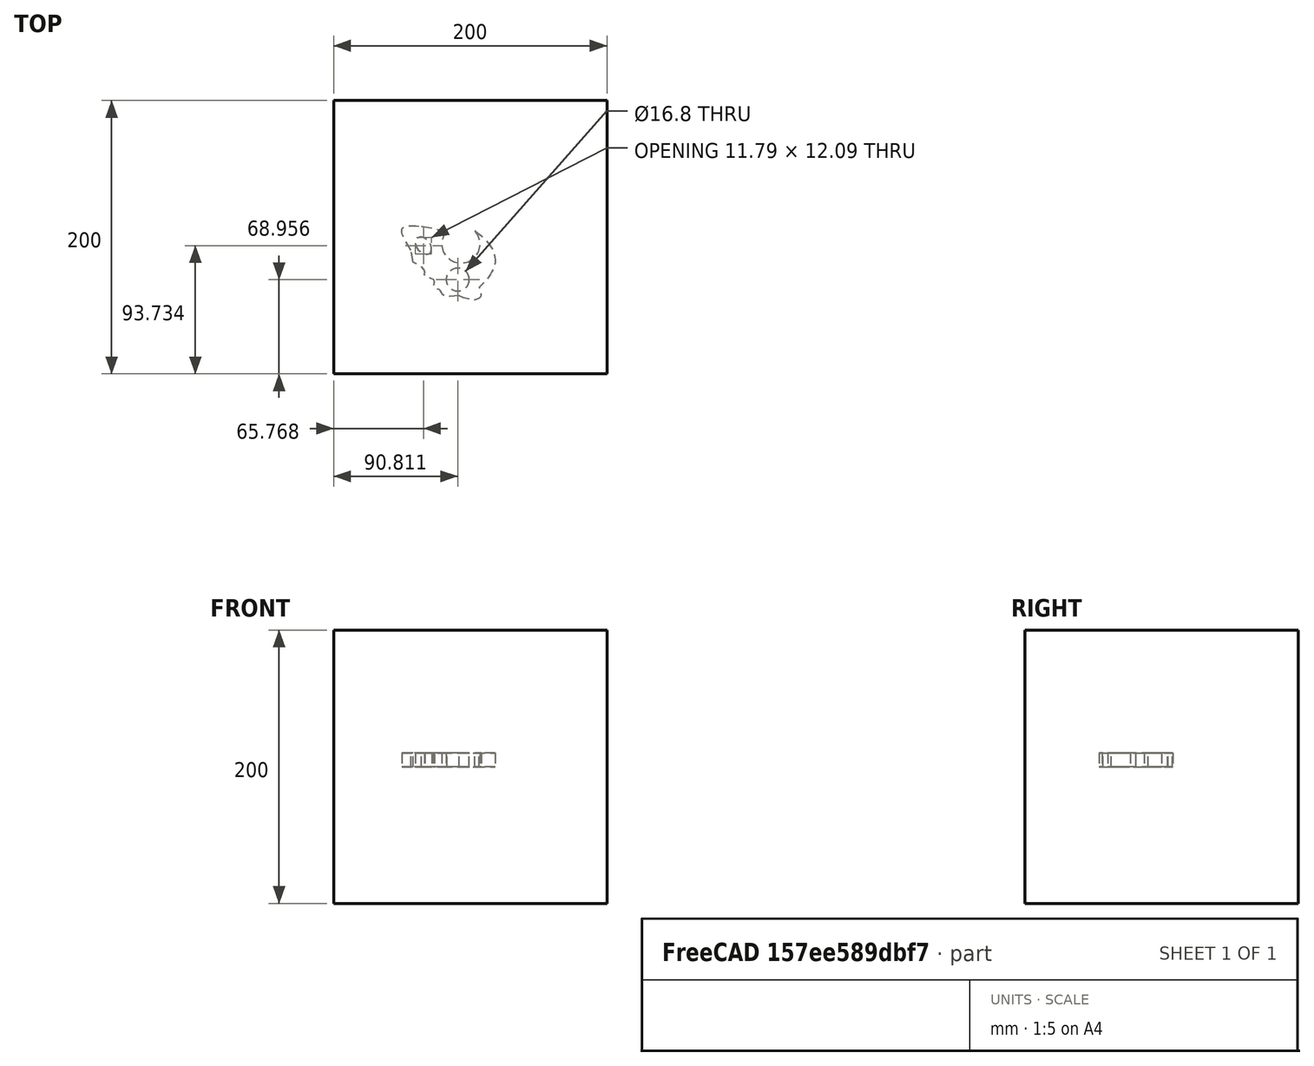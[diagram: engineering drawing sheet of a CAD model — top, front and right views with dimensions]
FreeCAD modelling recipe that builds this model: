
FCSTD DOCUMENT  (FreeCAD 0.19RUnknown)
Label: extrudeAllShapes
License: All rights reserved
LicenseURL: http://en.wikipedia.org/wiki/All_rights_reserved
objects: App::DocumentObjectGroupPython×1248, App::Part×2, Part::FeaturePython×1, Sketcher::SketchObject×1, Part::Extrusion×1
note: 3 computed .brp shape members not serialized (recipe doc carries the construction recipe); baked Part::Feature solids carry a one-line shape summary decoded from their .brp

FEATURE [App::DocumentObjectGroupPython] HALFPI  # scripted group (container) (typed FeaturePython)
  name = HALFPI
  value = pi/2.
FEATURE [App::DocumentObjectGroupPython] PI  # scripted group (container) (typed FeaturePython)
  name = PI
  value = 1.*pi
FEATURE [App::DocumentObjectGroupPython] TWOPI  # scripted group (container) (typed FeaturePython)
  name = TWOPI
  value = 2.*pi
FEATURE [App::DocumentObjectGroupPython] Constants  # scripted group (container) (typed FeaturePython)
  Group = -> [HALFPI,PI,TWOPI]
FEATURE [App::DocumentObjectGroupPython] Variables  # scripted group (container) (typed FeaturePython)
FEATURE [App::DocumentObjectGroupPython] Quantities  # scripted group (container) (typed FeaturePython)
FEATURE [App::DocumentObjectGroupPython] Isotopes  # scripted group (container) (typed FeaturePython)
FEATURE [App::DocumentObjectGroupPython] Elements  # scripted group (container) (typed FeaturePython)
FEATURE [App::DocumentObjectGroupPython] G4Isotopes  # scripted group (container) (typed FeaturePython)
FEATURE [App::DocumentObjectGroupPython] H_element  # scripted group (container) (typed FeaturePython)
  Z = 1
  atom_value = 1.008
  formula = H
  name = H_element
FEATURE [App::DocumentObjectGroupPython] He_element  # scripted group (container) (typed FeaturePython)
  Z = 2
  atom_value = 4.0026
  formula = He
  name = He_element
FEATURE [App::DocumentObjectGroupPython] Li_element  # scripted group (container) (typed FeaturePython)
  Z = 3
  atom_value = 6.94
  formula = Li
  name = Li_element
FEATURE [App::DocumentObjectGroupPython] Be_element  # scripted group (container) (typed FeaturePython)
  Z = 4
  atom_value = 9.01218
  formula = Be
  name = Be_element
FEATURE [App::DocumentObjectGroupPython] B_element  # scripted group (container) (typed FeaturePython)
  Z = 5
  atom_value = 10.81
  formula = B
  name = B_element
FEATURE [App::DocumentObjectGroupPython] C_element  # scripted group (container) (typed FeaturePython)
  Z = 6
  atom_value = 12.011
  formula = C
  name = C_element
FEATURE [App::DocumentObjectGroupPython] N_element  # scripted group (container) (typed FeaturePython)
  Z = 7
  atom_value = 14.007
  formula = N
  name = N_element
FEATURE [App::DocumentObjectGroupPython] O_element  # scripted group (container) (typed FeaturePython)
  Z = 8
  atom_value = 15.999
  formula = O
  name = O_element
FEATURE [App::DocumentObjectGroupPython] F_element  # scripted group (container) (typed FeaturePython)
  Z = 9
  atom_value = 18.9984
  formula = F
  name = F_element
FEATURE [App::DocumentObjectGroupPython] Ne_element  # scripted group (container) (typed FeaturePython)
  Z = 10
  atom_value = 20.1797
  formula = Ne
  name = Ne_element
FEATURE [App::DocumentObjectGroupPython] Na_element  # scripted group (container) (typed FeaturePython)
  Z = 11
  atom_value = 22.9898
  formula = Na
  name = Na_element
FEATURE [App::DocumentObjectGroupPython] Mg_element  # scripted group (container) (typed FeaturePython)
  Z = 12
  atom_value = 24.305
  formula = Mg
  name = Mg_element
FEATURE [App::DocumentObjectGroupPython] Al_element  # scripted group (container) (typed FeaturePython)
  Z = 13
  atom_value = 26.9815
  formula = Al
  name = Al_element
FEATURE [App::DocumentObjectGroupPython] Si_element  # scripted group (container) (typed FeaturePython)
  Z = 14
  atom_value = 28.085
  formula = Si
  name = Si_element
FEATURE [App::DocumentObjectGroupPython] P_element  # scripted group (container) (typed FeaturePython)
  Z = 15
  atom_value = 30.9738
  formula = P
  name = P_element
FEATURE [App::DocumentObjectGroupPython] S_element  # scripted group (container) (typed FeaturePython)
  Z = 16
  atom_value = 32.06
  formula = S
  name = S_element
FEATURE [App::DocumentObjectGroupPython] Cl_element  # scripted group (container) (typed FeaturePython)
  Z = 17
  atom_value = 35.45
  formula = Cl
  name = Cl_element
FEATURE [App::DocumentObjectGroupPython] Ar_element  # scripted group (container) (typed FeaturePython)
  Z = 18
  atom_value = 39.95
  formula = Ar
  name = Ar_element
FEATURE [App::DocumentObjectGroupPython] K_element  # scripted group (container) (typed FeaturePython)
  Z = 19
  atom_value = 39.0983
  formula = K
  name = K_element
FEATURE [App::DocumentObjectGroupPython] Ca_element  # scripted group (container) (typed FeaturePython)
  Z = 20
  atom_value = 40.078
  formula = Ca
  name = Ca_element
FEATURE [App::DocumentObjectGroupPython] Sc_element  # scripted group (container) (typed FeaturePython)
  Z = 21
  atom_value = 44.9559
  formula = Sc
  name = Sc_element
FEATURE [App::DocumentObjectGroupPython] Ti_element  # scripted group (container) (typed FeaturePython)
  Z = 22
  atom_value = 47.867
  formula = Ti
  name = Ti_element
FEATURE [App::DocumentObjectGroupPython] V_element  # scripted group (container) (typed FeaturePython)
  Z = 23
  atom_value = 50.9415
  formula = V
  name = V_element
FEATURE [App::DocumentObjectGroupPython] Cr_element  # scripted group (container) (typed FeaturePython)
  Z = 24
  atom_value = 51.9961
  formula = Cr
  name = Cr_element
FEATURE [App::DocumentObjectGroupPython] Mn_element  # scripted group (container) (typed FeaturePython)
  Z = 25
  atom_value = 54.938
  formula = Mn
  name = Mn_element
FEATURE [App::DocumentObjectGroupPython] Fe_element  # scripted group (container) (typed FeaturePython)
  Z = 26
  atom_value = 55.845
  formula = Fe
  name = Fe_element
FEATURE [App::DocumentObjectGroupPython] Co_element  # scripted group (container) (typed FeaturePython)
  Z = 27
  atom_value = 58.9332
  formula = Co
  name = Co_element
FEATURE [App::DocumentObjectGroupPython] Ni_element  # scripted group (container) (typed FeaturePython)
  Z = 28
  atom_value = 58.6934
  formula = Ni
  name = Ni_element
FEATURE [App::DocumentObjectGroupPython] Cu_element  # scripted group (container) (typed FeaturePython)
  Z = 29
  atom_value = 63.546
  formula = Cu
  name = Cu_element
FEATURE [App::DocumentObjectGroupPython] Zn_element  # scripted group (container) (typed FeaturePython)
  Z = 30
  atom_value = 65.38
  formula = Zn
  name = Zn_element
FEATURE [App::DocumentObjectGroupPython] Ga_element  # scripted group (container) (typed FeaturePython)
  Z = 31
  atom_value = 69.723
  formula = Ga
  name = Ga_element
FEATURE [App::DocumentObjectGroupPython] Ge_element  # scripted group (container) (typed FeaturePython)
  Z = 32
  atom_value = 72.63
  formula = Ge
  name = Ge_element
FEATURE [App::DocumentObjectGroupPython] As_element  # scripted group (container) (typed FeaturePython)
  Z = 33
  atom_value = 74.9216
  formula = As
  name = As_element
FEATURE [App::DocumentObjectGroupPython] Se_element  # scripted group (container) (typed FeaturePython)
  Z = 34
  atom_value = 78.971
  formula = Se
  name = Se_element
FEATURE [App::DocumentObjectGroupPython] Br_element  # scripted group (container) (typed FeaturePython)
  Z = 35
  atom_value = 79.904
  formula = Br
  name = Br_element
FEATURE [App::DocumentObjectGroupPython] Kr_element  # scripted group (container) (typed FeaturePython)
  Z = 36
  atom_value = 83.798
  formula = Kr
  name = Kr_element
FEATURE [App::DocumentObjectGroupPython] Rb_element  # scripted group (container) (typed FeaturePython)
  Z = 37
  atom_value = 85.4678
  formula = Rb
  name = Rb_element
FEATURE [App::DocumentObjectGroupPython] Sr_element  # scripted group (container) (typed FeaturePython)
  Z = 38
  atom_value = 87.62
  formula = Sr
  name = Sr_element
FEATURE [App::DocumentObjectGroupPython] Y_element  # scripted group (container) (typed FeaturePython)
  Z = 39
  atom_value = 88.9058
  formula = Y
  name = Y_element
FEATURE [App::DocumentObjectGroupPython] Zr_element  # scripted group (container) (typed FeaturePython)
  Z = 40
  atom_value = 91.224
  formula = Zr
  name = Zr_element
FEATURE [App::DocumentObjectGroupPython] Nb_element  # scripted group (container) (typed FeaturePython)
  Z = 41
  atom_value = 92.9064
  formula = Nb
  name = Nb_element
FEATURE [App::DocumentObjectGroupPython] Mo_element  # scripted group (container) (typed FeaturePython)
  Z = 42
  atom_value = 95.95
  formula = Mo
  name = Mo_element
FEATURE [App::DocumentObjectGroupPython] Tc_element  # scripted group (container) (typed FeaturePython)
  Z = 43
  atom_value = 97
  formula = Tc
  name = Tc_element
FEATURE [App::DocumentObjectGroupPython] Ru_element  # scripted group (container) (typed FeaturePython)
  Z = 44
  atom_value = 101.07
  formula = Ru
  name = Ru_element
FEATURE [App::DocumentObjectGroupPython] Rh_element  # scripted group (container) (typed FeaturePython)
  Z = 45
  atom_value = 102.905
  formula = Rh
  name = Rh_element
FEATURE [App::DocumentObjectGroupPython] Pd_element  # scripted group (container) (typed FeaturePython)
  Z = 46
  atom_value = 106.42
  formula = Pd
  name = Pd_element
FEATURE [App::DocumentObjectGroupPython] Ag_element  # scripted group (container) (typed FeaturePython)
  Z = 47
  atom_value = 107.868
  formula = Ag
  name = Ag_element
FEATURE [App::DocumentObjectGroupPython] Cd_element  # scripted group (container) (typed FeaturePython)
  Z = 48
  atom_value = 112.414
  formula = Cd
  name = Cd_element
FEATURE [App::DocumentObjectGroupPython] In_element  # scripted group (container) (typed FeaturePython)
  Z = 49
  atom_value = 114.818
  formula = In
  name = In_element
FEATURE [App::DocumentObjectGroupPython] Sn_element  # scripted group (container) (typed FeaturePython)
  Z = 50
  atom_value = 118.71
  formula = Sn
  name = Sn_element
FEATURE [App::DocumentObjectGroupPython] Sb_element  # scripted group (container) (typed FeaturePython)
  Z = 51
  atom_value = 121.76
  formula = Sb
  name = Sb_element
FEATURE [App::DocumentObjectGroupPython] Te_element  # scripted group (container) (typed FeaturePython)
  Z = 52
  atom_value = 127.6
  formula = Te
  name = Te_element
FEATURE [App::DocumentObjectGroupPython] I_element  # scripted group (container) (typed FeaturePython)
  Z = 53
  atom_value = 126.904
  formula = I
  name = I_element
FEATURE [App::DocumentObjectGroupPython] Xe_element  # scripted group (container) (typed FeaturePython)
  Z = 54
  atom_value = 131.293
  formula = Xe
  name = Xe_element
FEATURE [App::DocumentObjectGroupPython] Cs_element  # scripted group (container) (typed FeaturePython)
  Z = 55
  atom_value = 132.905
  formula = Cs
  name = Cs_element
FEATURE [App::DocumentObjectGroupPython] Ba_element  # scripted group (container) (typed FeaturePython)
  Z = 56
  atom_value = 137.327
  formula = Ba
  name = Ba_element
FEATURE [App::DocumentObjectGroupPython] La_element  # scripted group (container) (typed FeaturePython)
  Z = 57
  atom_value = 138.905
  formula = La
  name = La_element
FEATURE [App::DocumentObjectGroupPython] Ce_element  # scripted group (container) (typed FeaturePython)
  Z = 58
  atom_value = 140.116
  formula = Ce
  name = Ce_element
FEATURE [App::DocumentObjectGroupPython] Pr_element  # scripted group (container) (typed FeaturePython)
  Z = 59
  atom_value = 140.908
  formula = Pr
  name = Pr_element
FEATURE [App::DocumentObjectGroupPython] Nd_element  # scripted group (container) (typed FeaturePython)
  Z = 60
  atom_value = 144.242
  formula = Nd
  name = Nd_element
FEATURE [App::DocumentObjectGroupPython] Pm_element  # scripted group (container) (typed FeaturePython)
  Z = 61
  atom_value = 145
  formula = Pm
  name = Pm_element
FEATURE [App::DocumentObjectGroupPython] Sm_element  # scripted group (container) (typed FeaturePython)
  Z = 62
  atom_value = 150.36
  formula = Sm
  name = Sm_element
FEATURE [App::DocumentObjectGroupPython] Eu_element  # scripted group (container) (typed FeaturePython)
  Z = 63
  atom_value = 151.964
  formula = Eu
  name = Eu_element
FEATURE [App::DocumentObjectGroupPython] Gd_element  # scripted group (container) (typed FeaturePython)
  Z = 64
  atom_value = 157.25
  formula = Gd
  name = Gd_element
FEATURE [App::DocumentObjectGroupPython] Tb_element  # scripted group (container) (typed FeaturePython)
  Z = 65
  atom_value = 158.925
  formula = Tb
  name = Tb_element
FEATURE [App::DocumentObjectGroupPython] Dy_element  # scripted group (container) (typed FeaturePython)
  Z = 66
  atom_value = 162.5
  formula = Dy
  name = Dy_element
FEATURE [App::DocumentObjectGroupPython] Ho_element  # scripted group (container) (typed FeaturePython)
  Z = 67
  atom_value = 164.93
  formula = Ho
  name = Ho_element
FEATURE [App::DocumentObjectGroupPython] Er_element  # scripted group (container) (typed FeaturePython)
  Z = 68
  atom_value = 167.259
  formula = Er
  name = Er_element
FEATURE [App::DocumentObjectGroupPython] Tm_element  # scripted group (container) (typed FeaturePython)
  Z = 69
  atom_value = 168.934
  formula = Tm
  name = Tm_element
FEATURE [App::DocumentObjectGroupPython] Yb_element  # scripted group (container) (typed FeaturePython)
  Z = 70
  atom_value = 173.045
  formula = Yb
  name = Yb_element
FEATURE [App::DocumentObjectGroupPython] Lu_element  # scripted group (container) (typed FeaturePython)
  Z = 71
  atom_value = 174.967
  formula = Lu
  name = Lu_element
FEATURE [App::DocumentObjectGroupPython] Hf_element  # scripted group (container) (typed FeaturePython)
  Z = 72
  atom_value = 178.49
  formula = Hf
  name = Hf_element
FEATURE [App::DocumentObjectGroupPython] Ta_element  # scripted group (container) (typed FeaturePython)
  Z = 73
  atom_value = 180.948
  formula = Ta
  name = Ta_element
FEATURE [App::DocumentObjectGroupPython] W_element  # scripted group (container) (typed FeaturePython)
  Z = 74
  atom_value = 183.84
  formula = W
  name = W_element
FEATURE [App::DocumentObjectGroupPython] Re_element  # scripted group (container) (typed FeaturePython)
  Z = 75
  atom_value = 186.207
  formula = Re
  name = Re_element
FEATURE [App::DocumentObjectGroupPython] Os_element  # scripted group (container) (typed FeaturePython)
  Z = 76
  atom_value = 190.23
  formula = Os
  name = Os_element
FEATURE [App::DocumentObjectGroupPython] Ir_element  # scripted group (container) (typed FeaturePython)
  Z = 77
  atom_value = 192.217
  formula = Ir
  name = Ir_element
FEATURE [App::DocumentObjectGroupPython] Pt_element  # scripted group (container) (typed FeaturePython)
  Z = 78
  atom_value = 195.084
  formula = Pt
  name = Pt_element
FEATURE [App::DocumentObjectGroupPython] Au_element  # scripted group (container) (typed FeaturePython)
  Z = 79
  atom_value = 196.967
  formula = Au
  name = Au_element
FEATURE [App::DocumentObjectGroupPython] Hg_element  # scripted group (container) (typed FeaturePython)
  Z = 80
  atom_value = 200.592
  formula = Hg
  name = Hg_element
FEATURE [App::DocumentObjectGroupPython] Tl_element  # scripted group (container) (typed FeaturePython)
  Z = 81
  atom_value = 204.38
  formula = Tl
  name = Tl_element
FEATURE [App::DocumentObjectGroupPython] Pb_element  # scripted group (container) (typed FeaturePython)
  Z = 82
  atom_value = 207.2
  formula = Pb
  name = Pb_element
FEATURE [App::DocumentObjectGroupPython] Bi_element  # scripted group (container) (typed FeaturePython)
  Z = 83
  atom_value = 208.98
  formula = Bi
  name = Bi_element
FEATURE [App::DocumentObjectGroupPython] Po_element  # scripted group (container) (typed FeaturePython)
  Z = 84
  atom_value = 209
  formula = Po
  name = Po_element
FEATURE [App::DocumentObjectGroupPython] At_element  # scripted group (container) (typed FeaturePython)
  Z = 85
  atom_value = 210
  formula = At
  name = At_element
FEATURE [App::DocumentObjectGroupPython] Rn_element  # scripted group (container) (typed FeaturePython)
  Z = 86
  atom_value = 222
  formula = Rn
  name = Rn_element
FEATURE [App::DocumentObjectGroupPython] Fr_element  # scripted group (container) (typed FeaturePython)
  Z = 87
  atom_value = 223
  formula = Fr
  name = Fr_element
FEATURE [App::DocumentObjectGroupPython] Ra_element  # scripted group (container) (typed FeaturePython)
  Z = 88
  atom_value = 226
  formula = Ra
  name = Ra_element
FEATURE [App::DocumentObjectGroupPython] Ac_element  # scripted group (container) (typed FeaturePython)
  Z = 89
  atom_value = 227
  formula = Ac
  name = Ac_element
FEATURE [App::DocumentObjectGroupPython] Th_element  # scripted group (container) (typed FeaturePython)
  Z = 90
  atom_value = 232.038
  formula = Th
  name = Th_element
FEATURE [App::DocumentObjectGroupPython] Pa_element  # scripted group (container) (typed FeaturePython)
  Z = 91
  atom_value = 231.036
  formula = Pa
  name = Pa_element
FEATURE [App::DocumentObjectGroupPython] U_element  # scripted group (container) (typed FeaturePython)
  Z = 92
  atom_value = 238.029
  formula = U
  name = U_element
FEATURE [App::DocumentObjectGroupPython] Np_element  # scripted group (container) (typed FeaturePython)
  Z = 93
  atom_value = 237
  formula = Np
  name = Np_element
FEATURE [App::DocumentObjectGroupPython] Pu_element  # scripted group (container) (typed FeaturePython)
  Z = 94
  atom_value = 244
  formula = Pu
  name = Pu_element
FEATURE [App::DocumentObjectGroupPython] Am_element  # scripted group (container) (typed FeaturePython)
  Z = 95
  atom_value = 243
  formula = Am
  name = Am_element
FEATURE [App::DocumentObjectGroupPython] Cm_element  # scripted group (container) (typed FeaturePython)
  Z = 96
  atom_value = 247
  formula = Cm
  name = Cm_element
FEATURE [App::DocumentObjectGroupPython] Bk_element  # scripted group (container) (typed FeaturePython)
  Z = 97
  atom_value = 247
  formula = Bk
  name = Bk_element
FEATURE [App::DocumentObjectGroupPython] Cf_element  # scripted group (container) (typed FeaturePython)
  Z = 98
  atom_value = 251
  formula = Cf
  name = Cf_element
FEATURE [App::DocumentObjectGroupPython] G4Elements  # scripted group (container) (typed FeaturePython)
  Group = -> [H_element,He_element,Li_element,Be_element,B_element,C_element,N_element,O_element,F_element,Ne_element,Na_element,Mg_element,Al_element,Si_element,P_element,S_element,Cl_element,Ar_element,K_element,Ca_element,Sc_element,Ti_element,V_element,Cr_element,Mn_element,Fe_element,Co_element,Ni_element,Cu_element,Zn_element,Ga_element,Ge_element,As_element,Se_element,Br_element,Kr_element,Rb_element,+61 more]
FEATURE [App::DocumentObjectGroupPython] H_element001  label="H_element : 0.101"  # scripted group (container) (typed FeaturePython)
  n = 0.101327
FEATURE [App::DocumentObjectGroupPython] C_element001  label="C_element : 0.775"  # scripted group (container) (typed FeaturePython)
  n = 0.7755
FEATURE [App::DocumentObjectGroupPython] N_element001  label="N_element : 0.035"  # scripted group (container) (typed FeaturePython)
  n = 0.035057
FEATURE [App::DocumentObjectGroupPython] O_element001  label="O_element : 0.052"  # scripted group (container) (typed FeaturePython)
  n = 0.0523159
FEATURE [App::DocumentObjectGroupPython] F_element001  label="F_element : 0.017"  # scripted group (container) (typed FeaturePython)
  n = 0.017422
FEATURE [App::DocumentObjectGroupPython] Ca_element001  label="Ca_element : 0.018"  # scripted group (container) (typed FeaturePython)
  n = 0.018378
FEATURE [App::DocumentObjectGroupPython] G4_A_150_TISSUE  label="G4_A-150_TISSUE"  # scripted group (container) (typed FeaturePython)
  Dunit = g/cm3
  Dvalue = 1.127
  Group = -> [H_element001,C_element001,N_element001,O_element001,F_element001,Ca_element001]
  conduct = 2
  density = 1
  expand = 3
  formula = G4_A-150_TISSUE
  name = G4_A-150_TISSUE
  specific = 4
FEATURE [App::DocumentObjectGroupPython] C_element002  label="C_element : 3"  # scripted group (container) (typed FeaturePython)
  n = 3
  ref = C_element
FEATURE [App::DocumentObjectGroupPython] H_element002  label="H_element : 6"  # scripted group (container) (typed FeaturePython)
  n = 6
  ref = H_element
FEATURE [App::DocumentObjectGroupPython] O_element002  label="O_element : 1"  # scripted group (container) (typed FeaturePython)
  n = 1
  ref = O_element
FEATURE [App::DocumentObjectGroupPython] G4_ACETONE  # scripted group (container) (typed FeaturePython)
  Dunit = g/cm3
  Dvalue = 0.7899
  Group = -> [C_element002,H_element002,O_element002]
  conduct = 2
  density = 1
  expand = 3
  formula = G4_ACETONE
  name = G4_ACETONE
  specific = 4
FEATURE [App::DocumentObjectGroupPython] C_element003  label="C_element : 2"  # scripted group (container) (typed FeaturePython)
  n = 2
  ref = C_element
FEATURE [App::DocumentObjectGroupPython] H_element003  label="H_element : 2"  # scripted group (container) (typed FeaturePython)
  n = 2
  ref = H_element
FEATURE [App::DocumentObjectGroupPython] G4_ACETYLENE  # scripted group (container) (typed FeaturePython)
  Dunit = g/cm3
  Dvalue = 0.0010967
  Group = -> [C_element003,H_element003]
  conduct = 2
  density = 1
  expand = 3
  formula = G4_ACETYLENE
  name = G4_ACETYLENE
  specific = 4
FEATURE [App::DocumentObjectGroupPython] C_element004  label="C_element : 5"  # scripted group (container) (typed FeaturePython)
  n = 5
  ref = C_element
FEATURE [App::DocumentObjectGroupPython] H_element004  label="H_element : 5"  # scripted group (container) (typed FeaturePython)
  n = 5
  ref = H_element
FEATURE [App::DocumentObjectGroupPython] N_element002  label="N_element : 5"  # scripted group (container) (typed FeaturePython)
  n = 5
  ref = N_element
FEATURE [App::DocumentObjectGroupPython] G4_ADENINE  # scripted group (container) (typed FeaturePython)
  Dunit = g/cm3
  Dvalue = 1.6
  Group = -> [C_element004,H_element004,N_element002]
  conduct = 2
  density = 1
  expand = 3
  formula = G4_ADENINE
  name = G4_ADENINE
  specific = 4
FEATURE [App::DocumentObjectGroupPython] H_element005  label="H_element : 0.114"  # scripted group (container) (typed FeaturePython)
  n = 0.114
FEATURE [App::DocumentObjectGroupPython] C_element005  label="C_element : 0.598"  # scripted group (container) (typed FeaturePython)
  n = 0.598
FEATURE [App::DocumentObjectGroupPython] N_element003  label="N_element : 0.007"  # scripted group (container) (typed FeaturePython)
  n = 0.007
FEATURE [App::DocumentObjectGroupPython] O_element003  label="O_element : 0.278"  # scripted group (container) (typed FeaturePython)
  n = 0.278
FEATURE [App::DocumentObjectGroupPython] Na_element001  label="Na_element : 0.001"  # scripted group (container) (typed FeaturePython)
  n = 0.001
FEATURE [App::DocumentObjectGroupPython] S_element001  label="S_element : 0.001"  # scripted group (container) (typed FeaturePython)
  n = 0.001
FEATURE [App::DocumentObjectGroupPython] Cl_element001  label="Cl_element : 0.001"  # scripted group (container) (typed FeaturePython)
  n = 0.001
FEATURE [App::DocumentObjectGroupPython] G4_ADIPOSE_TISSUE_ICRP  # scripted group (container) (typed FeaturePython)
  Dunit = g/cm3
  Dvalue = 0.95
  Group = -> [H_element005,C_element005,N_element003,O_element003,Na_element001,S_element001,Cl_element001]
  conduct = 2
  density = 1
  expand = 3
  formula = G4_ADIPOSE_TISSUE_ICRP
  name = G4_ADIPOSE_TISSUE_ICRP
  specific = 4
FEATURE [App::DocumentObjectGroupPython] C_element006  label="C_element : 0.000"  # scripted group (container) (typed FeaturePython)
  n = 0.000124
FEATURE [App::DocumentObjectGroupPython] N_element004  label="N_element : 0.755"  # scripted group (container) (typed FeaturePython)
  n = 0.755268
FEATURE [App::DocumentObjectGroupPython] O_element004  label="O_element : 0.232"  # scripted group (container) (typed FeaturePython)
  n = 0.231781
FEATURE [App::DocumentObjectGroupPython] Ar_element001  label="Ar_element : 0.013"  # scripted group (container) (typed FeaturePython)
  n = 0.012827
FEATURE [App::DocumentObjectGroupPython] G4_AIR  # scripted group (container) (typed FeaturePython)
  Dunit = g/cm3
  Dvalue = 0.00120479
  Group = -> [C_element006,N_element004,O_element004,Ar_element001]
  conduct = 2
  density = 1
  expand = 3
  formula = G4_AIR
  name = G4_AIR
  specific = 4
FEATURE [App::DocumentObjectGroupPython] C_element007  label="C_element : 006"  # scripted group (container) (typed FeaturePython)
  n = 3
  ref = C_element
FEATURE [App::DocumentObjectGroupPython] H_element006  label="H_element : 7"  # scripted group (container) (typed FeaturePython)
  n = 7
  ref = H_element
FEATURE [App::DocumentObjectGroupPython] N_element005  label="N_element : 1"  # scripted group (container) (typed FeaturePython)
  n = 1
  ref = N_element
FEATURE [App::DocumentObjectGroupPython] O_element005  label="O_element : 2"  # scripted group (container) (typed FeaturePython)
  n = 2
  ref = O_element
FEATURE [App::DocumentObjectGroupPython] G4_ALANINE  # scripted group (container) (typed FeaturePython)
  Dunit = g/cm3
  Dvalue = 1.42
  Group = -> [C_element007,H_element006,N_element005,O_element005]
  conduct = 2
  density = 1
  expand = 3
  formula = G4_ALANINE
  name = G4_ALANINE
  specific = 4
FEATURE [App::DocumentObjectGroupPython] Al_element001  label="Al_element : 2"  # scripted group (container) (typed FeaturePython)
  n = 2
  ref = Al_element
FEATURE [App::DocumentObjectGroupPython] O_element006  label="O_element : 3"  # scripted group (container) (typed FeaturePython)
  n = 3
  ref = O_element
FEATURE [App::DocumentObjectGroupPython] G4_ALUMINUM_OXIDE  # scripted group (container) (typed FeaturePython)
  Dunit = g/cm3
  Dvalue = 3.97
  Group = -> [Al_element001,O_element006]
  conduct = 2
  density = 1
  expand = 3
  formula = G4_ALUMINUM_OXIDE
  name = G4_ALUMINUM_OXIDE
  specific = 4
FEATURE [App::DocumentObjectGroupPython] H_element007  label="H_element : 0.106"  # scripted group (container) (typed FeaturePython)
  n = 0.10593
FEATURE [App::DocumentObjectGroupPython] C_element008  label="C_element : 0.789"  # scripted group (container) (typed FeaturePython)
  n = 0.788974
FEATURE [App::DocumentObjectGroupPython] O_element007  label="O_element : 0.105"  # scripted group (container) (typed FeaturePython)
  n = 0.105096
FEATURE [App::DocumentObjectGroupPython] G4_AMBER  # scripted group (container) (typed FeaturePython)
  Dunit = g/cm3
  Dvalue = 1.1
  Group = -> [H_element007,C_element008,O_element007]
  conduct = 2
  density = 1
  expand = 3
  formula = G4_AMBER
  name = G4_AMBER
  specific = 4
FEATURE [App::DocumentObjectGroupPython] N_element006  label="N_element : 006"  # scripted group (container) (typed FeaturePython)
  n = 1
  ref = N_element
FEATURE [App::DocumentObjectGroupPython] H_element008  label="H_element : 3"  # scripted group (container) (typed FeaturePython)
  n = 3
  ref = H_element
FEATURE [App::DocumentObjectGroupPython] G4_AMMONIA  # scripted group (container) (typed FeaturePython)
  Dunit = g/cm3
  Dvalue = 0.000826019
  Group = -> [N_element006,H_element008]
  conduct = 2
  density = 1
  expand = 3
  formula = G4_AMMONIA
  name = G4_AMMONIA
  specific = 4
FEATURE [App::DocumentObjectGroupPython] C_element009  label="C_element : 6"  # scripted group (container) (typed FeaturePython)
  n = 6
  ref = C_element
FEATURE [App::DocumentObjectGroupPython] H_element009  label="H_element : 008"  # scripted group (container) (typed FeaturePython)
  n = 7
  ref = H_element
FEATURE [App::DocumentObjectGroupPython] N_element007  label="N_element : 007"  # scripted group (container) (typed FeaturePython)
  n = 1
  ref = N_element
FEATURE [App::DocumentObjectGroupPython] G4_ANILINE  # scripted group (container) (typed FeaturePython)
  Dunit = g/cm3
  Dvalue = 1.0235
  Group = -> [C_element009,H_element009,N_element007]
  conduct = 2
  density = 1
  expand = 3
  formula = G4_ANILINE
  name = G4_ANILINE
  specific = 4
FEATURE [App::DocumentObjectGroupPython] C_element010  label="C_element : 14"  # scripted group (container) (typed FeaturePython)
  n = 14
  ref = C_element
FEATURE [App::DocumentObjectGroupPython] H_element010  label="H_element : 10"  # scripted group (container) (typed FeaturePython)
  n = 10
  ref = H_element
FEATURE [App::DocumentObjectGroupPython] G4_ANTHRACENE  # scripted group (container) (typed FeaturePython)
  Dunit = g/cm3
  Dvalue = 1.283
  Group = -> [C_element010,H_element010]
  conduct = 2
  density = 1
  expand = 3
  formula = G4_ANTHRACENE
  name = G4_ANTHRACENE
  specific = 4
FEATURE [App::DocumentObjectGroupPython] H_element011  label="H_element : 0.065"  # scripted group (container) (typed FeaturePython)
  n = 0.0654709
FEATURE [App::DocumentObjectGroupPython] C_element011  label="C_element : 0.537"  # scripted group (container) (typed FeaturePython)
  n = 0.536944
FEATURE [App::DocumentObjectGroupPython] N_element008  label="N_element : 0.021"  # scripted group (container) (typed FeaturePython)
  n = 0.0215
FEATURE [App::DocumentObjectGroupPython] O_element008  label="O_element : 0.032"  # scripted group (container) (typed FeaturePython)
  n = 0.032085
FEATURE [App::DocumentObjectGroupPython] F_element002  label="F_element : 0.167"  # scripted group (container) (typed FeaturePython)
  n = 0.167411
FEATURE [App::DocumentObjectGroupPython] Ca_element002  label="Ca_element : 0.177"  # scripted group (container) (typed FeaturePython)
  n = 0.176589
FEATURE [App::DocumentObjectGroupPython] G4_B_100_BONE  label="G4_B-100_BONE"  # scripted group (container) (typed FeaturePython)
  Dunit = g/cm3
  Dvalue = 1.45
  Group = -> [H_element011,C_element011,N_element008,O_element008,F_element002,Ca_element002]
  conduct = 2
  density = 1
  expand = 3
  formula = G4_B-100_BONE
  name = G4_B-100_BONE
  specific = 4
FEATURE [App::DocumentObjectGroupPython] H_element012  label="H_element : 0.057"  # scripted group (container) (typed FeaturePython)
  n = 0.057441
FEATURE [App::DocumentObjectGroupPython] C_element012  label="C_element : 0.790"  # scripted group (container) (typed FeaturePython)
  n = 0.774591
FEATURE [App::DocumentObjectGroupPython] O_element009  label="O_element : 0.168"  # scripted group (container) (typed FeaturePython)
  n = 0.167968
FEATURE [App::DocumentObjectGroupPython] G4_BAKELITE  # scripted group (container) (typed FeaturePython)
  Dunit = g/cm3
  Dvalue = 1.25
  Group = -> [H_element012,C_element012,O_element009]
  conduct = 2
  density = 1
  expand = 3
  formula = G4_BAKELITE
  name = G4_BAKELITE
  specific = 4
FEATURE [App::DocumentObjectGroupPython] Ba_element001  label="Ba_element : 1"  # scripted group (container) (typed FeaturePython)
  n = 1
  ref = Ba_element
FEATURE [App::DocumentObjectGroupPython] F_element003  label="F_element : 2"  # scripted group (container) (typed FeaturePython)
  n = 2
  ref = F_element
FEATURE [App::DocumentObjectGroupPython] G4_BARIUM_FLUORIDE  # scripted group (container) (typed FeaturePython)
  Dunit = g/cm3
  Dvalue = 4.89
  Group = -> [Ba_element001,F_element003]
  conduct = 2
  density = 1
  expand = 3
  formula = G4_BARIUM_FLUORIDE
  name = G4_BARIUM_FLUORIDE
  specific = 4
FEATURE [App::DocumentObjectGroupPython] Ba_element002  label="Ba_element : 002"  # scripted group (container) (typed FeaturePython)
  n = 1
  ref = Ba_element
FEATURE [App::DocumentObjectGroupPython] S_element002  label="S_element : 1"  # scripted group (container) (typed FeaturePython)
  n = 1
  ref = S_element
FEATURE [App::DocumentObjectGroupPython] O_element010  label="O_element : 4"  # scripted group (container) (typed FeaturePython)
  n = 4
  ref = O_element
FEATURE [App::DocumentObjectGroupPython] G4_BARIUM_SULFATE  # scripted group (container) (typed FeaturePython)
  Dunit = g/cm3
  Dvalue = 4.5
  Group = -> [Ba_element002,S_element002,O_element010]
  conduct = 2
  density = 1
  expand = 3
  formula = G4_BARIUM_SULFATE
  name = G4_BARIUM_SULFATE
  specific = 4
FEATURE [App::DocumentObjectGroupPython] C_element013  label="C_element : 007"  # scripted group (container) (typed FeaturePython)
  n = 6
  ref = C_element
FEATURE [App::DocumentObjectGroupPython] H_element013  label="H_element : 009"  # scripted group (container) (typed FeaturePython)
  n = 6
  ref = H_element
FEATURE [App::DocumentObjectGroupPython] G4_BENZENE  # scripted group (container) (typed FeaturePython)
  Dunit = g/cm3
  Dvalue = 0.87865
  Group = -> [C_element013,H_element013]
  conduct = 2
  density = 1
  expand = 3
  formula = G4_BENZENE
  name = G4_BENZENE
  specific = 4
FEATURE [App::DocumentObjectGroupPython] Be_element001  label="Be_element : 1"  # scripted group (container) (typed FeaturePython)
  n = 1
  ref = Be_element
FEATURE [App::DocumentObjectGroupPython] O_element011  label="O_element : 005"  # scripted group (container) (typed FeaturePython)
  n = 1
  ref = O_element
FEATURE [App::DocumentObjectGroupPython] G4_BERYLLIUM_OXIDE  # scripted group (container) (typed FeaturePython)
  Dunit = g/cm3
  Dvalue = 3.01
  Group = -> [Be_element001,O_element011]
  conduct = 2
  density = 1
  expand = 3
  formula = G4_BERYLLIUM_OXIDE
  name = G4_BERYLLIUM_OXIDE
  specific = 4
FEATURE [App::DocumentObjectGroupPython] Bi_element001  label="Bi_element : 4"  # scripted group (container) (typed FeaturePython)
  n = 4
  ref = Bi_element
FEATURE [App::DocumentObjectGroupPython] Ge_element001  label="Ge_element : 3"  # scripted group (container) (typed FeaturePython)
  n = 3
  ref = Ge_element
FEATURE [App::DocumentObjectGroupPython] O_element012  label="O_element : 12"  # scripted group (container) (typed FeaturePython)
  n = 12
  ref = O_element
FEATURE [App::DocumentObjectGroupPython] G4_BGO  # scripted group (container) (typed FeaturePython)
  Dunit = g/cm3
  Dvalue = 7.13
  Group = -> [Bi_element001,Ge_element001,O_element012]
  conduct = 2
  density = 1
  expand = 3
  formula = G4_BGO
  name = G4_BGO
  specific = 4
FEATURE [App::DocumentObjectGroupPython] H_element014  label="H_element : 0.102"  # scripted group (container) (typed FeaturePython)
  n = 0.102
FEATURE [App::DocumentObjectGroupPython] C_element014  label="C_element : 0.110"  # scripted group (container) (typed FeaturePython)
  n = 0.11
FEATURE [App::DocumentObjectGroupPython] N_element009  label="N_element : 0.033"  # scripted group (container) (typed FeaturePython)
  n = 0.033
FEATURE [App::DocumentObjectGroupPython] O_element013  label="O_element : 0.745"  # scripted group (container) (typed FeaturePython)
  n = 0.745
FEATURE [App::DocumentObjectGroupPython] Na_element002  label="Na_element : 0.002"  # scripted group (container) (typed FeaturePython)
  n = 0.001
FEATURE [App::DocumentObjectGroupPython] P_element001  label="P_element : 0.001"  # scripted group (container) (typed FeaturePython)
  n = 0.001
FEATURE [App::DocumentObjectGroupPython] S_element003  label="S_element : 0.002"  # scripted group (container) (typed FeaturePython)
  n = 0.002
FEATURE [App::DocumentObjectGroupPython] Cl_element002  label="Cl_element : 0.003"  # scripted group (container) (typed FeaturePython)
  n = 0.003
FEATURE [App::DocumentObjectGroupPython] K_element001  label="K_element : 0.002"  # scripted group (container) (typed FeaturePython)
  n = 0.002
FEATURE [App::DocumentObjectGroupPython] Fe_element001  label="Fe_element : 0.001"  # scripted group (container) (typed FeaturePython)
  n = 0.001
FEATURE [App::DocumentObjectGroupPython] G4_BLOOD_ICRP  # scripted group (container) (typed FeaturePython)
  Dunit = g/cm3
  Dvalue = 1.06
  Group = -> [H_element014,C_element014,N_element009,O_element013,Na_element002,P_element001,S_element003,Cl_element002,K_element001,Fe_element001]
  conduct = 2
  density = 1
  expand = 3
  formula = G4_BLOOD_ICRP
  name = G4_BLOOD_ICRP
  specific = 4
FEATURE [App::DocumentObjectGroupPython] H_element015  label="H_element : 0.064"  # scripted group (container) (typed FeaturePython)
  n = 0.064
FEATURE [App::DocumentObjectGroupPython] C_element015  label="C_element : 0.278"  # scripted group (container) (typed FeaturePython)
  n = 0.278
FEATURE [App::DocumentObjectGroupPython] N_element010  label="N_element : 0.027"  # scripted group (container) (typed FeaturePython)
  n = 0.027
FEATURE [App::DocumentObjectGroupPython] O_element014  label="O_element : 0.410"  # scripted group (container) (typed FeaturePython)
  n = 0.41
FEATURE [App::DocumentObjectGroupPython] Mg_element001  label="Mg_element : 0.002"  # scripted group (container) (typed FeaturePython)
  n = 0.002
FEATURE [App::DocumentObjectGroupPython] P_element002  label="P_element : 0.070"  # scripted group (container) (typed FeaturePython)
  n = 0.07
FEATURE [App::DocumentObjectGroupPython] S_element004  label="S_element : 0.003"  # scripted group (container) (typed FeaturePython)
  n = 0.002
FEATURE [App::DocumentObjectGroupPython] Ca_element003  label="Ca_element : 0.147"  # scripted group (container) (typed FeaturePython)
  n = 0.147
FEATURE [App::DocumentObjectGroupPython] G4_BONE_COMPACT_ICRU  # scripted group (container) (typed FeaturePython)
  Dunit = g/cm3
  Dvalue = 1.85
  Group = -> [H_element015,C_element015,N_element010,O_element014,Mg_element001,P_element002,S_element004,Ca_element003]
  conduct = 2
  density = 1
  expand = 3
  formula = G4_BONE_COMPACT_ICRU
  name = G4_BONE_COMPACT_ICRU
  specific = 4
FEATURE [App::DocumentObjectGroupPython] H_element016  label="H_element : 0.034"  # scripted group (container) (typed FeaturePython)
  n = 0.034
FEATURE [App::DocumentObjectGroupPython] C_element016  label="C_element : 0.155"  # scripted group (container) (typed FeaturePython)
  n = 0.155
FEATURE [App::DocumentObjectGroupPython] N_element011  label="N_element : 0.042"  # scripted group (container) (typed FeaturePython)
  n = 0.042
FEATURE [App::DocumentObjectGroupPython] O_element015  label="O_element : 0.435"  # scripted group (container) (typed FeaturePython)
  n = 0.435
FEATURE [App::DocumentObjectGroupPython] Na_element003  label="Na_element : 0.003"  # scripted group (container) (typed FeaturePython)
  n = 0.001
FEATURE [App::DocumentObjectGroupPython] Mg_element002  label="Mg_element : 0.003"  # scripted group (container) (typed FeaturePython)
  n = 0.002
FEATURE [App::DocumentObjectGroupPython] P_element003  label="P_element : 0.103"  # scripted group (container) (typed FeaturePython)
  n = 0.103
FEATURE [App::DocumentObjectGroupPython] S_element005  label="S_element : 0.004"  # scripted group (container) (typed FeaturePython)
  n = 0.003
FEATURE [App::DocumentObjectGroupPython] Ca_element004  label="Ca_element : 0.225"  # scripted group (container) (typed FeaturePython)
  n = 0.225
FEATURE [App::DocumentObjectGroupPython] G4_BONE_CORTICAL_ICRP  # scripted group (container) (typed FeaturePython)
  Dunit = g/cm3
  Dvalue = 1.92
  Group = -> [H_element016,C_element016,N_element011,O_element015,Na_element003,Mg_element002,P_element003,S_element005,Ca_element004]
  conduct = 2
  density = 1
  expand = 3
  formula = G4_BONE_CORTICAL_ICRP
  name = G4_BONE_CORTICAL_ICRP
  specific = 4
FEATURE [App::DocumentObjectGroupPython] B_element001  label="B_element : 4"  # scripted group (container) (typed FeaturePython)
  n = 4
  ref = B_element
FEATURE [App::DocumentObjectGroupPython] C_element017  label="C_element : 1"  # scripted group (container) (typed FeaturePython)
  n = 1
  ref = C_element
FEATURE [App::DocumentObjectGroupPython] G4_BORON_CARBIDE  # scripted group (container) (typed FeaturePython)
  Dunit = g/cm3
  Dvalue = 2.52
  Group = -> [B_element001,C_element017]
  conduct = 2
  density = 1
  expand = 3
  formula = G4_BORON_CARBIDE
  name = G4_BORON_CARBIDE
  specific = 4
FEATURE [App::DocumentObjectGroupPython] B_element002  label="B_element : 2"  # scripted group (container) (typed FeaturePython)
  n = 2
  ref = B_element
FEATURE [App::DocumentObjectGroupPython] O_element016  label="O_element : 006"  # scripted group (container) (typed FeaturePython)
  n = 3
  ref = O_element
FEATURE [App::DocumentObjectGroupPython] G4_BORON_OXIDE  # scripted group (container) (typed FeaturePython)
  Dunit = g/cm3
  Dvalue = 1.812
  Group = -> [B_element002,O_element016]
  conduct = 2
  density = 1
  expand = 3
  formula = G4_BORON_OXIDE
  name = G4_BORON_OXIDE
  specific = 4
FEATURE [App::DocumentObjectGroupPython] H_element017  label="H_element : 0.107"  # scripted group (container) (typed FeaturePython)
  n = 0.107
FEATURE [App::DocumentObjectGroupPython] C_element018  label="C_element : 0.145"  # scripted group (container) (typed FeaturePython)
  n = 0.145
FEATURE [App::DocumentObjectGroupPython] N_element012  label="N_element : 0.022"  # scripted group (container) (typed FeaturePython)
  n = 0.022
FEATURE [App::DocumentObjectGroupPython] O_element017  label="O_element : 0.712"  # scripted group (container) (typed FeaturePython)
  n = 0.712
FEATURE [App::DocumentObjectGroupPython] Na_element004  label="Na_element : 0.004"  # scripted group (container) (typed FeaturePython)
  n = 0.002
FEATURE [App::DocumentObjectGroupPython] P_element004  label="P_element : 0.004"  # scripted group (container) (typed FeaturePython)
  n = 0.004
FEATURE [App::DocumentObjectGroupPython] S_element006  label="S_element : 0.005"  # scripted group (container) (typed FeaturePython)
  n = 0.002
FEATURE [App::DocumentObjectGroupPython] Cl_element003  label="Cl_element : 0.004"  # scripted group (container) (typed FeaturePython)
  n = 0.003
FEATURE [App::DocumentObjectGroupPython] K_element002  label="K_element : 0.003"  # scripted group (container) (typed FeaturePython)
  n = 0.003
FEATURE [App::DocumentObjectGroupPython] G4_BRAIN_ICRP  # scripted group (container) (typed FeaturePython)
  Dunit = g/cm3
  Dvalue = 1.04
  Group = -> [H_element017,C_element018,N_element012,O_element017,Na_element004,P_element004,S_element006,Cl_element003,K_element002]
  conduct = 2
  density = 1
  expand = 3
  formula = G4_BRAIN_ICRP
  name = G4_BRAIN_ICRP
  specific = 4
FEATURE [App::DocumentObjectGroupPython] C_element019  label="C_element : 4"  # scripted group (container) (typed FeaturePython)
  n = 4
  ref = C_element
FEATURE [App::DocumentObjectGroupPython] H_element018  label="H_element : 010"  # scripted group (container) (typed FeaturePython)
  n = 10
  ref = H_element
FEATURE [App::DocumentObjectGroupPython] G4_BUTANE  # scripted group (container) (typed FeaturePython)
  Dunit = g/cm3
  Dvalue = 0.00249343
  Group = -> [C_element019,H_element018]
  conduct = 2
  density = 1
  expand = 3
  formula = G4_BUTANE
  name = G4_BUTANE
  specific = 4
FEATURE [App::DocumentObjectGroupPython] C_element020  label="C_element : 008"  # scripted group (container) (typed FeaturePython)
  n = 4
  ref = C_element
FEATURE [App::DocumentObjectGroupPython] H_element019  label="H_element : 011"  # scripted group (container) (typed FeaturePython)
  n = 10
  ref = H_element
FEATURE [App::DocumentObjectGroupPython] O_element018  label="O_element : 007"  # scripted group (container) (typed FeaturePython)
  n = 1
  ref = O_element
FEATURE [App::DocumentObjectGroupPython] G4_N_BUTYL_ALCOHOL  label="G4_N-BUTYL_ALCOHOL"  # scripted group (container) (typed FeaturePython)
  Dunit = g/cm3
  Dvalue = 0.8098
  Group = -> [C_element020,H_element019,O_element018]
  conduct = 2
  density = 1
  expand = 3
  formula = G4_N-BUTYL_ALCOHOL
  name = G4_N-BUTYL_ALCOHOL
  specific = 4
FEATURE [App::DocumentObjectGroupPython] H_element020  label="H_element : 0.025"  # scripted group (container) (typed FeaturePython)
  n = 0.02468
FEATURE [App::DocumentObjectGroupPython] C_element021  label="C_element : 0.502"  # scripted group (container) (typed FeaturePython)
  n = 0.501611
FEATURE [App::DocumentObjectGroupPython] O_element019  label="O_element : 0.005"  # scripted group (container) (typed FeaturePython)
  n = 0.004527
FEATURE [App::DocumentObjectGroupPython] F_element004  label="F_element : 0.465"  # scripted group (container) (typed FeaturePython)
  n = 0.465209
FEATURE [App::DocumentObjectGroupPython] Si_element001  label="Si_element : 0.004"  # scripted group (container) (typed FeaturePython)
  n = 0.003973
FEATURE [App::DocumentObjectGroupPython] G4_C_552  label="G4_C-552"  # scripted group (container) (typed FeaturePython)
  Dunit = g/cm3
  Dvalue = 1.76
  Group = -> [H_element020,C_element021,O_element019,F_element004,Si_element001]
  conduct = 2
  density = 1
  expand = 3
  formula = G4_C-552
  name = G4_C-552
  specific = 4
FEATURE [App::DocumentObjectGroupPython] Cd_element001  label="Cd_element : 1"  # scripted group (container) (typed FeaturePython)
  n = 1
  ref = Cd_element
FEATURE [App::DocumentObjectGroupPython] Te_element001  label="Te_element : 1"  # scripted group (container) (typed FeaturePython)
  n = 1
  ref = Te_element
FEATURE [App::DocumentObjectGroupPython] G4_CADMIUM_TELLURIDE  # scripted group (container) (typed FeaturePython)
  Dunit = g/cm3
  Dvalue = 6.2
  Group = -> [Cd_element001,Te_element001]
  conduct = 2
  density = 1
  expand = 3
  formula = G4_CADMIUM_TELLURIDE
  name = G4_CADMIUM_TELLURIDE
  specific = 4
FEATURE [App::DocumentObjectGroupPython] Cd_element002  label="Cd_element : 002"  # scripted group (container) (typed FeaturePython)
  n = 1
  ref = Cd_element
FEATURE [App::DocumentObjectGroupPython] W_element001  label="W_element : 1"  # scripted group (container) (typed FeaturePython)
  n = 1
  ref = W_element
FEATURE [App::DocumentObjectGroupPython] O_element020  label="O_element : 008"  # scripted group (container) (typed FeaturePython)
  n = 4
  ref = O_element
FEATURE [App::DocumentObjectGroupPython] G4_CADMIUM_TUNGSTATE  # scripted group (container) (typed FeaturePython)
  Dunit = g/cm3
  Dvalue = 7.9
  Group = -> [Cd_element002,W_element001,O_element020]
  conduct = 2
  density = 1
  expand = 3
  formula = G4_CADMIUM_TUNGSTATE
  name = G4_CADMIUM_TUNGSTATE
  specific = 4
FEATURE [App::DocumentObjectGroupPython] Ca_element005  label="Ca_element : 1"  # scripted group (container) (typed FeaturePython)
  n = 1
  ref = Ca_element
FEATURE [App::DocumentObjectGroupPython] C_element022  label="C_element : 009"  # scripted group (container) (typed FeaturePython)
  n = 1
  ref = C_element
FEATURE [App::DocumentObjectGroupPython] O_element021  label="O_element : 009"  # scripted group (container) (typed FeaturePython)
  n = 3
  ref = O_element
FEATURE [App::DocumentObjectGroupPython] G4_CALCIUM_CARBONATE  # scripted group (container) (typed FeaturePython)
  Dunit = g/cm3
  Dvalue = 2.8
  Group = -> [Ca_element005,C_element022,O_element021]
  conduct = 2
  density = 1
  expand = 3
  formula = G4_CALCIUM_CARBONATE
  name = G4_CALCIUM_CARBONATE
  specific = 4
FEATURE [App::DocumentObjectGroupPython] Ca_element006  label="Ca_element : 002"  # scripted group (container) (typed FeaturePython)
  n = 1
  ref = Ca_element
FEATURE [App::DocumentObjectGroupPython] F_element005  label="F_element : 003"  # scripted group (container) (typed FeaturePython)
  n = 2
  ref = F_element
FEATURE [App::DocumentObjectGroupPython] G4_CALCIUM_FLUORIDE  # scripted group (container) (typed FeaturePython)
  Dunit = g/cm3
  Dvalue = 3.18
  Group = -> [Ca_element006,F_element005]
  conduct = 2
  density = 1
  expand = 3
  formula = G4_CALCIUM_FLUORIDE
  name = G4_CALCIUM_FLUORIDE
  specific = 4
FEATURE [App::DocumentObjectGroupPython] Ca_element007  label="Ca_element : 003"  # scripted group (container) (typed FeaturePython)
  n = 1
  ref = Ca_element
FEATURE [App::DocumentObjectGroupPython] O_element022  label="O_element : 010"  # scripted group (container) (typed FeaturePython)
  n = 1
  ref = O_element
FEATURE [App::DocumentObjectGroupPython] G4_CALCIUM_OXIDE  # scripted group (container) (typed FeaturePython)
  Dunit = g/cm3
  Dvalue = 3.3
  Group = -> [Ca_element007,O_element022]
  conduct = 2
  density = 1
  expand = 3
  formula = G4_CALCIUM_OXIDE
  name = G4_CALCIUM_OXIDE
  specific = 4
FEATURE [App::DocumentObjectGroupPython] Ca_element008  label="Ca_element : 004"  # scripted group (container) (typed FeaturePython)
  n = 1
  ref = Ca_element
FEATURE [App::DocumentObjectGroupPython] S_element007  label="S_element : 002"  # scripted group (container) (typed FeaturePython)
  n = 1
  ref = S_element
FEATURE [App::DocumentObjectGroupPython] O_element023  label="O_element : 011"  # scripted group (container) (typed FeaturePython)
  n = 4
  ref = O_element
FEATURE [App::DocumentObjectGroupPython] G4_CALCIUM_SULFATE  # scripted group (container) (typed FeaturePython)
  Dunit = g/cm3
  Dvalue = 2.96
  Group = -> [Ca_element008,S_element007,O_element023]
  conduct = 2
  density = 1
  expand = 3
  formula = G4_CALCIUM_SULFATE
  name = G4_CALCIUM_SULFATE
  specific = 4
FEATURE [App::DocumentObjectGroupPython] Ca_element009  label="Ca_element : 005"  # scripted group (container) (typed FeaturePython)
  n = 1
  ref = Ca_element
FEATURE [App::DocumentObjectGroupPython] W_element002  label="W_element : 002"  # scripted group (container) (typed FeaturePython)
  n = 1
  ref = W_element
FEATURE [App::DocumentObjectGroupPython] O_element024  label="O_element : 012"  # scripted group (container) (typed FeaturePython)
  n = 4
  ref = O_element
FEATURE [App::DocumentObjectGroupPython] G4_CALCIUM_TUNGSTATE  # scripted group (container) (typed FeaturePython)
  Dunit = g/cm3
  Dvalue = 6.062
  Group = -> [Ca_element009,W_element002,O_element024]
  conduct = 2
  density = 1
  expand = 3
  formula = G4_CALCIUM_TUNGSTATE
  name = G4_CALCIUM_TUNGSTATE
  specific = 4
FEATURE [App::DocumentObjectGroupPython] C_element023  label="C_element : 010"  # scripted group (container) (typed FeaturePython)
  n = 1
  ref = C_element
FEATURE [App::DocumentObjectGroupPython] O_element025  label="O_element : 013"  # scripted group (container) (typed FeaturePython)
  n = 2
  ref = O_element
FEATURE [App::DocumentObjectGroupPython] G4_CARBON_DIOXIDE  # scripted group (container) (typed FeaturePython)
  Dunit = g/cm3
  Dvalue = 0.00184212
  Group = -> [C_element023,O_element025]
  conduct = 2
  density = 1
  expand = 3
  formula = G4_CARBON_DIOXIDE
  name = G4_CARBON_DIOXIDE
  specific = 4
FEATURE [App::DocumentObjectGroupPython] C_element024  label="C_element : 011"  # scripted group (container) (typed FeaturePython)
  n = 1
  ref = C_element
FEATURE [App::DocumentObjectGroupPython] Cl_element004  label="Cl_element : 4"  # scripted group (container) (typed FeaturePython)
  n = 4
  ref = Cl_element
FEATURE [App::DocumentObjectGroupPython] G4_CARBON_TETRACHLORIDE  # scripted group (container) (typed FeaturePython)
  Dunit = g/cm3
  Dvalue = 1.594
  Group = -> [C_element024,Cl_element004]
  conduct = 2
  density = 1
  expand = 3
  formula = G4_CARBON_TETRACHLORIDE
  name = G4_CARBON_TETRACHLORIDE
  specific = 4
FEATURE [App::DocumentObjectGroupPython] C_element025  label="C_element : 012"  # scripted group (container) (typed FeaturePython)
  n = 6
  ref = C_element
FEATURE [App::DocumentObjectGroupPython] H_element021  label="H_element : 012"  # scripted group (container) (typed FeaturePython)
  n = 10
  ref = H_element
FEATURE [App::DocumentObjectGroupPython] O_element026  label="O_element : 5"  # scripted group (container) (typed FeaturePython)
  n = 5
  ref = O_element
FEATURE [App::DocumentObjectGroupPython] G4_CELLULOSE_CELLOPHANE  # scripted group (container) (typed FeaturePython)
  Dunit = g/cm3
  Dvalue = 1.42
  Group = -> [C_element025,H_element021,O_element026]
  conduct = 2
  density = 1
  expand = 3
  formula = G4_CELLULOSE_CELLOPHANE
  name = G4_CELLULOSE_CELLOPHANE
  specific = 4
FEATURE [App::DocumentObjectGroupPython] H_element022  label="H_element : 0.067"  # scripted group (container) (typed FeaturePython)
  n = 0.067125
FEATURE [App::DocumentObjectGroupPython] C_element026  label="C_element : 0.545"  # scripted group (container) (typed FeaturePython)
  n = 0.545403
FEATURE [App::DocumentObjectGroupPython] O_element027  label="O_element : 0.387"  # scripted group (container) (typed FeaturePython)
  n = 0.387472
FEATURE [App::DocumentObjectGroupPython] G4_CELLULOSE_BUTYRATE  # scripted group (container) (typed FeaturePython)
  Dunit = g/cm3
  Dvalue = 1.2
  Group = -> [H_element022,C_element026,O_element027]
  conduct = 2
  density = 1
  expand = 3
  formula = G4_CELLULOSE_BUTYRATE
  name = G4_CELLULOSE_BUTYRATE
  specific = 4
FEATURE [App::DocumentObjectGroupPython] H_element023  label="H_element : 0.029"  # scripted group (container) (typed FeaturePython)
  n = 0.029216
FEATURE [App::DocumentObjectGroupPython] C_element027  label="C_element : 0.271"  # scripted group (container) (typed FeaturePython)
  n = 0.271296
FEATURE [App::DocumentObjectGroupPython] N_element013  label="N_element : 0.121"  # scripted group (container) (typed FeaturePython)
  n = 0.121276
FEATURE [App::DocumentObjectGroupPython] O_element028  label="O_element : 0.578"  # scripted group (container) (typed FeaturePython)
  n = 0.578212
FEATURE [App::DocumentObjectGroupPython] G4_CELLULOSE_NITRATE  # scripted group (container) (typed FeaturePython)
  Dunit = g/cm3
  Dvalue = 1.49
  Group = -> [H_element023,C_element027,N_element013,O_element028]
  conduct = 2
  density = 1
  expand = 3
  formula = G4_CELLULOSE_NITRATE
  name = G4_CELLULOSE_NITRATE
  specific = 4
FEATURE [App::DocumentObjectGroupPython] H_element024  label="H_element : 0.108"  # scripted group (container) (typed FeaturePython)
  n = 0.107596
FEATURE [App::DocumentObjectGroupPython] N_element014  label="N_element : 0.001"  # scripted group (container) (typed FeaturePython)
  n = 0.0008
FEATURE [App::DocumentObjectGroupPython] O_element029  label="O_element : 0.875"  # scripted group (container) (typed FeaturePython)
  n = 0.874976
FEATURE [App::DocumentObjectGroupPython] S_element008  label="S_element : 0.015"  # scripted group (container) (typed FeaturePython)
  n = 0.014627
FEATURE [App::DocumentObjectGroupPython] Ce_element001  label="Ce_element : 0.002"  # scripted group (container) (typed FeaturePython)
  n = 0.002001
FEATURE [App::DocumentObjectGroupPython] G4_CERIC_SULFATE  # scripted group (container) (typed FeaturePython)
  Dunit = g/cm3
  Dvalue = 1.03
  Group = -> [H_element024,N_element014,O_element029,S_element008,Ce_element001]
  conduct = 2
  density = 1
  expand = 3
  formula = G4_CERIC_SULFATE
  name = G4_CERIC_SULFATE
  specific = 4
FEATURE [App::DocumentObjectGroupPython] Cs_element001  label="Cs_element : 1"  # scripted group (container) (typed FeaturePython)
  n = 1
  ref = Cs_element
FEATURE [App::DocumentObjectGroupPython] F_element006  label="F_element : 1"  # scripted group (container) (typed FeaturePython)
  n = 1
  ref = F_element
FEATURE [App::DocumentObjectGroupPython] G4_CESIUM_FLUORIDE  # scripted group (container) (typed FeaturePython)
  Dunit = g/cm3
  Dvalue = 4.115
  Group = -> [Cs_element001,F_element006]
  conduct = 2
  density = 1
  expand = 3
  formula = G4_CESIUM_FLUORIDE
  name = G4_CESIUM_FLUORIDE
  specific = 4
FEATURE [App::DocumentObjectGroupPython] Cs_element002  label="Cs_element : 002"  # scripted group (container) (typed FeaturePython)
  n = 1
  ref = Cs_element
FEATURE [App::DocumentObjectGroupPython] I_element001  label="I_element : 1"  # scripted group (container) (typed FeaturePython)
  n = 1
  ref = I_element
FEATURE [App::DocumentObjectGroupPython] G4_CESIUM_IODIDE  # scripted group (container) (typed FeaturePython)
  Dunit = g/cm3
  Dvalue = 4.51
  Group = -> [Cs_element002,I_element001]
  conduct = 2
  density = 1
  expand = 3
  formula = G4_CESIUM_IODIDE
  name = G4_CESIUM_IODIDE
  specific = 4
FEATURE [App::DocumentObjectGroupPython] C_element028  label="C_element : 013"  # scripted group (container) (typed FeaturePython)
  n = 6
  ref = C_element
FEATURE [App::DocumentObjectGroupPython] H_element025  label="H_element : 013"  # scripted group (container) (typed FeaturePython)
  n = 5
  ref = H_element
FEATURE [App::DocumentObjectGroupPython] Cl_element005  label="Cl_element : 1"  # scripted group (container) (typed FeaturePython)
  n = 1
  ref = Cl_element
FEATURE [App::DocumentObjectGroupPython] G4_CHLOROBENZENE  # scripted group (container) (typed FeaturePython)
  Dunit = g/cm3
  Dvalue = 1.1058
  Group = -> [C_element028,H_element025,Cl_element005]
  conduct = 2
  density = 1
  expand = 3
  formula = G4_CHLOROBENZENE
  name = G4_CHLOROBENZENE
  specific = 4
FEATURE [App::DocumentObjectGroupPython] C_element029  label="C_element : 014"  # scripted group (container) (typed FeaturePython)
  n = 1
  ref = C_element
FEATURE [App::DocumentObjectGroupPython] H_element026  label="H_element : 1"  # scripted group (container) (typed FeaturePython)
  n = 1
  ref = H_element
FEATURE [App::DocumentObjectGroupPython] Cl_element006  label="Cl_element : 3"  # scripted group (container) (typed FeaturePython)
  n = 3
  ref = Cl_element
FEATURE [App::DocumentObjectGroupPython] G4_CHLOROFORM  # scripted group (container) (typed FeaturePython)
  Dunit = g/cm3
  Dvalue = 1.4832
  Group = -> [C_element029,H_element026,Cl_element006]
  conduct = 2
  density = 1
  expand = 3
  formula = G4_CHLOROFORM
  name = G4_CHLOROFORM
  specific = 4
FEATURE [App::DocumentObjectGroupPython] H_element027  label="H_element : 0.010"  # scripted group (container) (typed FeaturePython)
  n = 0.01
FEATURE [App::DocumentObjectGroupPython] C_element030  label="C_element : 0.001"  # scripted group (container) (typed FeaturePython)
  n = 0.001
FEATURE [App::DocumentObjectGroupPython] O_element030  label="O_element : 0.529"  # scripted group (container) (typed FeaturePython)
  n = 0.529107
FEATURE [App::DocumentObjectGroupPython] Na_element005  label="Na_element : 0.016"  # scripted group (container) (typed FeaturePython)
  n = 0.016
FEATURE [App::DocumentObjectGroupPython] Mg_element003  label="Mg_element : 0.004"  # scripted group (container) (typed FeaturePython)
  n = 0.002
FEATURE [App::DocumentObjectGroupPython] Al_element002  label="Al_element : 0.034"  # scripted group (container) (typed FeaturePython)
  n = 0.033872
FEATURE [App::DocumentObjectGroupPython] Si_element002  label="Si_element : 0.337"  # scripted group (container) (typed FeaturePython)
  n = 0.337021
FEATURE [App::DocumentObjectGroupPython] K_element003  label="K_element : 0.013"  # scripted group (container) (typed FeaturePython)
  n = 0.013
FEATURE [App::DocumentObjectGroupPython] Ca_element010  label="Ca_element : 0.044"  # scripted group (container) (typed FeaturePython)
  n = 0.044
FEATURE [App::DocumentObjectGroupPython] Fe_element002  label="Fe_element : 0.014"  # scripted group (container) (typed FeaturePython)
  n = 0.014
FEATURE [App::DocumentObjectGroupPython] G4_CONCRETE  # scripted group (container) (typed FeaturePython)
  Dunit = g/cm3
  Dvalue = 2.3
  Group = -> [H_element027,C_element030,O_element030,Na_element005,Mg_element003,Al_element002,Si_element002,K_element003,Ca_element010,Fe_element002]
  conduct = 2
  density = 1
  expand = 3
  formula = G4_CONCRETE
  name = G4_CONCRETE
  specific = 4
FEATURE [App::DocumentObjectGroupPython] C_element031  label="C_element : 015"  # scripted group (container) (typed FeaturePython)
  n = 6
  ref = C_element
FEATURE [App::DocumentObjectGroupPython] H_element028  label="H_element : 12"  # scripted group (container) (typed FeaturePython)
  n = 12
  ref = H_element
FEATURE [App::DocumentObjectGroupPython] G4_CYCLOHEXANE  # scripted group (container) (typed FeaturePython)
  Dunit = g/cm3
  Dvalue = 0.779
  Group = -> [C_element031,H_element028]
  conduct = 2
  density = 1
  expand = 3
  formula = G4_CYCLOHEXANE
  name = G4_CYCLOHEXANE
  specific = 4
FEATURE [App::DocumentObjectGroupPython] C_element032  label="C_element : 016"  # scripted group (container) (typed FeaturePython)
  n = 6
  ref = C_element
FEATURE [App::DocumentObjectGroupPython] H_element029  label="H_element : 4"  # scripted group (container) (typed FeaturePython)
  n = 4
  ref = H_element
FEATURE [App::DocumentObjectGroupPython] Cl_element007  label="Cl_element : 2"  # scripted group (container) (typed FeaturePython)
  n = 2
  ref = Cl_element
FEATURE [App::DocumentObjectGroupPython] G4_1_2_DICHLOROBENZENE  label="G4_1.2-DICHLOROBENZENE"  # scripted group (container) (typed FeaturePython)
  Dunit = g/cm3
  Dvalue = 1.3048
  Group = -> [C_element032,H_element029,Cl_element007]
  conduct = 2
  density = 1
  expand = 3
  formula = G4_1.2-DICHLOROBENZENE
  name = G4_1.2-DICHLOROBENZENE
  specific = 4
FEATURE [App::DocumentObjectGroupPython] C_element033  label="C_element : 017"  # scripted group (container) (typed FeaturePython)
  n = 4
  ref = C_element
FEATURE [App::DocumentObjectGroupPython] H_element030  label="H_element : 8"  # scripted group (container) (typed FeaturePython)
  n = 8
  ref = H_element
FEATURE [App::DocumentObjectGroupPython] O_element031  label="O_element : 014"  # scripted group (container) (typed FeaturePython)
  n = 1
  ref = O_element
FEATURE [App::DocumentObjectGroupPython] Cl_element008  label="Cl_element : 005"  # scripted group (container) (typed FeaturePython)
  n = 2
  ref = Cl_element
FEATURE [App::DocumentObjectGroupPython] G4_DICHLORODIETHYL_ETHER  # scripted group (container) (typed FeaturePython)
  Dunit = g/cm3
  Dvalue = 1.2199
  Group = -> [C_element033,H_element030,O_element031,Cl_element008]
  conduct = 2
  density = 1
  expand = 3
  formula = G4_DICHLORODIETHYL_ETHER
  name = G4_DICHLORODIETHYL_ETHER
  specific = 4
FEATURE [App::DocumentObjectGroupPython] C_element034  label="C_element : 018"  # scripted group (container) (typed FeaturePython)
  n = 2
  ref = C_element
FEATURE [App::DocumentObjectGroupPython] H_element031  label="H_element : 014"  # scripted group (container) (typed FeaturePython)
  n = 4
  ref = H_element
FEATURE [App::DocumentObjectGroupPython] Cl_element009  label="Cl_element : 006"  # scripted group (container) (typed FeaturePython)
  n = 2
  ref = Cl_element
FEATURE [App::DocumentObjectGroupPython] G4_1_2_DICHLOROETHANE  label="G4_1.2-DICHLOROETHANE"  # scripted group (container) (typed FeaturePython)
  Dunit = g/cm3
  Dvalue = 1.2351
  Group = -> [C_element034,H_element031,Cl_element009]
  conduct = 2
  density = 1
  expand = 3
  formula = G4_1.2-DICHLOROETHANE
  name = G4_1.2-DICHLOROETHANE
  specific = 4
FEATURE [App::DocumentObjectGroupPython] C_element035  label="C_element : 019"  # scripted group (container) (typed FeaturePython)
  n = 4
  ref = C_element
FEATURE [App::DocumentObjectGroupPython] H_element032  label="H_element : 015"  # scripted group (container) (typed FeaturePython)
  n = 10
  ref = H_element
FEATURE [App::DocumentObjectGroupPython] O_element032  label="O_element : 015"  # scripted group (container) (typed FeaturePython)
  n = 1
  ref = O_element
FEATURE [App::DocumentObjectGroupPython] G4_DIETHYL_ETHER  # scripted group (container) (typed FeaturePython)
  Dunit = g/cm3
  Dvalue = 0.71378
  Group = -> [C_element035,H_element032,O_element032]
  conduct = 2
  density = 1
  expand = 3
  formula = G4_DIETHYL_ETHER
  name = G4_DIETHYL_ETHER
  specific = 4
FEATURE [App::DocumentObjectGroupPython] C_element036  label="C_element : 020"  # scripted group (container) (typed FeaturePython)
  n = 3
  ref = C_element
FEATURE [App::DocumentObjectGroupPython] H_element033  label="H_element : 016"  # scripted group (container) (typed FeaturePython)
  n = 7
  ref = H_element
FEATURE [App::DocumentObjectGroupPython] N_element015  label="N_element : 008"  # scripted group (container) (typed FeaturePython)
  n = 1
  ref = N_element
FEATURE [App::DocumentObjectGroupPython] O_element033  label="O_element : 016"  # scripted group (container) (typed FeaturePython)
  n = 1
  ref = O_element
FEATURE [App::DocumentObjectGroupPython] G4_N_N_DIMETHYL_FORMAMIDE  label="G4_N.N-DIMETHYL_FORMAMIDE"  # scripted group (container) (typed FeaturePython)
  Dunit = g/cm3
  Dvalue = 0.9487
  Group = -> [C_element036,H_element033,N_element015,O_element033]
  conduct = 2
  density = 1
  expand = 3
  formula = G4_N.N-DIMETHYL_FORMAMIDE
  name = G4_N.N-DIMETHYL_FORMAMIDE
  specific = 4
FEATURE [App::DocumentObjectGroupPython] C_element037  label="C_element : 021"  # scripted group (container) (typed FeaturePython)
  n = 2
  ref = C_element
FEATURE [App::DocumentObjectGroupPython] H_element034  label="H_element : 017"  # scripted group (container) (typed FeaturePython)
  n = 6
  ref = H_element
FEATURE [App::DocumentObjectGroupPython] O_element034  label="O_element : 017"  # scripted group (container) (typed FeaturePython)
  n = 1
  ref = O_element
FEATURE [App::DocumentObjectGroupPython] S_element009  label="S_element : 003"  # scripted group (container) (typed FeaturePython)
  n = 1
  ref = S_element
FEATURE [App::DocumentObjectGroupPython] G4_DIMETHYL_SULFOXIDE  # scripted group (container) (typed FeaturePython)
  Dunit = g/cm3
  Dvalue = 1.1014
  Group = -> [C_element037,H_element034,O_element034,S_element009]
  conduct = 2
  density = 1
  expand = 3
  formula = G4_DIMETHYL_SULFOXIDE
  name = G4_DIMETHYL_SULFOXIDE
  specific = 4
FEATURE [App::DocumentObjectGroupPython] C_element038  label="C_element : 022"  # scripted group (container) (typed FeaturePython)
  n = 2
  ref = C_element
FEATURE [App::DocumentObjectGroupPython] H_element035  label="H_element : 018"  # scripted group (container) (typed FeaturePython)
  n = 6
  ref = H_element
FEATURE [App::DocumentObjectGroupPython] G4_ETHANE  # scripted group (container) (typed FeaturePython)
  Dunit = g/cm3
  Dvalue = 0.00125324
  Group = -> [C_element038,H_element035]
  conduct = 2
  density = 1
  expand = 3
  formula = G4_ETHANE
  name = G4_ETHANE
  specific = 4
FEATURE [App::DocumentObjectGroupPython] C_element039  label="C_element : 023"  # scripted group (container) (typed FeaturePython)
  n = 2
  ref = C_element
FEATURE [App::DocumentObjectGroupPython] H_element036  label="H_element : 019"  # scripted group (container) (typed FeaturePython)
  n = 6
  ref = H_element
FEATURE [App::DocumentObjectGroupPython] O_element035  label="O_element : 018"  # scripted group (container) (typed FeaturePython)
  n = 1
  ref = O_element
FEATURE [App::DocumentObjectGroupPython] G4_ETHYL_ALCOHOL  # scripted group (container) (typed FeaturePython)
  Dunit = g/cm3
  Dvalue = 0.7893
  Group = -> [C_element039,H_element036,O_element035]
  conduct = 2
  density = 1
  expand = 3
  formula = G4_ETHYL_ALCOHOL
  name = G4_ETHYL_ALCOHOL
  specific = 4
FEATURE [App::DocumentObjectGroupPython] H_element037  label="H_element : 0.090"  # scripted group (container) (typed FeaturePython)
  n = 0.090027
FEATURE [App::DocumentObjectGroupPython] C_element040  label="C_element : 0.585"  # scripted group (container) (typed FeaturePython)
  n = 0.585182
FEATURE [App::DocumentObjectGroupPython] O_element036  label="O_element : 0.325"  # scripted group (container) (typed FeaturePython)
  n = 0.324791
FEATURE [App::DocumentObjectGroupPython] G4_ETHYL_CELLULOSE  # scripted group (container) (typed FeaturePython)
  Dunit = g/cm3
  Dvalue = 1.13
  Group = -> [H_element037,C_element040,O_element036]
  conduct = 2
  density = 1
  expand = 3
  formula = G4_ETHYL_CELLULOSE
  name = G4_ETHYL_CELLULOSE
  specific = 4
FEATURE [App::DocumentObjectGroupPython] C_element041  label="C_element : 024"  # scripted group (container) (typed FeaturePython)
  n = 2
  ref = C_element
FEATURE [App::DocumentObjectGroupPython] H_element038  label="H_element : 020"  # scripted group (container) (typed FeaturePython)
  n = 4
  ref = H_element
FEATURE [App::DocumentObjectGroupPython] G4_ETHYLENE  # scripted group (container) (typed FeaturePython)
  Dunit = g/cm3
  Dvalue = 0.00117497
  Group = -> [C_element041,H_element038]
  conduct = 2
  density = 1
  expand = 3
  formula = G4_ETHYLENE
  name = G4_ETHYLENE
  specific = 4
FEATURE [App::DocumentObjectGroupPython] H_element039  label="H_element : 0.096"  # scripted group (container) (typed FeaturePython)
  n = 0.096
FEATURE [App::DocumentObjectGroupPython] C_element042  label="C_element : 0.195"  # scripted group (container) (typed FeaturePython)
  n = 0.195
FEATURE [App::DocumentObjectGroupPython] N_element016  label="N_element : 0.057"  # scripted group (container) (typed FeaturePython)
  n = 0.057
FEATURE [App::DocumentObjectGroupPython] O_element037  label="O_element : 0.646"  # scripted group (container) (typed FeaturePython)
  n = 0.646
FEATURE [App::DocumentObjectGroupPython] Na_element006  label="Na_element : 0.017"  # scripted group (container) (typed FeaturePython)
  n = 0.001
FEATURE [App::DocumentObjectGroupPython] P_element005  label="P_element : 0.104"  # scripted group (container) (typed FeaturePython)
  n = 0.001
FEATURE [App::DocumentObjectGroupPython] S_element010  label="S_element : 0.016"  # scripted group (container) (typed FeaturePython)
  n = 0.003
FEATURE [App::DocumentObjectGroupPython] Cl_element010  label="Cl_element : 0.005"  # scripted group (container) (typed FeaturePython)
  n = 0.001
FEATURE [App::DocumentObjectGroupPython] G4_EYE_LENS_ICRP  # scripted group (container) (typed FeaturePython)
  Dunit = g/cm3
  Dvalue = 1.07
  Group = -> [H_element039,C_element042,N_element016,O_element037,Na_element006,P_element005,S_element010,Cl_element010]
  conduct = 2
  density = 1
  expand = 3
  formula = G4_EYE_LENS_ICRP
  name = G4_EYE_LENS_ICRP
  specific = 4
FEATURE [App::DocumentObjectGroupPython] Fe_element003  label="Fe_element : 2"  # scripted group (container) (typed FeaturePython)
  n = 2
  ref = Fe_element
FEATURE [App::DocumentObjectGroupPython] O_element038  label="O_element : 019"  # scripted group (container) (typed FeaturePython)
  n = 3
  ref = O_element
FEATURE [App::DocumentObjectGroupPython] G4_FERRIC_OXIDE  # scripted group (container) (typed FeaturePython)
  Dunit = g/cm3
  Dvalue = 5.2
  Group = -> [Fe_element003,O_element038]
  conduct = 2
  density = 1
  expand = 3
  formula = G4_FERRIC_OXIDE
  name = G4_FERRIC_OXIDE
  specific = 4
FEATURE [App::DocumentObjectGroupPython] Fe_element004  label="Fe_element : 1"  # scripted group (container) (typed FeaturePython)
  n = 1
  ref = Fe_element
FEATURE [App::DocumentObjectGroupPython] B_element003  label="B_element : 1"  # scripted group (container) (typed FeaturePython)
  n = 1
  ref = B_element
FEATURE [App::DocumentObjectGroupPython] G4_FERROBORIDE  # scripted group (container) (typed FeaturePython)
  Dunit = g/cm3
  Dvalue = 7.15
  Group = -> [Fe_element004,B_element003]
  conduct = 2
  density = 1
  expand = 3
  formula = G4_FERROBORIDE
  name = G4_FERROBORIDE
  specific = 4
FEATURE [App::DocumentObjectGroupPython] Fe_element005  label="Fe_element : 003"  # scripted group (container) (typed FeaturePython)
  n = 1
  ref = Fe_element
FEATURE [App::DocumentObjectGroupPython] O_element039  label="O_element : 020"  # scripted group (container) (typed FeaturePython)
  n = 1
  ref = O_element
FEATURE [App::DocumentObjectGroupPython] G4_FERROUS_OXIDE  # scripted group (container) (typed FeaturePython)
  Dunit = g/cm3
  Dvalue = 5.7
  Group = -> [Fe_element005,O_element039]
  conduct = 2
  density = 1
  expand = 3
  formula = G4_FERROUS_OXIDE
  name = G4_FERROUS_OXIDE
  specific = 4
FEATURE [App::DocumentObjectGroupPython] H_element040  label="H_element : 0.115"  # scripted group (container) (typed FeaturePython)
  n = 0.108259
FEATURE [App::DocumentObjectGroupPython] N_element017  label="N_element : 0.000"  # scripted group (container) (typed FeaturePython)
  n = 2.7e-05
FEATURE [App::DocumentObjectGroupPython] O_element040  label="O_element : 0.879"  # scripted group (container) (typed FeaturePython)
  n = 0.878636
FEATURE [App::DocumentObjectGroupPython] Na_element007  label="Na_element : 0.000"  # scripted group (container) (typed FeaturePython)
  n = 2.2e-05
FEATURE [App::DocumentObjectGroupPython] S_element011  label="S_element : 0.013"  # scripted group (container) (typed FeaturePython)
  n = 0.012968
FEATURE [App::DocumentObjectGroupPython] Cl_element011  label="Cl_element : 0.000"  # scripted group (container) (typed FeaturePython)
  n = 3.4e-05
FEATURE [App::DocumentObjectGroupPython] Fe_element006  label="Fe_element : 0.000"  # scripted group (container) (typed FeaturePython)
  n = 5.4e-05
FEATURE [App::DocumentObjectGroupPython] G4_FERROUS_SULFATE  # scripted group (container) (typed FeaturePython)
  Dunit = g/cm3
  Dvalue = 1.024
  Group = -> [H_element040,N_element017,O_element040,Na_element007,S_element011,Cl_element011,Fe_element006]
  conduct = 2
  density = 1
  expand = 3
  formula = G4_FERROUS_SULFATE
  name = G4_FERROUS_SULFATE
  specific = 4
FEATURE [App::DocumentObjectGroupPython] C_element043  label="C_element : 0.099"  # scripted group (container) (typed FeaturePython)
  n = 0.099335
FEATURE [App::DocumentObjectGroupPython] F_element007  label="F_element : 0.314"  # scripted group (container) (typed FeaturePython)
  n = 0.314247
FEATURE [App::DocumentObjectGroupPython] Cl_element012  label="Cl_element : 0.586"  # scripted group (container) (typed FeaturePython)
  n = 0.586418
FEATURE [App::DocumentObjectGroupPython] G4_FREON_12  label="G4_FREON-12"  # scripted group (container) (typed FeaturePython)
  Dunit = g/cm3
  Dvalue = 1.12
  Group = -> [C_element043,F_element007,Cl_element012]
  conduct = 2
  density = 1
  expand = 3
  formula = G4_FREON-12
  name = G4_FREON-12
  specific = 4
FEATURE [App::DocumentObjectGroupPython] C_element044  label="C_element : 0.057"  # scripted group (container) (typed FeaturePython)
  n = 0.057245
FEATURE [App::DocumentObjectGroupPython] F_element008  label="F_element : 0.181"  # scripted group (container) (typed FeaturePython)
  n = 0.181096
FEATURE [App::DocumentObjectGroupPython] Br_element001  label="Br_element : 0.762"  # scripted group (container) (typed FeaturePython)
  n = 0.761659
FEATURE [App::DocumentObjectGroupPython] G4_FREON_12B2  label="G4_FREON-12B2"  # scripted group (container) (typed FeaturePython)
  Dunit = g/cm3
  Dvalue = 1.8
  Group = -> [C_element044,F_element008,Br_element001]
  conduct = 2
  density = 1
  expand = 3
  formula = G4_FREON-12B2
  name = G4_FREON-12B2
  specific = 4
FEATURE [App::DocumentObjectGroupPython] C_element045  label="C_element : 0.115"  # scripted group (container) (typed FeaturePython)
  n = 0.114983
FEATURE [App::DocumentObjectGroupPython] F_element009  label="F_element : 0.546"  # scripted group (container) (typed FeaturePython)
  n = 0.545621
FEATURE [App::DocumentObjectGroupPython] Cl_element013  label="Cl_element : 0.339"  # scripted group (container) (typed FeaturePython)
  n = 0.339396
FEATURE [App::DocumentObjectGroupPython] G4_FREON_13  label="G4_FREON-13"  # scripted group (container) (typed FeaturePython)
  Dunit = g/cm3
  Dvalue = 0.95
  Group = -> [C_element045,F_element009,Cl_element013]
  conduct = 2
  density = 1
  expand = 3
  formula = G4_FREON-13
  name = G4_FREON-13
  specific = 4
FEATURE [App::DocumentObjectGroupPython] C_element046  label="C_element : 025"  # scripted group (container) (typed FeaturePython)
  n = 1
  ref = C_element
FEATURE [App::DocumentObjectGroupPython] F_element010  label="F_element : 3"  # scripted group (container) (typed FeaturePython)
  n = 3
  ref = F_element
FEATURE [App::DocumentObjectGroupPython] Br_element002  label="Br_element : 1"  # scripted group (container) (typed FeaturePython)
  n = 1
  ref = Br_element
FEATURE [App::DocumentObjectGroupPython] G4_FREON_13B1  label="G4_FREON-13B1"  # scripted group (container) (typed FeaturePython)
  Dunit = g/cm3
  Dvalue = 1.5
  Group = -> [C_element046,F_element010,Br_element002]
  conduct = 2
  density = 1
  expand = 3
  formula = G4_FREON-13B1
  name = G4_FREON-13B1
  specific = 4
FEATURE [App::DocumentObjectGroupPython] C_element047  label="C_element : 0.061"  # scripted group (container) (typed FeaturePython)
  n = 0.061309
FEATURE [App::DocumentObjectGroupPython] F_element011  label="F_element : 0.291"  # scripted group (container) (typed FeaturePython)
  n = 0.290924
FEATURE [App::DocumentObjectGroupPython] I_element002  label="I_element : 0.648"  # scripted group (container) (typed FeaturePython)
  n = 0.647767
FEATURE [App::DocumentObjectGroupPython] G4_FREON_13I1  label="G4_FREON-13I1"  # scripted group (container) (typed FeaturePython)
  Dunit = g/cm3
  Dvalue = 1.8
  Group = -> [C_element047,F_element011,I_element002]
  conduct = 2
  density = 1
  expand = 3
  formula = G4_FREON-13I1
  name = G4_FREON-13I1
  specific = 4
FEATURE [App::DocumentObjectGroupPython] Gd_element001  label="Gd_element : 2"  # scripted group (container) (typed FeaturePython)
  n = 2
  ref = Gd_element
FEATURE [App::DocumentObjectGroupPython] O_element041  label="O_element : 021"  # scripted group (container) (typed FeaturePython)
  n = 2
  ref = O_element
FEATURE [App::DocumentObjectGroupPython] S_element012  label="S_element : 004"  # scripted group (container) (typed FeaturePython)
  n = 1
  ref = S_element
FEATURE [App::DocumentObjectGroupPython] G4_GADOLINIUM_OXYSULFIDE  # scripted group (container) (typed FeaturePython)
  Dunit = g/cm3
  Dvalue = 7.44
  Group = -> [Gd_element001,O_element041,S_element012]
  conduct = 2
  density = 1
  expand = 3
  formula = G4_GADOLINIUM_OXYSULFIDE
  name = G4_GADOLINIUM_OXYSULFIDE
  specific = 4
FEATURE [App::DocumentObjectGroupPython] Ga_element001  label="Ga_element : 1"  # scripted group (container) (typed FeaturePython)
  n = 1
  ref = Ga_element
FEATURE [App::DocumentObjectGroupPython] As_element001  label="As_element : 1"  # scripted group (container) (typed FeaturePython)
  n = 1
  ref = As_element
FEATURE [App::DocumentObjectGroupPython] G4_GALLIUM_ARSENIDE  # scripted group (container) (typed FeaturePython)
  Dunit = g/cm3
  Dvalue = 5.31
  Group = -> [Ga_element001,As_element001]
  conduct = 2
  density = 1
  expand = 3
  formula = G4_GALLIUM_ARSENIDE
  name = G4_GALLIUM_ARSENIDE
  specific = 4
FEATURE [App::DocumentObjectGroupPython] H_element041  label="H_element : 0.081"  # scripted group (container) (typed FeaturePython)
  n = 0.08118
FEATURE [App::DocumentObjectGroupPython] C_element048  label="C_element : 0.416"  # scripted group (container) (typed FeaturePython)
  n = 0.41606
FEATURE [App::DocumentObjectGroupPython] N_element018  label="N_element : 0.111"  # scripted group (container) (typed FeaturePython)
  n = 0.11124
FEATURE [App::DocumentObjectGroupPython] O_element042  label="O_element : 0.381"  # scripted group (container) (typed FeaturePython)
  n = 0.38064
FEATURE [App::DocumentObjectGroupPython] S_element013  label="S_element : 0.011"  # scripted group (container) (typed FeaturePython)
  n = 0.01088
FEATURE [App::DocumentObjectGroupPython] G4_GEL_PHOTO_EMULSION  # scripted group (container) (typed FeaturePython)
  Dunit = g/cm3
  Dvalue = 1.2914
  Group = -> [H_element041,C_element048,N_element018,O_element042,S_element013]
  conduct = 2
  density = 1
  expand = 3
  formula = G4_GEL_PHOTO_EMULSION
  name = G4_GEL_PHOTO_EMULSION
  specific = 4
FEATURE [App::DocumentObjectGroupPython] B_element004  label="B_element : 0.040"  # scripted group (container) (typed FeaturePython)
  n = 0.0400639
FEATURE [App::DocumentObjectGroupPython] O_element043  label="O_element : 0.540"  # scripted group (container) (typed FeaturePython)
  n = 0.539561
FEATURE [App::DocumentObjectGroupPython] Na_element008  label="Na_element : 0.028"  # scripted group (container) (typed FeaturePython)
  n = 0.0281909
FEATURE [App::DocumentObjectGroupPython] Al_element003  label="Al_element : 0.012"  # scripted group (container) (typed FeaturePython)
  n = 0.011644
FEATURE [App::DocumentObjectGroupPython] Si_element003  label="Si_element : 0.377"  # scripted group (container) (typed FeaturePython)
  n = 0.377219
FEATURE [App::DocumentObjectGroupPython] K_element004  label="K_element : 0.014"  # scripted group (container) (typed FeaturePython)
  n = 0.00332099
FEATURE [App::DocumentObjectGroupPython] G4_Pyrex_Glass  # scripted group (container) (typed FeaturePython)
  Dunit = g/cm3
  Dvalue = 2.23
  Group = -> [B_element004,O_element043,Na_element008,Al_element003,Si_element003,K_element004]
  conduct = 2
  density = 1
  expand = 3
  formula = G4_Pyrex_Glass
  name = G4_Pyrex_Glass
  specific = 4
FEATURE [App::DocumentObjectGroupPython] O_element044  label="O_element : 0.156"  # scripted group (container) (typed FeaturePython)
  n = 0.156453
FEATURE [App::DocumentObjectGroupPython] Si_element004  label="Si_element : 0.081"  # scripted group (container) (typed FeaturePython)
  n = 0.080866
FEATURE [App::DocumentObjectGroupPython] Ti_element001  label="Ti_element : 0.008"  # scripted group (container) (typed FeaturePython)
  n = 0.008092
FEATURE [App::DocumentObjectGroupPython] As_element002  label="As_element : 0.003"  # scripted group (container) (typed FeaturePython)
  n = 0.002651
FEATURE [App::DocumentObjectGroupPython] Pb_element001  label="Pb_element : 0.752"  # scripted group (container) (typed FeaturePython)
  n = 0.751938
FEATURE [App::DocumentObjectGroupPython] G4_GLASS_LEAD  # scripted group (container) (typed FeaturePython)
  Dunit = g/cm3
  Dvalue = 6.22
  Group = -> [O_element044,Si_element004,Ti_element001,As_element002,Pb_element001]
  conduct = 2
  density = 1
  expand = 3
  formula = G4_GLASS_LEAD
  name = G4_GLASS_LEAD
  specific = 4
FEATURE [App::DocumentObjectGroupPython] O_element045  label="O_element : 0.460"  # scripted group (container) (typed FeaturePython)
  n = 0.4598
FEATURE [App::DocumentObjectGroupPython] Na_element009  label="Na_element : 0.096"  # scripted group (container) (typed FeaturePython)
  n = 0.0964411
FEATURE [App::DocumentObjectGroupPython] Si_element005  label="Si_element : 0.378"  # scripted group (container) (typed FeaturePython)
  n = 0.336553
FEATURE [App::DocumentObjectGroupPython] Ca_element011  label="Ca_element : 0.107"  # scripted group (container) (typed FeaturePython)
  n = 0.107205
FEATURE [App::DocumentObjectGroupPython] G4_GLASS_PLATE  # scripted group (container) (typed FeaturePython)
  Dunit = g/cm3
  Dvalue = 2.4
  Group = -> [O_element045,Na_element009,Si_element005,Ca_element011]
  conduct = 2
  density = 1
  expand = 3
  formula = G4_GLASS_PLATE
  name = G4_GLASS_PLATE
  specific = 4
FEATURE [App::DocumentObjectGroupPython] C_element049  label="C_element : 026"  # scripted group (container) (typed FeaturePython)
  n = 5
  ref = C_element
FEATURE [App::DocumentObjectGroupPython] H_element042  label="H_element : 021"  # scripted group (container) (typed FeaturePython)
  n = 10
  ref = H_element
FEATURE [App::DocumentObjectGroupPython] N_element019  label="N_element : 2"  # scripted group (container) (typed FeaturePython)
  n = 2
  ref = N_element
FEATURE [App::DocumentObjectGroupPython] O_element046  label="O_element : 022"  # scripted group (container) (typed FeaturePython)
  n = 3
  ref = O_element
FEATURE [App::DocumentObjectGroupPython] G4_GLUTAMINE  # scripted group (container) (typed FeaturePython)
  Dunit = g/cm3
  Dvalue = 1.46
  Group = -> [C_element049,H_element042,N_element019,O_element046]
  conduct = 2
  density = 1
  expand = 3
  formula = G4_GLUTAMINE
  name = G4_GLUTAMINE
  specific = 4
FEATURE [App::DocumentObjectGroupPython] C_element050  label="C_element : 027"  # scripted group (container) (typed FeaturePython)
  n = 3
  ref = C_element
FEATURE [App::DocumentObjectGroupPython] H_element043  label="H_element : 022"  # scripted group (container) (typed FeaturePython)
  n = 8
  ref = H_element
FEATURE [App::DocumentObjectGroupPython] O_element047  label="O_element : 023"  # scripted group (container) (typed FeaturePython)
  n = 3
  ref = O_element
FEATURE [App::DocumentObjectGroupPython] G4_GLYCEROL  # scripted group (container) (typed FeaturePython)
  Dunit = g/cm3
  Dvalue = 1.2613
  Group = -> [C_element050,H_element043,O_element047]
  conduct = 2
  density = 1
  expand = 3
  formula = G4_GLYCEROL
  name = G4_GLYCEROL
  specific = 4
FEATURE [App::DocumentObjectGroupPython] C_element051  label="C_element : 028"  # scripted group (container) (typed FeaturePython)
  n = 5
  ref = C_element
FEATURE [App::DocumentObjectGroupPython] H_element044  label="H_element : 023"  # scripted group (container) (typed FeaturePython)
  n = 5
  ref = H_element
FEATURE [App::DocumentObjectGroupPython] N_element020  label="N_element : 009"  # scripted group (container) (typed FeaturePython)
  n = 5
  ref = N_element
FEATURE [App::DocumentObjectGroupPython] O_element048  label="O_element : 024"  # scripted group (container) (typed FeaturePython)
  n = 1
  ref = O_element
FEATURE [App::DocumentObjectGroupPython] G4_GUANINE  # scripted group (container) (typed FeaturePython)
  Dunit = g/cm3
  Dvalue = 2.2
  Group = -> [C_element051,H_element044,N_element020,O_element048]
  conduct = 2
  density = 1
  expand = 3
  formula = G4_GUANINE
  name = G4_GUANINE
  specific = 4
FEATURE [App::DocumentObjectGroupPython] Ca_element012  label="Ca_element : 006"  # scripted group (container) (typed FeaturePython)
  n = 1
  ref = Ca_element
FEATURE [App::DocumentObjectGroupPython] S_element014  label="S_element : 005"  # scripted group (container) (typed FeaturePython)
  n = 1
  ref = S_element
FEATURE [App::DocumentObjectGroupPython] O_element049  label="O_element : 6"  # scripted group (container) (typed FeaturePython)
  n = 6
  ref = O_element
FEATURE [App::DocumentObjectGroupPython] H_element045  label="H_element : 024"  # scripted group (container) (typed FeaturePython)
  n = 4
  ref = H_element
FEATURE [App::DocumentObjectGroupPython] G4_GYPSUM  # scripted group (container) (typed FeaturePython)
  Dunit = g/cm3
  Dvalue = 2.32
  Group = -> [Ca_element012,S_element014,O_element049,H_element045]
  conduct = 2
  density = 1
  expand = 3
  formula = G4_GYPSUM
  name = G4_GYPSUM
  specific = 4
FEATURE [App::DocumentObjectGroupPython] C_element052  label="C_element : 7"  # scripted group (container) (typed FeaturePython)
  n = 7
  ref = C_element
FEATURE [App::DocumentObjectGroupPython] H_element046  label="H_element : 16"  # scripted group (container) (typed FeaturePython)
  n = 16
  ref = H_element
FEATURE [App::DocumentObjectGroupPython] G4_N_HEPTANE  label="G4_N-HEPTANE"  # scripted group (container) (typed FeaturePython)
  Dunit = g/cm3
  Dvalue = 0.68376
  Group = -> [C_element052,H_element046]
  conduct = 2
  density = 1
  expand = 3
  formula = G4_N-HEPTANE
  name = G4_N-HEPTANE
  specific = 4
FEATURE [App::DocumentObjectGroupPython] C_element053  label="C_element : 029"  # scripted group (container) (typed FeaturePython)
  n = 6
  ref = C_element
FEATURE [App::DocumentObjectGroupPython] H_element047  label="H_element : 14"  # scripted group (container) (typed FeaturePython)
  n = 14
  ref = H_element
FEATURE [App::DocumentObjectGroupPython] G4_N_HEXANE  label="G4_N-HEXANE"  # scripted group (container) (typed FeaturePython)
  Dunit = g/cm3
  Dvalue = 0.6603
  Group = -> [C_element053,H_element047]
  conduct = 2
  density = 1
  expand = 3
  formula = G4_N-HEXANE
  name = G4_N-HEXANE
  specific = 4
FEATURE [App::DocumentObjectGroupPython] C_element054  label="C_element : 22"  # scripted group (container) (typed FeaturePython)
  n = 22
  ref = C_element
FEATURE [App::DocumentObjectGroupPython] H_element048  label="H_element : 025"  # scripted group (container) (typed FeaturePython)
  n = 10
  ref = H_element
FEATURE [App::DocumentObjectGroupPython] N_element021  label="N_element : 010"  # scripted group (container) (typed FeaturePython)
  n = 2
  ref = N_element
FEATURE [App::DocumentObjectGroupPython] O_element050  label="O_element : 025"  # scripted group (container) (typed FeaturePython)
  n = 5
  ref = O_element
FEATURE [App::DocumentObjectGroupPython] G4_KAPTON  # scripted group (container) (typed FeaturePython)
  Dunit = g/cm3
  Dvalue = 1.42
  Group = -> [C_element054,H_element048,N_element021,O_element050]
  conduct = 2
  density = 1
  expand = 3
  formula = G4_KAPTON
  name = G4_KAPTON
  specific = 4
FEATURE [App::DocumentObjectGroupPython] La_element001  label="La_element : 1"  # scripted group (container) (typed FeaturePython)
  n = 1
  ref = La_element
FEATURE [App::DocumentObjectGroupPython] Br_element003  label="Br_element : 002"  # scripted group (container) (typed FeaturePython)
  n = 1
  ref = Br_element
FEATURE [App::DocumentObjectGroupPython] O_element051  label="O_element : 026"  # scripted group (container) (typed FeaturePython)
  n = 1
  ref = O_element
FEATURE [App::DocumentObjectGroupPython] G4_LANTHANUM_OXYBROMIDE  # scripted group (container) (typed FeaturePython)
  Dunit = g/cm3
  Dvalue = 6.28
  Group = -> [La_element001,Br_element003,O_element051]
  conduct = 2
  density = 1
  expand = 3
  formula = G4_LANTHANUM_OXYBROMIDE
  name = G4_LANTHANUM_OXYBROMIDE
  specific = 4
FEATURE [App::DocumentObjectGroupPython] La_element002  label="La_element : 2"  # scripted group (container) (typed FeaturePython)
  n = 2
  ref = La_element
FEATURE [App::DocumentObjectGroupPython] O_element052  label="O_element : 027"  # scripted group (container) (typed FeaturePython)
  n = 2
  ref = O_element
FEATURE [App::DocumentObjectGroupPython] S_element015  label="S_element : 006"  # scripted group (container) (typed FeaturePython)
  n = 1
  ref = S_element
FEATURE [App::DocumentObjectGroupPython] G4_LANTHANUM_OXYSULFIDE  # scripted group (container) (typed FeaturePython)
  Dunit = g/cm3
  Dvalue = 5.86
  Group = -> [La_element002,O_element052,S_element015]
  conduct = 2
  density = 1
  expand = 3
  formula = G4_LANTHANUM_OXYSULFIDE
  name = G4_LANTHANUM_OXYSULFIDE
  specific = 4
FEATURE [App::DocumentObjectGroupPython] O_element053  label="O_element : 0.072"  # scripted group (container) (typed FeaturePython)
  n = 0.071682
FEATURE [App::DocumentObjectGroupPython] Pb_element002  label="Pb_element : 0.928"  # scripted group (container) (typed FeaturePython)
  n = 0.928318
FEATURE [App::DocumentObjectGroupPython] G4_LEAD_OXIDE  # scripted group (container) (typed FeaturePython)
  Dunit = g/cm3
  Dvalue = 9.53
  Group = -> [O_element053,Pb_element002]
  conduct = 2
  density = 1
  expand = 3
  formula = G4_LEAD_OXIDE
  name = G4_LEAD_OXIDE
  specific = 4
FEATURE [App::DocumentObjectGroupPython] Li_element001  label="Li_element : 1"  # scripted group (container) (typed FeaturePython)
  n = 1
  ref = Li_element
FEATURE [App::DocumentObjectGroupPython] N_element022  label="N_element : 011"  # scripted group (container) (typed FeaturePython)
  n = 1
  ref = N_element
FEATURE [App::DocumentObjectGroupPython] H_element049  label="H_element : 026"  # scripted group (container) (typed FeaturePython)
  n = 2
  ref = H_element
FEATURE [App::DocumentObjectGroupPython] G4_LITHIUM_AMIDE  # scripted group (container) (typed FeaturePython)
  Dunit = g/cm3
  Dvalue = 1.178
  Group = -> [Li_element001,N_element022,H_element049]
  conduct = 2
  density = 1
  expand = 3
  formula = G4_LITHIUM_AMIDE
  name = G4_LITHIUM_AMIDE
  specific = 4
FEATURE [App::DocumentObjectGroupPython] Li_element002  label="Li_element : 2"  # scripted group (container) (typed FeaturePython)
  n = 2
  ref = Li_element
FEATURE [App::DocumentObjectGroupPython] C_element055  label="C_element : 030"  # scripted group (container) (typed FeaturePython)
  n = 1
  ref = C_element
FEATURE [App::DocumentObjectGroupPython] O_element054  label="O_element : 028"  # scripted group (container) (typed FeaturePython)
  n = 3
  ref = O_element
FEATURE [App::DocumentObjectGroupPython] G4_LITHIUM_CARBONATE  # scripted group (container) (typed FeaturePython)
  Dunit = g/cm3
  Dvalue = 2.11
  Group = -> [Li_element002,C_element055,O_element054]
  conduct = 2
  density = 1
  expand = 3
  formula = G4_LITHIUM_CARBONATE
  name = G4_LITHIUM_CARBONATE
  specific = 4
FEATURE [App::DocumentObjectGroupPython] Li_element003  label="Li_element : 003"  # scripted group (container) (typed FeaturePython)
  n = 1
  ref = Li_element
FEATURE [App::DocumentObjectGroupPython] F_element012  label="F_element : 004"  # scripted group (container) (typed FeaturePython)
  n = 1
  ref = F_element
FEATURE [App::DocumentObjectGroupPython] G4_LITHIUM_FLUORIDE  # scripted group (container) (typed FeaturePython)
  Dunit = g/cm3
  Dvalue = 2.635
  Group = -> [Li_element003,F_element012]
  conduct = 2
  density = 1
  expand = 3
  formula = G4_LITHIUM_FLUORIDE
  name = G4_LITHIUM_FLUORIDE
  specific = 4
FEATURE [App::DocumentObjectGroupPython] Li_element004  label="Li_element : 004"  # scripted group (container) (typed FeaturePython)
  n = 1
  ref = Li_element
FEATURE [App::DocumentObjectGroupPython] H_element050  label="H_element : 027"  # scripted group (container) (typed FeaturePython)
  n = 1
  ref = H_element
FEATURE [App::DocumentObjectGroupPython] G4_LITHIUM_HYDRIDE  # scripted group (container) (typed FeaturePython)
  Dunit = g/cm3
  Dvalue = 0.82
  Group = -> [Li_element004,H_element050]
  conduct = 2
  density = 1
  expand = 3
  formula = G4_LITHIUM_HYDRIDE
  name = G4_LITHIUM_HYDRIDE
  specific = 4
FEATURE [App::DocumentObjectGroupPython] Li_element005  label="Li_element : 005"  # scripted group (container) (typed FeaturePython)
  n = 1
  ref = Li_element
FEATURE [App::DocumentObjectGroupPython] I_element003  label="I_element : 002"  # scripted group (container) (typed FeaturePython)
  n = 1
  ref = I_element
FEATURE [App::DocumentObjectGroupPython] G4_LITHIUM_IODIDE  # scripted group (container) (typed FeaturePython)
  Dunit = g/cm3
  Dvalue = 3.494
  Group = -> [Li_element005,I_element003]
  conduct = 2
  density = 1
  expand = 3
  formula = G4_LITHIUM_IODIDE
  name = G4_LITHIUM_IODIDE
  specific = 4
FEATURE [App::DocumentObjectGroupPython] Li_element006  label="Li_element : 006"  # scripted group (container) (typed FeaturePython)
  n = 2
  ref = Li_element
FEATURE [App::DocumentObjectGroupPython] O_element055  label="O_element : 029"  # scripted group (container) (typed FeaturePython)
  n = 1
  ref = O_element
FEATURE [App::DocumentObjectGroupPython] G4_LITHIUM_OXIDE  # scripted group (container) (typed FeaturePython)
  Dunit = g/cm3
  Dvalue = 2.013
  Group = -> [Li_element006,O_element055]
  conduct = 2
  density = 1
  expand = 3
  formula = G4_LITHIUM_OXIDE
  name = G4_LITHIUM_OXIDE
  specific = 4
FEATURE [App::DocumentObjectGroupPython] Li_element007  label="Li_element : 007"  # scripted group (container) (typed FeaturePython)
  n = 2
  ref = Li_element
FEATURE [App::DocumentObjectGroupPython] B_element005  label="B_element : 005"  # scripted group (container) (typed FeaturePython)
  n = 4
  ref = B_element
FEATURE [App::DocumentObjectGroupPython] O_element056  label="O_element : 7"  # scripted group (container) (typed FeaturePython)
  n = 7
  ref = O_element
FEATURE [App::DocumentObjectGroupPython] G4_LITHIUM_TETRABORATE  # scripted group (container) (typed FeaturePython)
  Dunit = g/cm3
  Dvalue = 2.44
  Group = -> [Li_element007,B_element005,O_element056]
  conduct = 2
  density = 1
  expand = 3
  formula = G4_LITHIUM_TETRABORATE
  name = G4_LITHIUM_TETRABORATE
  specific = 4
FEATURE [App::DocumentObjectGroupPython] H_element051  label="H_element : 0.105"  # scripted group (container) (typed FeaturePython)
  n = 0.105
FEATURE [App::DocumentObjectGroupPython] C_element056  label="C_element : 0.083"  # scripted group (container) (typed FeaturePython)
  n = 0.083
FEATURE [App::DocumentObjectGroupPython] N_element023  label="N_element : 0.023"  # scripted group (container) (typed FeaturePython)
  n = 0.023
FEATURE [App::DocumentObjectGroupPython] O_element057  label="O_element : 0.779"  # scripted group (container) (typed FeaturePython)
  n = 0.779
FEATURE [App::DocumentObjectGroupPython] Na_element010  label="Na_element : 0.097"  # scripted group (container) (typed FeaturePython)
  n = 0.002
FEATURE [App::DocumentObjectGroupPython] P_element006  label="P_element : 0.105"  # scripted group (container) (typed FeaturePython)
  n = 0.001
FEATURE [App::DocumentObjectGroupPython] S_element016  label="S_element : 0.017"  # scripted group (container) (typed FeaturePython)
  n = 0.002
FEATURE [App::DocumentObjectGroupPython] Cl_element014  label="Cl_element : 0.587"  # scripted group (container) (typed FeaturePython)
  n = 0.003
FEATURE [App::DocumentObjectGroupPython] K_element005  label="K_element : 0.015"  # scripted group (container) (typed FeaturePython)
  n = 0.002
FEATURE [App::DocumentObjectGroupPython] G4_LUNG_ICRP  # scripted group (container) (typed FeaturePython)
  Dunit = g/cm3
  Dvalue = 1.04
  Group = -> [H_element051,C_element056,N_element023,O_element057,Na_element010,P_element006,S_element016,Cl_element014,K_element005]
  conduct = 2
  density = 1
  expand = 3
  formula = G4_LUNG_ICRP
  name = G4_LUNG_ICRP
  specific = 4
FEATURE [App::DocumentObjectGroupPython] H_element052  label="H_element : 0.116"  # scripted group (container) (typed FeaturePython)
  n = 0.114318
FEATURE [App::DocumentObjectGroupPython] C_element057  label="C_element : 0.656"  # scripted group (container) (typed FeaturePython)
  n = 0.655824
FEATURE [App::DocumentObjectGroupPython] O_element058  label="O_element : 0.092"  # scripted group (container) (typed FeaturePython)
  n = 0.0921831
FEATURE [App::DocumentObjectGroupPython] Mg_element004  label="Mg_element : 0.135"  # scripted group (container) (typed FeaturePython)
  n = 0.134792
FEATURE [App::DocumentObjectGroupPython] Ca_element013  label="Ca_element : 0.003"  # scripted group (container) (typed FeaturePython)
  n = 0.002883
FEATURE [App::DocumentObjectGroupPython] G4_M3_WAX  # scripted group (container) (typed FeaturePython)
  Dunit = g/cm3
  Dvalue = 1.05
  Group = -> [H_element052,C_element057,O_element058,Mg_element004,Ca_element013]
  conduct = 2
  density = 1
  expand = 3
  formula = G4_M3_WAX
  name = G4_M3_WAX
  specific = 4
FEATURE [App::DocumentObjectGroupPython] Mg_element005  label="Mg_element : 1"  # scripted group (container) (typed FeaturePython)
  n = 1
  ref = Mg_element
FEATURE [App::DocumentObjectGroupPython] C_element058  label="C_element : 031"  # scripted group (container) (typed FeaturePython)
  n = 1
  ref = C_element
FEATURE [App::DocumentObjectGroupPython] O_element059  label="O_element : 030"  # scripted group (container) (typed FeaturePython)
  n = 3
  ref = O_element
FEATURE [App::DocumentObjectGroupPython] G4_MAGNESIUM_CARBONATE  # scripted group (container) (typed FeaturePython)
  Dunit = g/cm3
  Dvalue = 2.958
  Group = -> [Mg_element005,C_element058,O_element059]
  conduct = 2
  density = 1
  expand = 3
  formula = G4_MAGNESIUM_CARBONATE
  name = G4_MAGNESIUM_CARBONATE
  specific = 4
FEATURE [App::DocumentObjectGroupPython] Mg_element006  label="Mg_element : 002"  # scripted group (container) (typed FeaturePython)
  n = 1
  ref = Mg_element
FEATURE [App::DocumentObjectGroupPython] F_element013  label="F_element : 005"  # scripted group (container) (typed FeaturePython)
  n = 2
  ref = F_element
FEATURE [App::DocumentObjectGroupPython] G4_MAGNESIUM_FLUORIDE  # scripted group (container) (typed FeaturePython)
  Dunit = g/cm3
  Dvalue = 3
  Group = -> [Mg_element006,F_element013]
  conduct = 2
  density = 1
  expand = 3
  formula = G4_MAGNESIUM_FLUORIDE
  name = G4_MAGNESIUM_FLUORIDE
  specific = 4
FEATURE [App::DocumentObjectGroupPython] Mg_element007  label="Mg_element : 003"  # scripted group (container) (typed FeaturePython)
  n = 1
  ref = Mg_element
FEATURE [App::DocumentObjectGroupPython] O_element060  label="O_element : 031"  # scripted group (container) (typed FeaturePython)
  n = 1
  ref = O_element
FEATURE [App::DocumentObjectGroupPython] G4_MAGNESIUM_OXIDE  # scripted group (container) (typed FeaturePython)
  Dunit = g/cm3
  Dvalue = 3.58
  Group = -> [Mg_element007,O_element060]
  conduct = 2
  density = 1
  expand = 3
  formula = G4_MAGNESIUM_OXIDE
  name = G4_MAGNESIUM_OXIDE
  specific = 4
FEATURE [App::DocumentObjectGroupPython] Mg_element008  label="Mg_element : 004"  # scripted group (container) (typed FeaturePython)
  n = 1
  ref = Mg_element
FEATURE [App::DocumentObjectGroupPython] B_element006  label="B_element : 006"  # scripted group (container) (typed FeaturePython)
  n = 4
  ref = B_element
FEATURE [App::DocumentObjectGroupPython] O_element061  label="O_element : 032"  # scripted group (container) (typed FeaturePython)
  n = 7
  ref = O_element
FEATURE [App::DocumentObjectGroupPython] G4_MAGNESIUM_TETRABORATE  # scripted group (container) (typed FeaturePython)
  Dunit = g/cm3
  Dvalue = 2.53
  Group = -> [Mg_element008,B_element006,O_element061]
  conduct = 2
  density = 1
  expand = 3
  formula = G4_MAGNESIUM_TETRABORATE
  name = G4_MAGNESIUM_TETRABORATE
  specific = 4
FEATURE [App::DocumentObjectGroupPython] Hg_element001  label="Hg_element : 1"  # scripted group (container) (typed FeaturePython)
  n = 1
  ref = Hg_element
FEATURE [App::DocumentObjectGroupPython] I_element004  label="I_element : 2"  # scripted group (container) (typed FeaturePython)
  n = 2
  ref = I_element
FEATURE [App::DocumentObjectGroupPython] G4_MERCURIC_IODIDE  # scripted group (container) (typed FeaturePython)
  Dunit = g/cm3
  Dvalue = 6.36
  Group = -> [Hg_element001,I_element004]
  conduct = 2
  density = 1
  expand = 3
  formula = G4_MERCURIC_IODIDE
  name = G4_MERCURIC_IODIDE
  specific = 4
FEATURE [App::DocumentObjectGroupPython] C_element059  label="C_element : 032"  # scripted group (container) (typed FeaturePython)
  n = 1
  ref = C_element
FEATURE [App::DocumentObjectGroupPython] H_element053  label="H_element : 028"  # scripted group (container) (typed FeaturePython)
  n = 4
  ref = H_element
FEATURE [App::DocumentObjectGroupPython] G4_METHANE  # scripted group (container) (typed FeaturePython)
  Dunit = g/cm3
  Dvalue = 0.000667151
  Group = -> [C_element059,H_element053]
  conduct = 2
  density = 1
  expand = 3
  formula = G4_METHANE
  name = G4_METHANE
  specific = 4
FEATURE [App::DocumentObjectGroupPython] C_element060  label="C_element : 033"  # scripted group (container) (typed FeaturePython)
  n = 1
  ref = C_element
FEATURE [App::DocumentObjectGroupPython] H_element054  label="H_element : 029"  # scripted group (container) (typed FeaturePython)
  n = 4
  ref = H_element
FEATURE [App::DocumentObjectGroupPython] O_element062  label="O_element : 033"  # scripted group (container) (typed FeaturePython)
  n = 1
  ref = O_element
FEATURE [App::DocumentObjectGroupPython] G4_METHANOL  # scripted group (container) (typed FeaturePython)
  Dunit = g/cm3
  Dvalue = 0.7914
  Group = -> [C_element060,H_element054,O_element062]
  conduct = 2
  density = 1
  expand = 3
  formula = G4_METHANOL
  name = G4_METHANOL
  specific = 4
FEATURE [App::DocumentObjectGroupPython] H_element055  label="H_element : 0.134"  # scripted group (container) (typed FeaturePython)
  n = 0.13404
FEATURE [App::DocumentObjectGroupPython] C_element061  label="C_element : 0.778"  # scripted group (container) (typed FeaturePython)
  n = 0.77796
FEATURE [App::DocumentObjectGroupPython] O_element063  label="O_element : 0.035"  # scripted group (container) (typed FeaturePython)
  n = 0.03502
FEATURE [App::DocumentObjectGroupPython] Mg_element009  label="Mg_element : 0.039"  # scripted group (container) (typed FeaturePython)
  n = 0.038594
FEATURE [App::DocumentObjectGroupPython] Ti_element002  label="Ti_element : 0.014"  # scripted group (container) (typed FeaturePython)
  n = 0.014386
FEATURE [App::DocumentObjectGroupPython] G4_MIX_D_WAX  # scripted group (container) (typed FeaturePython)
  Dunit = g/cm3
  Dvalue = 0.99
  Group = -> [H_element055,C_element061,O_element063,Mg_element009,Ti_element002]
  conduct = 2
  density = 1
  expand = 3
  formula = G4_MIX_D_WAX
  name = G4_MIX_D_WAX
  specific = 4
FEATURE [App::DocumentObjectGroupPython] H_element056  label="H_element : 0.135"  # scripted group (container) (typed FeaturePython)
  n = 0.081192
FEATURE [App::DocumentObjectGroupPython] C_element062  label="C_element : 0.583"  # scripted group (container) (typed FeaturePython)
  n = 0.583442
FEATURE [App::DocumentObjectGroupPython] N_element024  label="N_element : 0.018"  # scripted group (container) (typed FeaturePython)
  n = 0.017798
FEATURE [App::DocumentObjectGroupPython] O_element064  label="O_element : 0.186"  # scripted group (container) (typed FeaturePython)
  n = 0.186381
FEATURE [App::DocumentObjectGroupPython] Mg_element010  label="Mg_element : 0.130"  # scripted group (container) (typed FeaturePython)
  n = 0.130287
FEATURE [App::DocumentObjectGroupPython] Cl_element015  label="Cl_element : 0.588"  # scripted group (container) (typed FeaturePython)
  n = 0.0009
FEATURE [App::DocumentObjectGroupPython] G4_MS20_TISSUE  # scripted group (container) (typed FeaturePython)
  Dunit = g/cm3
  Dvalue = 1
  Group = -> [H_element056,C_element062,N_element024,O_element064,Mg_element010,Cl_element015]
  conduct = 2
  density = 1
  expand = 3
  formula = G4_MS20_TISSUE
  name = G4_MS20_TISSUE
  specific = 4
FEATURE [App::DocumentObjectGroupPython] H_element057  label="H_element : 0.136"  # scripted group (container) (typed FeaturePython)
  n = 0.102
FEATURE [App::DocumentObjectGroupPython] C_element063  label="C_element : 0.143"  # scripted group (container) (typed FeaturePython)
  n = 0.143
FEATURE [App::DocumentObjectGroupPython] N_element025  label="N_element : 0.034"  # scripted group (container) (typed FeaturePython)
  n = 0.034
FEATURE [App::DocumentObjectGroupPython] O_element065  label="O_element : 0.710"  # scripted group (container) (typed FeaturePython)
  n = 0.71
FEATURE [App::DocumentObjectGroupPython] Na_element011  label="Na_element : 0.098"  # scripted group (container) (typed FeaturePython)
  n = 0.001
FEATURE [App::DocumentObjectGroupPython] P_element007  label="P_element : 0.002"  # scripted group (container) (typed FeaturePython)
  n = 0.002
FEATURE [App::DocumentObjectGroupPython] S_element017  label="S_element : 0.018"  # scripted group (container) (typed FeaturePython)
  n = 0.003
FEATURE [App::DocumentObjectGroupPython] Cl_element016  label="Cl_element : 0.589"  # scripted group (container) (typed FeaturePython)
  n = 0.001
FEATURE [App::DocumentObjectGroupPython] K_element006  label="K_element : 0.004"  # scripted group (container) (typed FeaturePython)
  n = 0.004
FEATURE [App::DocumentObjectGroupPython] G4_MUSCLE_SKELETAL_ICRP  # scripted group (container) (typed FeaturePython)
  Dunit = g/cm3
  Dvalue = 1.05
  Group = -> [H_element057,C_element063,N_element025,O_element065,Na_element011,P_element007,S_element017,Cl_element016,K_element006]
  conduct = 2
  density = 1
  expand = 3
  formula = G4_MUSCLE_SKELETAL_ICRP
  name = G4_MUSCLE_SKELETAL_ICRP
  specific = 4
FEATURE [App::DocumentObjectGroupPython] H_element058  label="H_element : 0.137"  # scripted group (container) (typed FeaturePython)
  n = 0.102102
FEATURE [App::DocumentObjectGroupPython] C_element064  label="C_element : 0.123"  # scripted group (container) (typed FeaturePython)
  n = 0.123123
FEATURE [App::DocumentObjectGroupPython] N_element026  label="N_element : 0.756"  # scripted group (container) (typed FeaturePython)
  n = 0.035035
FEATURE [App::DocumentObjectGroupPython] O_element066  label="O_element : 0.730"  # scripted group (container) (typed FeaturePython)
  n = 0.72973
FEATURE [App::DocumentObjectGroupPython] Na_element012  label="Na_element : 0.099"  # scripted group (container) (typed FeaturePython)
  n = 0.001001
FEATURE [App::DocumentObjectGroupPython] P_element008  label="P_element : 0.106"  # scripted group (container) (typed FeaturePython)
  n = 0.002002
FEATURE [App::DocumentObjectGroupPython] S_element018  label="S_element : 0.019"  # scripted group (container) (typed FeaturePython)
  n = 0.004004
FEATURE [App::DocumentObjectGroupPython] K_element007  label="K_element : 0.016"  # scripted group (container) (typed FeaturePython)
  n = 0.003003
FEATURE [App::DocumentObjectGroupPython] G4_MUSCLE_STRIATED_ICRU  # scripted group (container) (typed FeaturePython)
  Dunit = g/cm3
  Dvalue = 1.04
  Group = -> [H_element058,C_element064,N_element026,O_element066,Na_element012,P_element008,S_element018,K_element007]
  conduct = 2
  density = 1
  expand = 3
  formula = G4_MUSCLE_STRIATED_ICRU
  name = G4_MUSCLE_STRIATED_ICRU
  specific = 4
FEATURE [App::DocumentObjectGroupPython] H_element059  label="H_element : 0.098"  # scripted group (container) (typed FeaturePython)
  n = 0.0982341
FEATURE [App::DocumentObjectGroupPython] C_element065  label="C_element : 0.156"  # scripted group (container) (typed FeaturePython)
  n = 0.156214
FEATURE [App::DocumentObjectGroupPython] N_element027  label="N_element : 0.757"  # scripted group (container) (typed FeaturePython)
  n = 0.035451
FEATURE [App::DocumentObjectGroupPython] O_element067  label="O_element : 0.880"  # scripted group (container) (typed FeaturePython)
  n = 0.710101
FEATURE [App::DocumentObjectGroupPython] G4_MUSCLE_WITH_SUCROSE  # scripted group (container) (typed FeaturePython)
  Dunit = g/cm3
  Dvalue = 1.11
  Group = -> [H_element059,C_element065,N_element027,O_element067]
  conduct = 2
  density = 1
  expand = 3
  formula = G4_MUSCLE_WITH_SUCROSE
  name = G4_MUSCLE_WITH_SUCROSE
  specific = 4
FEATURE [App::DocumentObjectGroupPython] H_element060  label="H_element : 0.138"  # scripted group (container) (typed FeaturePython)
  n = 0.101969
FEATURE [App::DocumentObjectGroupPython] C_element066  label="C_element : 0.120"  # scripted group (container) (typed FeaturePython)
  n = 0.120058
FEATURE [App::DocumentObjectGroupPython] N_element028  label="N_element : 0.758"  # scripted group (container) (typed FeaturePython)
  n = 0.035451
FEATURE [App::DocumentObjectGroupPython] O_element068  label="O_element : 0.743"  # scripted group (container) (typed FeaturePython)
  n = 0.742522
FEATURE [App::DocumentObjectGroupPython] G4_MUSCLE_WITHOUT_SUCROSE  # scripted group (container) (typed FeaturePython)
  Dunit = g/cm3
  Dvalue = 1.07
  Group = -> [H_element060,C_element066,N_element028,O_element068]
  conduct = 2
  density = 1
  expand = 3
  formula = G4_MUSCLE_WITHOUT_SUCROSE
  name = G4_MUSCLE_WITHOUT_SUCROSE
  specific = 4
FEATURE [App::DocumentObjectGroupPython] C_element067  label="C_element : 10"  # scripted group (container) (typed FeaturePython)
  n = 10
  ref = C_element
FEATURE [App::DocumentObjectGroupPython] H_element061  label="H_element : 030"  # scripted group (container) (typed FeaturePython)
  n = 8
  ref = H_element
FEATURE [App::DocumentObjectGroupPython] G4_NAPHTHALENE  # scripted group (container) (typed FeaturePython)
  Dunit = g/cm3
  Dvalue = 1.145
  Group = -> [C_element067,H_element061]
  conduct = 2
  density = 1
  expand = 3
  formula = G4_NAPHTHALENE
  name = G4_NAPHTHALENE
  specific = 4
FEATURE [App::DocumentObjectGroupPython] C_element068  label="C_element : 034"  # scripted group (container) (typed FeaturePython)
  n = 6
  ref = C_element
FEATURE [App::DocumentObjectGroupPython] H_element062  label="H_element : 031"  # scripted group (container) (typed FeaturePython)
  n = 5
  ref = H_element
FEATURE [App::DocumentObjectGroupPython] N_element029  label="N_element : 012"  # scripted group (container) (typed FeaturePython)
  n = 1
  ref = N_element
FEATURE [App::DocumentObjectGroupPython] O_element069  label="O_element : 034"  # scripted group (container) (typed FeaturePython)
  n = 2
  ref = O_element
FEATURE [App::DocumentObjectGroupPython] G4_NITROBENZENE  # scripted group (container) (typed FeaturePython)
  Dunit = g/cm3
  Dvalue = 1.19867
  Group = -> [C_element068,H_element062,N_element029,O_element069]
  conduct = 2
  density = 1
  expand = 3
  formula = G4_NITROBENZENE
  name = G4_NITROBENZENE
  specific = 4
FEATURE [App::DocumentObjectGroupPython] N_element030  label="N_element : 013"  # scripted group (container) (typed FeaturePython)
  n = 2
  ref = N_element
FEATURE [App::DocumentObjectGroupPython] O_element070  label="O_element : 035"  # scripted group (container) (typed FeaturePython)
  n = 1
  ref = O_element
FEATURE [App::DocumentObjectGroupPython] G4_NITROUS_OXIDE  # scripted group (container) (typed FeaturePython)
  Dunit = g/cm3
  Dvalue = 0.00183094
  Group = -> [N_element030,O_element070]
  conduct = 2
  density = 1
  expand = 3
  formula = G4_NITROUS_OXIDE
  name = G4_NITROUS_OXIDE
  specific = 4
FEATURE [App::DocumentObjectGroupPython] H_element063  label="H_element : 0.104"  # scripted group (container) (typed FeaturePython)
  n = 0.103509
FEATURE [App::DocumentObjectGroupPython] C_element069  label="C_element : 0.648"  # scripted group (container) (typed FeaturePython)
  n = 0.648416
FEATURE [App::DocumentObjectGroupPython] N_element031  label="N_element : 0.100"  # scripted group (container) (typed FeaturePython)
  n = 0.0995361
FEATURE [App::DocumentObjectGroupPython] O_element071  label="O_element : 0.149"  # scripted group (container) (typed FeaturePython)
  n = 0.148539
FEATURE [App::DocumentObjectGroupPython] G4_NYLON_8062  label="G4_NYLON-8062"  # scripted group (container) (typed FeaturePython)
  Dunit = g/cm3
  Dvalue = 1.08
  Group = -> [H_element063,C_element069,N_element031,O_element071]
  conduct = 2
  density = 1
  expand = 3
  formula = G4_NYLON-8062
  name = G4_NYLON-8062
  specific = 4
FEATURE [App::DocumentObjectGroupPython] C_element070  label="C_element : 035"  # scripted group (container) (typed FeaturePython)
  n = 6
  ref = C_element
FEATURE [App::DocumentObjectGroupPython] H_element064  label="H_element : 11"  # scripted group (container) (typed FeaturePython)
  n = 11
  ref = H_element
FEATURE [App::DocumentObjectGroupPython] N_element032  label="N_element : 014"  # scripted group (container) (typed FeaturePython)
  n = 1
  ref = N_element
FEATURE [App::DocumentObjectGroupPython] O_element072  label="O_element : 036"  # scripted group (container) (typed FeaturePython)
  n = 1
  ref = O_element
FEATURE [App::DocumentObjectGroupPython] G4_NYLON_6_6  label="G4_NYLON-6-6"  # scripted group (container) (typed FeaturePython)
  Dunit = g/cm3
  Dvalue = 1.14
  Group = -> [C_element070,H_element064,N_element032,O_element072]
  conduct = 2
  density = 1
  expand = 3
  formula = G4_NYLON-6-6
  name = G4_NYLON-6-6
  specific = 4
FEATURE [App::DocumentObjectGroupPython] H_element065  label="H_element : 0.139"  # scripted group (container) (typed FeaturePython)
  n = 0.107062
FEATURE [App::DocumentObjectGroupPython] C_element071  label="C_element : 0.680"  # scripted group (container) (typed FeaturePython)
  n = 0.680449
FEATURE [App::DocumentObjectGroupPython] N_element033  label="N_element : 0.099"  # scripted group (container) (typed FeaturePython)
  n = 0.099189
FEATURE [App::DocumentObjectGroupPython] O_element073  label="O_element : 0.113"  # scripted group (container) (typed FeaturePython)
  n = 0.1133
FEATURE [App::DocumentObjectGroupPython] G4_NYLON_6_10  label="G4_NYLON-6-10"  # scripted group (container) (typed FeaturePython)
  Dunit = g/cm3
  Dvalue = 1.14
  Group = -> [H_element065,C_element071,N_element033,O_element073]
  conduct = 2
  density = 1
  expand = 3
  formula = G4_NYLON-6-10
  name = G4_NYLON-6-10
  specific = 4
FEATURE [App::DocumentObjectGroupPython] H_element066  label="H_element : 0.140"  # scripted group (container) (typed FeaturePython)
  n = 0.115476
FEATURE [App::DocumentObjectGroupPython] C_element072  label="C_element : 0.721"  # scripted group (container) (typed FeaturePython)
  n = 0.720818
FEATURE [App::DocumentObjectGroupPython] N_element034  label="N_element : 0.076"  # scripted group (container) (typed FeaturePython)
  n = 0.0764169
FEATURE [App::DocumentObjectGroupPython] O_element074  label="O_element : 0.087"  # scripted group (container) (typed FeaturePython)
  n = 0.0872889
FEATURE [App::DocumentObjectGroupPython] G4_NYLON_11_RILSAN  label="G4_NYLON-11_RILSAN"  # scripted group (container) (typed FeaturePython)
  Dunit = g/cm3
  Dvalue = 1.425
  Group = -> [H_element066,C_element072,N_element034,O_element074]
  conduct = 2
  density = 1
  expand = 3
  formula = G4_NYLON-11_RILSAN
  name = G4_NYLON-11_RILSAN
  specific = 4
FEATURE [App::DocumentObjectGroupPython] C_element073  label="C_element : 8"  # scripted group (container) (typed FeaturePython)
  n = 8
  ref = C_element
FEATURE [App::DocumentObjectGroupPython] H_element067  label="H_element : 18"  # scripted group (container) (typed FeaturePython)
  n = 18
  ref = H_element
FEATURE [App::DocumentObjectGroupPython] G4_OCTANE  # scripted group (container) (typed FeaturePython)
  Dunit = g/cm3
  Dvalue = 0.7026
  Group = -> [C_element073,H_element067]
  conduct = 2
  density = 1
  expand = 3
  formula = G4_OCTANE
  name = G4_OCTANE
  specific = 4
FEATURE [App::DocumentObjectGroupPython] C_element074  label="C_element : 25"  # scripted group (container) (typed FeaturePython)
  n = 25
  ref = C_element
FEATURE [App::DocumentObjectGroupPython] H_element068  label="H_element : 52"  # scripted group (container) (typed FeaturePython)
  n = 52
  ref = H_element
FEATURE [App::DocumentObjectGroupPython] G4_PARAFFIN  # scripted group (container) (typed FeaturePython)
  Dunit = g/cm3
  Dvalue = 0.93
  Group = -> [C_element074,H_element068]
  conduct = 2
  density = 1
  expand = 3
  formula = G4_PARAFFIN
  name = G4_PARAFFIN
  specific = 4
FEATURE [App::DocumentObjectGroupPython] C_element075  label="C_element : 036"  # scripted group (container) (typed FeaturePython)
  n = 5
  ref = C_element
FEATURE [App::DocumentObjectGroupPython] H_element069  label="H_element : 032"  # scripted group (container) (typed FeaturePython)
  n = 12
  ref = H_element
FEATURE [App::DocumentObjectGroupPython] G4_N_PENTANE  label="G4_N-PENTANE"  # scripted group (container) (typed FeaturePython)
  Dunit = g/cm3
  Dvalue = 0.6262
  Group = -> [C_element075,H_element069]
  conduct = 2
  density = 1
  expand = 3
  formula = G4_N-PENTANE
  name = G4_N-PENTANE
  specific = 4
FEATURE [App::DocumentObjectGroupPython] H_element070  label="H_element : 0.014"  # scripted group (container) (typed FeaturePython)
  n = 0.0141
FEATURE [App::DocumentObjectGroupPython] C_element076  label="C_element : 0.072"  # scripted group (container) (typed FeaturePython)
  n = 0.072261
FEATURE [App::DocumentObjectGroupPython] N_element035  label="N_element : 0.019"  # scripted group (container) (typed FeaturePython)
  n = 0.01932
FEATURE [App::DocumentObjectGroupPython] O_element075  label="O_element : 0.066"  # scripted group (container) (typed FeaturePython)
  n = 0.066101
FEATURE [App::DocumentObjectGroupPython] S_element019  label="S_element : 0.020"  # scripted group (container) (typed FeaturePython)
  n = 0.00189
FEATURE [App::DocumentObjectGroupPython] Br_element004  label="Br_element : 0.349"  # scripted group (container) (typed FeaturePython)
  n = 0.349103
FEATURE [App::DocumentObjectGroupPython] Ag_element001  label="Ag_element : 0.474"  # scripted group (container) (typed FeaturePython)
  n = 0.474105
FEATURE [App::DocumentObjectGroupPython] I_element005  label="I_element : 0.003"  # scripted group (container) (typed FeaturePython)
  n = 0.00312
FEATURE [App::DocumentObjectGroupPython] G4_PHOTO_EMULSION  # scripted group (container) (typed FeaturePython)
  Dunit = g/cm3
  Dvalue = 3.815
  Group = -> [H_element070,C_element076,N_element035,O_element075,S_element019,Br_element004,Ag_element001,I_element005]
  conduct = 2
  density = 1
  expand = 3
  formula = G4_PHOTO_EMULSION
  name = G4_PHOTO_EMULSION
  specific = 4
FEATURE [App::DocumentObjectGroupPython] C_element077  label="C_element : 9"  # scripted group (container) (typed FeaturePython)
  n = 9
  ref = C_element
FEATURE [App::DocumentObjectGroupPython] H_element071  label="H_element : 033"  # scripted group (container) (typed FeaturePython)
  n = 10
  ref = H_element
FEATURE [App::DocumentObjectGroupPython] G4_PLASTIC_SC_VINYLTOLUENE  # scripted group (container) (typed FeaturePython)
  Dunit = g/cm3
  Dvalue = 1.032
  Group = -> [C_element077,H_element071]
  conduct = 2
  density = 1
  expand = 3
  formula = G4_PLASTIC_SC_VINYLTOLUENE
  name = G4_PLASTIC_SC_VINYLTOLUENE
  specific = 4
FEATURE [App::DocumentObjectGroupPython] Pu_element001  label="Pu_element : 1"  # scripted group (container) (typed FeaturePython)
  n = 1
  ref = Pu_element
FEATURE [App::DocumentObjectGroupPython] O_element076  label="O_element : 037"  # scripted group (container) (typed FeaturePython)
  n = 2
  ref = O_element
FEATURE [App::DocumentObjectGroupPython] G4_PLUTONIUM_DIOXIDE  # scripted group (container) (typed FeaturePython)
  Dunit = g/cm3
  Dvalue = 11.46
  Group = -> [Pu_element001,O_element076]
  conduct = 2
  density = 1
  expand = 3
  formula = G4_PLUTONIUM_DIOXIDE
  name = G4_PLUTONIUM_DIOXIDE
  specific = 4
FEATURE [App::DocumentObjectGroupPython] C_element078  label="C_element : 037"  # scripted group (container) (typed FeaturePython)
  n = 3
  ref = C_element
FEATURE [App::DocumentObjectGroupPython] H_element072  label="H_element : 034"  # scripted group (container) (typed FeaturePython)
  n = 3
  ref = H_element
FEATURE [App::DocumentObjectGroupPython] N_element036  label="N_element : 015"  # scripted group (container) (typed FeaturePython)
  n = 1
  ref = N_element
FEATURE [App::DocumentObjectGroupPython] G4_POLYACRYLONITRILE  # scripted group (container) (typed FeaturePython)
  Dunit = g/cm3
  Dvalue = 1.17
  Group = -> [C_element078,H_element072,N_element036]
  conduct = 2
  density = 1
  expand = 3
  formula = G4_POLYACRYLONITRILE
  name = G4_POLYACRYLONITRILE
  specific = 4
FEATURE [App::DocumentObjectGroupPython] C_element079  label="C_element : 16"  # scripted group (container) (typed FeaturePython)
  n = 16
  ref = C_element
FEATURE [App::DocumentObjectGroupPython] H_element073  label="H_element : 035"  # scripted group (container) (typed FeaturePython)
  n = 14
  ref = H_element
FEATURE [App::DocumentObjectGroupPython] O_element077  label="O_element : 038"  # scripted group (container) (typed FeaturePython)
  n = 3
  ref = O_element
FEATURE [App::DocumentObjectGroupPython] G4_POLYCARBONATE  # scripted group (container) (typed FeaturePython)
  Dunit = g/cm3
  Dvalue = 1.2
  Group = -> [C_element079,H_element073,O_element077]
  conduct = 2
  density = 1
  expand = 3
  formula = G4_POLYCARBONATE
  name = G4_POLYCARBONATE
  specific = 4
FEATURE [App::DocumentObjectGroupPython] C_element080  label="C_element : 038"  # scripted group (container) (typed FeaturePython)
  n = 8
  ref = C_element
FEATURE [App::DocumentObjectGroupPython] H_element074  label="H_element : 036"  # scripted group (container) (typed FeaturePython)
  n = 7
  ref = H_element
FEATURE [App::DocumentObjectGroupPython] Cl_element017  label="Cl_element : 007"  # scripted group (container) (typed FeaturePython)
  n = 1
  ref = Cl_element
FEATURE [App::DocumentObjectGroupPython] G4_POLYCHLOROSTYRENE  # scripted group (container) (typed FeaturePython)
  Dunit = g/cm3
  Dvalue = 1.3
  Group = -> [C_element080,H_element074,Cl_element017]
  conduct = 2
  density = 1
  expand = 3
  formula = G4_POLYCHLOROSTYRENE
  name = G4_POLYCHLOROSTYRENE
  specific = 4
FEATURE [App::DocumentObjectGroupPython] C_element081  label="C_element : 039"  # scripted group (container) (typed FeaturePython)
  n = 1
  ref = C_element
FEATURE [App::DocumentObjectGroupPython] H_element075  label="H_element : 037"  # scripted group (container) (typed FeaturePython)
  n = 2
  ref = H_element
FEATURE [App::DocumentObjectGroupPython] G4_POLYETHYLENE  # scripted group (container) (typed FeaturePython)
  Dunit = g/cm3
  Dvalue = 0.94
  Group = -> [C_element081,H_element075]
  conduct = 2
  density = 1
  expand = 3
  formula = G4_POLYETHYLENE
  name = G4_POLYETHYLENE
  specific = 4
FEATURE [App::DocumentObjectGroupPython] C_element082  label="C_element : 040"  # scripted group (container) (typed FeaturePython)
  n = 10
  ref = C_element
FEATURE [App::DocumentObjectGroupPython] H_element076  label="H_element : 038"  # scripted group (container) (typed FeaturePython)
  n = 8
  ref = H_element
FEATURE [App::DocumentObjectGroupPython] O_element078  label="O_element : 039"  # scripted group (container) (typed FeaturePython)
  n = 4
  ref = O_element
FEATURE [App::DocumentObjectGroupPython] G4_MYLAR  # scripted group (container) (typed FeaturePython)
  Dunit = g/cm3
  Dvalue = 1.4
  Group = -> [C_element082,H_element076,O_element078]
  conduct = 2
  density = 1
  expand = 3
  formula = G4_MYLAR
  name = G4_MYLAR
  specific = 4
FEATURE [App::DocumentObjectGroupPython] C_element083  label="C_element : 041"  # scripted group (container) (typed FeaturePython)
  n = 5
  ref = C_element
FEATURE [App::DocumentObjectGroupPython] H_element077  label="H_element : 039"  # scripted group (container) (typed FeaturePython)
  n = 8
  ref = H_element
FEATURE [App::DocumentObjectGroupPython] O_element079  label="O_element : 040"  # scripted group (container) (typed FeaturePython)
  n = 2
  ref = O_element
FEATURE [App::DocumentObjectGroupPython] G4_PLEXIGLASS  # scripted group (container) (typed FeaturePython)
  Dunit = g/cm3
  Dvalue = 1.19
  Group = -> [C_element083,H_element077,O_element079]
  conduct = 2
  density = 1
  expand = 3
  formula = G4_PLEXIGLASS
  name = G4_PLEXIGLASS
  specific = 4
FEATURE [App::DocumentObjectGroupPython] C_element084  label="C_element : 042"  # scripted group (container) (typed FeaturePython)
  n = 1
  ref = C_element
FEATURE [App::DocumentObjectGroupPython] H_element078  label="H_element : 040"  # scripted group (container) (typed FeaturePython)
  n = 2
  ref = H_element
FEATURE [App::DocumentObjectGroupPython] O_element080  label="O_element : 041"  # scripted group (container) (typed FeaturePython)
  n = 1
  ref = O_element
FEATURE [App::DocumentObjectGroupPython] G4_POLYOXYMETHYLENE  # scripted group (container) (typed FeaturePython)
  Dunit = g/cm3
  Dvalue = 1.425
  Group = -> [C_element084,H_element078,O_element080]
  conduct = 2
  density = 1
  expand = 3
  formula = G4_POLYOXYMETHYLENE
  name = G4_POLYOXYMETHYLENE
  specific = 4
FEATURE [App::DocumentObjectGroupPython] C_element085  label="C_element : 043"  # scripted group (container) (typed FeaturePython)
  n = 2
  ref = C_element
FEATURE [App::DocumentObjectGroupPython] H_element079  label="H_element : 041"  # scripted group (container) (typed FeaturePython)
  n = 4
  ref = H_element
FEATURE [App::DocumentObjectGroupPython] G4_POLYPROPYLENE  # scripted group (container) (typed FeaturePython)
  Dunit = g/cm3
  Dvalue = 0.9
  Group = -> [C_element085,H_element079]
  conduct = 2
  density = 1
  expand = 3
  formula = G4_POLYPROPYLENE
  name = G4_POLYPROPYLENE
  specific = 4
FEATURE [App::DocumentObjectGroupPython] C_element086  label="C_element : 044"  # scripted group (container) (typed FeaturePython)
  n = 8
  ref = C_element
FEATURE [App::DocumentObjectGroupPython] H_element080  label="H_element : 042"  # scripted group (container) (typed FeaturePython)
  n = 8
  ref = H_element
FEATURE [App::DocumentObjectGroupPython] G4_POLYSTYRENE  # scripted group (container) (typed FeaturePython)
  Dunit = g/cm3
  Dvalue = 1.06
  Group = -> [C_element086,H_element080]
  conduct = 2
  density = 1
  expand = 3
  formula = G4_POLYSTYRENE
  name = G4_POLYSTYRENE
  specific = 4
FEATURE [App::DocumentObjectGroupPython] C_element087  label="C_element : 045"  # scripted group (container) (typed FeaturePython)
  n = 2
  ref = C_element
FEATURE [App::DocumentObjectGroupPython] F_element014  label="F_element : 4"  # scripted group (container) (typed FeaturePython)
  n = 4
  ref = F_element
FEATURE [App::DocumentObjectGroupPython] G4_TEFLON  # scripted group (container) (typed FeaturePython)
  Dunit = g/cm3
  Dvalue = 2.2
  Group = -> [C_element087,F_element014]
  conduct = 2
  density = 1
  expand = 3
  formula = G4_TEFLON
  name = G4_TEFLON
  specific = 4
FEATURE [App::DocumentObjectGroupPython] C_element088  label="C_element : 046"  # scripted group (container) (typed FeaturePython)
  n = 2
  ref = C_element
FEATURE [App::DocumentObjectGroupPython] F_element015  label="F_element : 006"  # scripted group (container) (typed FeaturePython)
  n = 3
  ref = F_element
FEATURE [App::DocumentObjectGroupPython] Cl_element018  label="Cl_element : 008"  # scripted group (container) (typed FeaturePython)
  n = 1
  ref = Cl_element
FEATURE [App::DocumentObjectGroupPython] G4_POLYTRIFLUOROCHLOROETHYLENE  # scripted group (container) (typed FeaturePython)
  Dunit = g/cm3
  Dvalue = 2.1
  Group = -> [C_element088,F_element015,Cl_element018]
  conduct = 2
  density = 1
  expand = 3
  formula = G4_POLYTRIFLUOROCHLOROETHYLENE
  name = G4_POLYTRIFLUOROCHLOROETHYLENE
  specific = 4
FEATURE [App::DocumentObjectGroupPython] C_element089  label="C_element : 047"  # scripted group (container) (typed FeaturePython)
  n = 4
  ref = C_element
FEATURE [App::DocumentObjectGroupPython] H_element081  label="H_element : 043"  # scripted group (container) (typed FeaturePython)
  n = 6
  ref = H_element
FEATURE [App::DocumentObjectGroupPython] O_element081  label="O_element : 042"  # scripted group (container) (typed FeaturePython)
  n = 2
  ref = O_element
FEATURE [App::DocumentObjectGroupPython] G4_POLYVINYL_ACETATE  # scripted group (container) (typed FeaturePython)
  Dunit = g/cm3
  Dvalue = 1.19
  Group = -> [C_element089,H_element081,O_element081]
  conduct = 2
  density = 1
  expand = 3
  formula = G4_POLYVINYL_ACETATE
  name = G4_POLYVINYL_ACETATE
  specific = 4
FEATURE [App::DocumentObjectGroupPython] C_element090  label="C_element : 048"  # scripted group (container) (typed FeaturePython)
  n = 2
  ref = C_element
FEATURE [App::DocumentObjectGroupPython] H_element082  label="H_element : 044"  # scripted group (container) (typed FeaturePython)
  n = 4
  ref = H_element
FEATURE [App::DocumentObjectGroupPython] O_element082  label="O_element : 043"  # scripted group (container) (typed FeaturePython)
  n = 1
  ref = O_element
FEATURE [App::DocumentObjectGroupPython] G4_POLYVINYL_ALCOHOL  # scripted group (container) (typed FeaturePython)
  Dunit = g/cm3
  Dvalue = 1.3
  Group = -> [C_element090,H_element082,O_element082]
  conduct = 2
  density = 1
  expand = 3
  formula = G4_POLYVINYL_ALCOHOL
  name = G4_POLYVINYL_ALCOHOL
  specific = 4
FEATURE [App::DocumentObjectGroupPython] C_element091  label="C_element : 049"  # scripted group (container) (typed FeaturePython)
  n = 8
  ref = C_element
FEATURE [App::DocumentObjectGroupPython] H_element083  label="H_element : 045"  # scripted group (container) (typed FeaturePython)
  n = 14
  ref = H_element
FEATURE [App::DocumentObjectGroupPython] O_element083  label="O_element : 044"  # scripted group (container) (typed FeaturePython)
  n = 2
  ref = O_element
FEATURE [App::DocumentObjectGroupPython] G4_POLYVINYL_BUTYRAL  # scripted group (container) (typed FeaturePython)
  Dunit = g/cm3
  Dvalue = 1.12
  Group = -> [C_element091,H_element083,O_element083]
  conduct = 2
  density = 1
  expand = 3
  formula = G4_POLYVINYL_BUTYRAL
  name = G4_POLYVINYL_BUTYRAL
  specific = 4
FEATURE [App::DocumentObjectGroupPython] C_element092  label="C_element : 050"  # scripted group (container) (typed FeaturePython)
  n = 2
  ref = C_element
FEATURE [App::DocumentObjectGroupPython] H_element084  label="H_element : 046"  # scripted group (container) (typed FeaturePython)
  n = 3
  ref = H_element
FEATURE [App::DocumentObjectGroupPython] Cl_element019  label="Cl_element : 009"  # scripted group (container) (typed FeaturePython)
  n = 1
  ref = Cl_element
FEATURE [App::DocumentObjectGroupPython] G4_POLYVINYL_CHLORIDE  # scripted group (container) (typed FeaturePython)
  Dunit = g/cm3
  Dvalue = 1.3
  Group = -> [C_element092,H_element084,Cl_element019]
  conduct = 2
  density = 1
  expand = 3
  formula = G4_POLYVINYL_CHLORIDE
  name = G4_POLYVINYL_CHLORIDE
  specific = 4
FEATURE [App::DocumentObjectGroupPython] C_element093  label="C_element : 051"  # scripted group (container) (typed FeaturePython)
  n = 2
  ref = C_element
FEATURE [App::DocumentObjectGroupPython] H_element085  label="H_element : 047"  # scripted group (container) (typed FeaturePython)
  n = 2
  ref = H_element
FEATURE [App::DocumentObjectGroupPython] Cl_element020  label="Cl_element : 010"  # scripted group (container) (typed FeaturePython)
  n = 2
  ref = Cl_element
FEATURE [App::DocumentObjectGroupPython] G4_POLYVINYLIDENE_CHLORIDE  # scripted group (container) (typed FeaturePython)
  Dunit = g/cm3
  Dvalue = 1.7
  Group = -> [C_element093,H_element085,Cl_element020]
  conduct = 2
  density = 1
  expand = 3
  formula = G4_POLYVINYLIDENE_CHLORIDE
  name = G4_POLYVINYLIDENE_CHLORIDE
  specific = 4
FEATURE [App::DocumentObjectGroupPython] C_element094  label="C_element : 052"  # scripted group (container) (typed FeaturePython)
  n = 2
  ref = C_element
FEATURE [App::DocumentObjectGroupPython] H_element086  label="H_element : 048"  # scripted group (container) (typed FeaturePython)
  n = 2
  ref = H_element
FEATURE [App::DocumentObjectGroupPython] F_element016  label="F_element : 007"  # scripted group (container) (typed FeaturePython)
  n = 2
  ref = F_element
FEATURE [App::DocumentObjectGroupPython] G4_POLYVINYLIDENE_FLUORIDE  # scripted group (container) (typed FeaturePython)
  Dunit = g/cm3
  Dvalue = 1.76
  Group = -> [C_element094,H_element086,F_element016]
  conduct = 2
  density = 1
  expand = 3
  formula = G4_POLYVINYLIDENE_FLUORIDE
  name = G4_POLYVINYLIDENE_FLUORIDE
  specific = 4
FEATURE [App::DocumentObjectGroupPython] C_element095  label="C_element : 053"  # scripted group (container) (typed FeaturePython)
  n = 6
  ref = C_element
FEATURE [App::DocumentObjectGroupPython] H_element087  label="H_element : 9"  # scripted group (container) (typed FeaturePython)
  n = 9
  ref = H_element
FEATURE [App::DocumentObjectGroupPython] N_element037  label="N_element : 016"  # scripted group (container) (typed FeaturePython)
  n = 1
  ref = N_element
FEATURE [App::DocumentObjectGroupPython] O_element084  label="O_element : 045"  # scripted group (container) (typed FeaturePython)
  n = 1
  ref = O_element
FEATURE [App::DocumentObjectGroupPython] G4_POLYVINYL_PYRROLIDONE  # scripted group (container) (typed FeaturePython)
  Dunit = g/cm3
  Dvalue = 1.25
  Group = -> [C_element095,H_element087,N_element037,O_element084]
  conduct = 2
  density = 1
  expand = 3
  formula = G4_POLYVINYL_PYRROLIDONE
  name = G4_POLYVINYL_PYRROLIDONE
  specific = 4
FEATURE [App::DocumentObjectGroupPython] K_element008  label="K_element : 1"  # scripted group (container) (typed FeaturePython)
  n = 1
  ref = K_element
FEATURE [App::DocumentObjectGroupPython] I_element006  label="I_element : 003"  # scripted group (container) (typed FeaturePython)
  n = 1
  ref = I_element
FEATURE [App::DocumentObjectGroupPython] G4_POTASSIUM_IODIDE  # scripted group (container) (typed FeaturePython)
  Dunit = g/cm3
  Dvalue = 3.13
  Group = -> [K_element008,I_element006]
  conduct = 2
  density = 1
  expand = 3
  formula = G4_POTASSIUM_IODIDE
  name = G4_POTASSIUM_IODIDE
  specific = 4
FEATURE [App::DocumentObjectGroupPython] K_element009  label="K_element : 2"  # scripted group (container) (typed FeaturePython)
  n = 2
  ref = K_element
FEATURE [App::DocumentObjectGroupPython] O_element085  label="O_element : 046"  # scripted group (container) (typed FeaturePython)
  n = 1
  ref = O_element
FEATURE [App::DocumentObjectGroupPython] G4_POTASSIUM_OXIDE  # scripted group (container) (typed FeaturePython)
  Dunit = g/cm3
  Dvalue = 2.32
  Group = -> [K_element009,O_element085]
  conduct = 2
  density = 1
  expand = 3
  formula = G4_POTASSIUM_OXIDE
  name = G4_POTASSIUM_OXIDE
  specific = 4
FEATURE [App::DocumentObjectGroupPython] C_element096  label="C_element : 054"  # scripted group (container) (typed FeaturePython)
  n = 3
  ref = C_element
FEATURE [App::DocumentObjectGroupPython] H_element088  label="H_element : 049"  # scripted group (container) (typed FeaturePython)
  n = 8
  ref = H_element
FEATURE [App::DocumentObjectGroupPython] G4_PROPANE  # scripted group (container) (typed FeaturePython)
  Dunit = g/cm3
  Dvalue = 0.00187939
  Group = -> [C_element096,H_element088]
  conduct = 2
  density = 1
  expand = 3
  formula = G4_PROPANE
  name = G4_PROPANE
  specific = 4
FEATURE [App::DocumentObjectGroupPython] C_element097  label="C_element : 055"  # scripted group (container) (typed FeaturePython)
  n = 3
  ref = C_element
FEATURE [App::DocumentObjectGroupPython] H_element089  label="H_element : 050"  # scripted group (container) (typed FeaturePython)
  n = 8
  ref = H_element
FEATURE [App::DocumentObjectGroupPython] G4_lPROPANE  # scripted group (container) (typed FeaturePython)
  Dunit = g/cm3
  Dvalue = 0.43
  Group = -> [C_element097,H_element089]
  conduct = 2
  density = 1
  expand = 3
  formula = G4_lPROPANE
  name = G4_lPROPANE
  specific = 4
FEATURE [App::DocumentObjectGroupPython] C_element098  label="C_element : 056"  # scripted group (container) (typed FeaturePython)
  n = 3
  ref = C_element
FEATURE [App::DocumentObjectGroupPython] H_element090  label="H_element : 051"  # scripted group (container) (typed FeaturePython)
  n = 8
  ref = H_element
FEATURE [App::DocumentObjectGroupPython] O_element086  label="O_element : 047"  # scripted group (container) (typed FeaturePython)
  n = 1
  ref = O_element
FEATURE [App::DocumentObjectGroupPython] G4_N_PROPYL_ALCOHOL  label="G4_N-PROPYL_ALCOHOL"  # scripted group (container) (typed FeaturePython)
  Dunit = g/cm3
  Dvalue = 0.8035
  Group = -> [C_element098,H_element090,O_element086]
  conduct = 2
  density = 1
  expand = 3
  formula = G4_N-PROPYL_ALCOHOL
  name = G4_N-PROPYL_ALCOHOL
  specific = 4
FEATURE [App::DocumentObjectGroupPython] C_element099  label="C_element : 057"  # scripted group (container) (typed FeaturePython)
  n = 5
  ref = C_element
FEATURE [App::DocumentObjectGroupPython] H_element091  label="H_element : 052"  # scripted group (container) (typed FeaturePython)
  n = 5
  ref = H_element
FEATURE [App::DocumentObjectGroupPython] N_element038  label="N_element : 017"  # scripted group (container) (typed FeaturePython)
  n = 1
  ref = N_element
FEATURE [App::DocumentObjectGroupPython] G4_PYRIDINE  # scripted group (container) (typed FeaturePython)
  Dunit = g/cm3
  Dvalue = 0.9819
  Group = -> [C_element099,H_element091,N_element038]
  conduct = 2
  density = 1
  expand = 3
  formula = G4_PYRIDINE
  name = G4_PYRIDINE
  specific = 4
FEATURE [App::DocumentObjectGroupPython] H_element092  label="H_element : 0.144"  # scripted group (container) (typed FeaturePython)
  n = 0.143711
FEATURE [App::DocumentObjectGroupPython] C_element100  label="C_element : 0.856"  # scripted group (container) (typed FeaturePython)
  n = 0.856289
FEATURE [App::DocumentObjectGroupPython] G4_RUBBER_BUTYL  # scripted group (container) (typed FeaturePython)
  Dunit = g/cm3
  Dvalue = 0.92
  Group = -> [H_element092,C_element100]
  conduct = 2
  density = 1
  expand = 3
  formula = G4_RUBBER_BUTYL
  name = G4_RUBBER_BUTYL
  specific = 4
FEATURE [App::DocumentObjectGroupPython] H_element093  label="H_element : 0.118"  # scripted group (container) (typed FeaturePython)
  n = 0.118371
FEATURE [App::DocumentObjectGroupPython] C_element101  label="C_element : 0.882"  # scripted group (container) (typed FeaturePython)
  n = 0.881629
FEATURE [App::DocumentObjectGroupPython] G4_RUBBER_NATURAL  # scripted group (container) (typed FeaturePython)
  Dunit = g/cm3
  Dvalue = 0.92
  Group = -> [H_element093,C_element101]
  conduct = 2
  density = 1
  expand = 3
  formula = G4_RUBBER_NATURAL
  name = G4_RUBBER_NATURAL
  specific = 4
FEATURE [App::DocumentObjectGroupPython] H_element094  label="H_element : 0.145"  # scripted group (container) (typed FeaturePython)
  n = 0.05692
FEATURE [App::DocumentObjectGroupPython] C_element102  label="C_element : 0.543"  # scripted group (container) (typed FeaturePython)
  n = 0.542646
FEATURE [App::DocumentObjectGroupPython] Cl_element021  label="Cl_element : 0.400"  # scripted group (container) (typed FeaturePython)
  n = 0.400434
FEATURE [App::DocumentObjectGroupPython] G4_RUBBER_NEOPRENE  # scripted group (container) (typed FeaturePython)
  Dunit = g/cm3
  Dvalue = 1.23
  Group = -> [H_element094,C_element102,Cl_element021]
  conduct = 2
  density = 1
  expand = 3
  formula = G4_RUBBER_NEOPRENE
  name = G4_RUBBER_NEOPRENE
  specific = 4
FEATURE [App::DocumentObjectGroupPython] Si_element006  label="Si_element : 1"  # scripted group (container) (typed FeaturePython)
  n = 1
  ref = Si_element
FEATURE [App::DocumentObjectGroupPython] O_element087  label="O_element : 048"  # scripted group (container) (typed FeaturePython)
  n = 2
  ref = O_element
FEATURE [App::DocumentObjectGroupPython] G4_SILICON_DIOXIDE  # scripted group (container) (typed FeaturePython)
  Dunit = g/cm3
  Dvalue = 2.32
  Group = -> [Si_element006,O_element087]
  conduct = 2
  density = 1
  expand = 3
  formula = G4_SILICON_DIOXIDE
  name = G4_SILICON_DIOXIDE
  specific = 4
FEATURE [App::DocumentObjectGroupPython] Ag_element002  label="Ag_element : 1"  # scripted group (container) (typed FeaturePython)
  n = 1
  ref = Ag_element
FEATURE [App::DocumentObjectGroupPython] Br_element005  label="Br_element : 003"  # scripted group (container) (typed FeaturePython)
  n = 1
  ref = Br_element
FEATURE [App::DocumentObjectGroupPython] G4_SILVER_BROMIDE  # scripted group (container) (typed FeaturePython)
  Dunit = g/cm3
  Dvalue = 6.473
  Group = -> [Ag_element002,Br_element005]
  conduct = 2
  density = 1
  expand = 3
  formula = G4_SILVER_BROMIDE
  name = G4_SILVER_BROMIDE
  specific = 4
FEATURE [App::DocumentObjectGroupPython] Ag_element003  label="Ag_element : 002"  # scripted group (container) (typed FeaturePython)
  n = 1
  ref = Ag_element
FEATURE [App::DocumentObjectGroupPython] Cl_element022  label="Cl_element : 011"  # scripted group (container) (typed FeaturePython)
  n = 1
  ref = Cl_element
FEATURE [App::DocumentObjectGroupPython] G4_SILVER_CHLORIDE  # scripted group (container) (typed FeaturePython)
  Dunit = g/cm3
  Dvalue = 5.56
  Group = -> [Ag_element003,Cl_element022]
  conduct = 2
  density = 1
  expand = 3
  formula = G4_SILVER_CHLORIDE
  name = G4_SILVER_CHLORIDE
  specific = 4
FEATURE [App::DocumentObjectGroupPython] Br_element006  label="Br_element : 0.423"  # scripted group (container) (typed FeaturePython)
  n = 0.422895
FEATURE [App::DocumentObjectGroupPython] Ag_element004  label="Ag_element : 0.574"  # scripted group (container) (typed FeaturePython)
  n = 0.573748
FEATURE [App::DocumentObjectGroupPython] I_element007  label="I_element : 0.649"  # scripted group (container) (typed FeaturePython)
  n = 0.003357
FEATURE [App::DocumentObjectGroupPython] G4_SILVER_HALIDES  # scripted group (container) (typed FeaturePython)
  Dunit = g/cm3
  Dvalue = 6.47
  Group = -> [Br_element006,Ag_element004,I_element007]
  conduct = 2
  density = 1
  expand = 3
  formula = G4_SILVER_HALIDES
  name = G4_SILVER_HALIDES
  specific = 4
FEATURE [App::DocumentObjectGroupPython] Ag_element005  label="Ag_element : 003"  # scripted group (container) (typed FeaturePython)
  n = 1
  ref = Ag_element
FEATURE [App::DocumentObjectGroupPython] I_element008  label="I_element : 004"  # scripted group (container) (typed FeaturePython)
  n = 1
  ref = I_element
FEATURE [App::DocumentObjectGroupPython] G4_SILVER_IODIDE  # scripted group (container) (typed FeaturePython)
  Dunit = g/cm3
  Dvalue = 6.01
  Group = -> [Ag_element005,I_element008]
  conduct = 2
  density = 1
  expand = 3
  formula = G4_SILVER_IODIDE
  name = G4_SILVER_IODIDE
  specific = 4
FEATURE [App::DocumentObjectGroupPython] H_element095  label="H_element : 0.100"  # scripted group (container) (typed FeaturePython)
  n = 0.1
FEATURE [App::DocumentObjectGroupPython] C_element103  label="C_element : 0.204"  # scripted group (container) (typed FeaturePython)
  n = 0.204
FEATURE [App::DocumentObjectGroupPython] N_element039  label="N_element : 0.759"  # scripted group (container) (typed FeaturePython)
  n = 0.042
FEATURE [App::DocumentObjectGroupPython] O_element088  label="O_element : 0.645"  # scripted group (container) (typed FeaturePython)
  n = 0.645
FEATURE [App::DocumentObjectGroupPython] Na_element013  label="Na_element : 0.100"  # scripted group (container) (typed FeaturePython)
  n = 0.002
FEATURE [App::DocumentObjectGroupPython] P_element009  label="P_element : 0.107"  # scripted group (container) (typed FeaturePython)
  n = 0.001
FEATURE [App::DocumentObjectGroupPython] S_element020  label="S_element : 0.021"  # scripted group (container) (typed FeaturePython)
  n = 0.002
FEATURE [App::DocumentObjectGroupPython] Cl_element023  label="Cl_element : 0.590"  # scripted group (container) (typed FeaturePython)
  n = 0.003
FEATURE [App::DocumentObjectGroupPython] K_element010  label="K_element : 0.001"  # scripted group (container) (typed FeaturePython)
  n = 0.001
FEATURE [App::DocumentObjectGroupPython] G4_SKIN_ICRP  # scripted group (container) (typed FeaturePython)
  Dunit = g/cm3
  Dvalue = 1.09
  Group = -> [H_element095,C_element103,N_element039,O_element088,Na_element013,P_element009,S_element020,Cl_element023,K_element010]
  conduct = 2
  density = 1
  expand = 3
  formula = G4_SKIN_ICRP
  name = G4_SKIN_ICRP
  specific = 4
FEATURE [App::DocumentObjectGroupPython] Na_element014  label="Na_element : 2"  # scripted group (container) (typed FeaturePython)
  n = 2
  ref = Na_element
FEATURE [App::DocumentObjectGroupPython] C_element104  label="C_element : 058"  # scripted group (container) (typed FeaturePython)
  n = 1
  ref = C_element
FEATURE [App::DocumentObjectGroupPython] O_element089  label="O_element : 049"  # scripted group (container) (typed FeaturePython)
  n = 3
  ref = O_element
FEATURE [App::DocumentObjectGroupPython] G4_SODIUM_CARBONATE  # scripted group (container) (typed FeaturePython)
  Dunit = g/cm3
  Dvalue = 2.532
  Group = -> [Na_element014,C_element104,O_element089]
  conduct = 2
  density = 1
  expand = 3
  formula = G4_SODIUM_CARBONATE
  name = G4_SODIUM_CARBONATE
  specific = 4
FEATURE [App::DocumentObjectGroupPython] Na_element015  label="Na_element : 1"  # scripted group (container) (typed FeaturePython)
  n = 1
  ref = Na_element
FEATURE [App::DocumentObjectGroupPython] I_element009  label="I_element : 005"  # scripted group (container) (typed FeaturePython)
  n = 1
  ref = I_element
FEATURE [App::DocumentObjectGroupPython] G4_SODIUM_IODIDE  # scripted group (container) (typed FeaturePython)
  Dunit = g/cm3
  Dvalue = 3.667
  Group = -> [Na_element015,I_element009]
  conduct = 2
  density = 1
  expand = 3
  formula = G4_SODIUM_IODIDE
  name = G4_SODIUM_IODIDE
  specific = 4
FEATURE [App::DocumentObjectGroupPython] Na_element016  label="Na_element : 003"  # scripted group (container) (typed FeaturePython)
  n = 2
  ref = Na_element
FEATURE [App::DocumentObjectGroupPython] O_element090  label="O_element : 050"  # scripted group (container) (typed FeaturePython)
  n = 1
  ref = O_element
FEATURE [App::DocumentObjectGroupPython] G4_SODIUM_MONOXIDE  # scripted group (container) (typed FeaturePython)
  Dunit = g/cm3
  Dvalue = 2.27
  Group = -> [Na_element016,O_element090]
  conduct = 2
  density = 1
  expand = 3
  formula = G4_SODIUM_MONOXIDE
  name = G4_SODIUM_MONOXIDE
  specific = 4
FEATURE [App::DocumentObjectGroupPython] Na_element017  label="Na_element : 004"  # scripted group (container) (typed FeaturePython)
  n = 1
  ref = Na_element
FEATURE [App::DocumentObjectGroupPython] N_element040  label="N_element : 018"  # scripted group (container) (typed FeaturePython)
  n = 1
  ref = N_element
FEATURE [App::DocumentObjectGroupPython] O_element091  label="O_element : 051"  # scripted group (container) (typed FeaturePython)
  n = 3
  ref = O_element
FEATURE [App::DocumentObjectGroupPython] G4_SODIUM_NITRATE  # scripted group (container) (typed FeaturePython)
  Dunit = g/cm3
  Dvalue = 2.261
  Group = -> [Na_element017,N_element040,O_element091]
  conduct = 2
  density = 1
  expand = 3
  formula = G4_SODIUM_NITRATE
  name = G4_SODIUM_NITRATE
  specific = 4
FEATURE [App::DocumentObjectGroupPython] C_element105  label="C_element : 059"  # scripted group (container) (typed FeaturePython)
  n = 14
  ref = C_element
FEATURE [App::DocumentObjectGroupPython] H_element096  label="H_element : 053"  # scripted group (container) (typed FeaturePython)
  n = 12
  ref = H_element
FEATURE [App::DocumentObjectGroupPython] G4_STILBENE  # scripted group (container) (typed FeaturePython)
  Dunit = g/cm3
  Dvalue = 0.9707
  Group = -> [C_element105,H_element096]
  conduct = 2
  density = 1
  expand = 3
  formula = G4_STILBENE
  name = G4_STILBENE
  specific = 4
FEATURE [App::DocumentObjectGroupPython] C_element106  label="C_element : 12"  # scripted group (container) (typed FeaturePython)
  n = 12
  ref = C_element
FEATURE [App::DocumentObjectGroupPython] H_element097  label="H_element : 22"  # scripted group (container) (typed FeaturePython)
  n = 22
  ref = H_element
FEATURE [App::DocumentObjectGroupPython] O_element092  label="O_element : 11"  # scripted group (container) (typed FeaturePython)
  n = 11
  ref = O_element
FEATURE [App::DocumentObjectGroupPython] G4_SUCROSE  # scripted group (container) (typed FeaturePython)
  Dunit = g/cm3
  Dvalue = 1.5805
  Group = -> [C_element106,H_element097,O_element092]
  conduct = 2
  density = 1
  expand = 3
  formula = G4_SUCROSE
  name = G4_SUCROSE
  specific = 4
FEATURE [App::DocumentObjectGroupPython] C_element107  label="C_element : 18"  # scripted group (container) (typed FeaturePython)
  n = 18
  ref = C_element
FEATURE [App::DocumentObjectGroupPython] H_element098  label="H_element : 054"  # scripted group (container) (typed FeaturePython)
  n = 14
  ref = H_element
FEATURE [App::DocumentObjectGroupPython] G4_TERPHENYL  # scripted group (container) (typed FeaturePython)
  Dunit = g/cm3
  Dvalue = 1.24
  Group = -> [C_element107,H_element098]
  conduct = 2
  density = 1
  expand = 3
  formula = G4_TERPHENYL
  name = G4_TERPHENYL
  specific = 4
FEATURE [App::DocumentObjectGroupPython] H_element099  label="H_element : 0.146"  # scripted group (container) (typed FeaturePython)
  n = 0.106
FEATURE [App::DocumentObjectGroupPython] C_element108  label="C_element : 0.883"  # scripted group (container) (typed FeaturePython)
  n = 0.099
FEATURE [App::DocumentObjectGroupPython] N_element041  label="N_element : 0.020"  # scripted group (container) (typed FeaturePython)
  n = 0.02
FEATURE [App::DocumentObjectGroupPython] O_element093  label="O_element : 0.766"  # scripted group (container) (typed FeaturePython)
  n = 0.766
FEATURE [App::DocumentObjectGroupPython] Na_element018  label="Na_element : 0.101"  # scripted group (container) (typed FeaturePython)
  n = 0.002
FEATURE [App::DocumentObjectGroupPython] P_element010  label="P_element : 0.108"  # scripted group (container) (typed FeaturePython)
  n = 0.001
FEATURE [App::DocumentObjectGroupPython] S_element021  label="S_element : 0.022"  # scripted group (container) (typed FeaturePython)
  n = 0.002
FEATURE [App::DocumentObjectGroupPython] Cl_element024  label="Cl_element : 0.002"  # scripted group (container) (typed FeaturePython)
  n = 0.002
FEATURE [App::DocumentObjectGroupPython] K_element011  label="K_element : 0.017"  # scripted group (container) (typed FeaturePython)
  n = 0.002
FEATURE [App::DocumentObjectGroupPython] G4_TESTIS_ICRP  # scripted group (container) (typed FeaturePython)
  Dunit = g/cm3
  Dvalue = 1.04
  Group = -> [H_element099,C_element108,N_element041,O_element093,Na_element018,P_element010,S_element021,Cl_element024,K_element011]
  conduct = 2
  density = 1
  expand = 3
  formula = G4_TESTIS_ICRP
  name = G4_TESTIS_ICRP
  specific = 4
FEATURE [App::DocumentObjectGroupPython] C_element109  label="C_element : 060"  # scripted group (container) (typed FeaturePython)
  n = 2
  ref = C_element
FEATURE [App::DocumentObjectGroupPython] Cl_element025  label="Cl_element : 012"  # scripted group (container) (typed FeaturePython)
  n = 4
  ref = Cl_element
FEATURE [App::DocumentObjectGroupPython] G4_TETRACHLOROETHYLENE  # scripted group (container) (typed FeaturePython)
  Dunit = g/cm3
  Dvalue = 1.625
  Group = -> [C_element109,Cl_element025]
  conduct = 2
  density = 1
  expand = 3
  formula = G4_TETRACHLOROETHYLENE
  name = G4_TETRACHLOROETHYLENE
  specific = 4
FEATURE [App::DocumentObjectGroupPython] Tl_element001  label="Tl_element : 1"  # scripted group (container) (typed FeaturePython)
  n = 1
  ref = Tl_element
FEATURE [App::DocumentObjectGroupPython] Cl_element026  label="Cl_element : 013"  # scripted group (container) (typed FeaturePython)
  n = 1
  ref = Cl_element
FEATURE [App::DocumentObjectGroupPython] G4_THALLIUM_CHLORIDE  # scripted group (container) (typed FeaturePython)
  Dunit = g/cm3
  Dvalue = 7.004
  Group = -> [Tl_element001,Cl_element026]
  conduct = 2
  density = 1
  expand = 3
  formula = G4_THALLIUM_CHLORIDE
  name = G4_THALLIUM_CHLORIDE
  specific = 4
FEATURE [App::DocumentObjectGroupPython] H_element100  label="H_element : 0.147"  # scripted group (container) (typed FeaturePython)
  n = 0.105
FEATURE [App::DocumentObjectGroupPython] C_element110  label="C_element : 0.256"  # scripted group (container) (typed FeaturePython)
  n = 0.256
FEATURE [App::DocumentObjectGroupPython] N_element042  label="N_element : 0.760"  # scripted group (container) (typed FeaturePython)
  n = 0.027
FEATURE [App::DocumentObjectGroupPython] O_element094  label="O_element : 0.602"  # scripted group (container) (typed FeaturePython)
  n = 0.602
FEATURE [App::DocumentObjectGroupPython] Na_element019  label="Na_element : 0.102"  # scripted group (container) (typed FeaturePython)
  n = 0.001
FEATURE [App::DocumentObjectGroupPython] P_element011  label="P_element : 0.109"  # scripted group (container) (typed FeaturePython)
  n = 0.002
FEATURE [App::DocumentObjectGroupPython] S_element022  label="S_element : 0.023"  # scripted group (container) (typed FeaturePython)
  n = 0.003
FEATURE [App::DocumentObjectGroupPython] Cl_element027  label="Cl_element : 0.591"  # scripted group (container) (typed FeaturePython)
  n = 0.002
FEATURE [App::DocumentObjectGroupPython] K_element012  label="K_element : 0.018"  # scripted group (container) (typed FeaturePython)
  n = 0.002
FEATURE [App::DocumentObjectGroupPython] G4_TISSUE_SOFT_ICRP  # scripted group (container) (typed FeaturePython)
  Dunit = g/cm3
  Dvalue = 1.03
  Group = -> [H_element100,C_element110,N_element042,O_element094,Na_element019,P_element011,S_element022,Cl_element027,K_element012]
  conduct = 2
  density = 1
  expand = 3
  formula = G4_TISSUE_SOFT_ICRP
  name = G4_TISSUE_SOFT_ICRP
  specific = 4
FEATURE [App::DocumentObjectGroupPython] H_element101  label="H_element : 0.148"  # scripted group (container) (typed FeaturePython)
  n = 0.101
FEATURE [App::DocumentObjectGroupPython] C_element111  label="C_element : 0.111"  # scripted group (container) (typed FeaturePython)
  n = 0.111
FEATURE [App::DocumentObjectGroupPython] N_element043  label="N_element : 0.026"  # scripted group (container) (typed FeaturePython)
  n = 0.026
FEATURE [App::DocumentObjectGroupPython] O_element095  label="O_element : 0.762"  # scripted group (container) (typed FeaturePython)
  n = 0.762
FEATURE [App::DocumentObjectGroupPython] G4_TISSUE_SOFT_ICRU_4  label="G4_TISSUE_SOFT_ICRU-4"  # scripted group (container) (typed FeaturePython)
  Dunit = g/cm3
  Dvalue = 1
  Group = -> [H_element101,C_element111,N_element043,O_element095]
  conduct = 2
  density = 1
  expand = 3
  formula = G4_TISSUE_SOFT_ICRU-4
  name = G4_TISSUE_SOFT_ICRU-4
  specific = 4
FEATURE [App::DocumentObjectGroupPython] H_element102  label="H_element : 0.149"  # scripted group (container) (typed FeaturePython)
  n = 0.101869
FEATURE [App::DocumentObjectGroupPython] C_element112  label="C_element : 0.456"  # scripted group (container) (typed FeaturePython)
  n = 0.456179
FEATURE [App::DocumentObjectGroupPython] N_element044  label="N_element : 0.761"  # scripted group (container) (typed FeaturePython)
  n = 0.035172
FEATURE [App::DocumentObjectGroupPython] O_element096  label="O_element : 0.407"  # scripted group (container) (typed FeaturePython)
  n = 0.40678
FEATURE [App::DocumentObjectGroupPython] G4_TISSUE_METHANE  label="G4_TISSUE-METHANE"  # scripted group (container) (typed FeaturePython)
  Dunit = g/cm3
  Dvalue = 0.00106409
  Group = -> [H_element102,C_element112,N_element044,O_element096]
  conduct = 2
  density = 1
  expand = 3
  formula = G4_TISSUE-METHANE
  name = G4_TISSUE-METHANE
  specific = 4
FEATURE [App::DocumentObjectGroupPython] H_element103  label="H_element : 0.103"  # scripted group (container) (typed FeaturePython)
  n = 0.102672
FEATURE [App::DocumentObjectGroupPython] C_element113  label="C_element : 0.569"  # scripted group (container) (typed FeaturePython)
  n = 0.56894
FEATURE [App::DocumentObjectGroupPython] N_element045  label="N_element : 0.762"  # scripted group (container) (typed FeaturePython)
  n = 0.035022
FEATURE [App::DocumentObjectGroupPython] O_element097  label="O_element : 0.293"  # scripted group (container) (typed FeaturePython)
  n = 0.293366
FEATURE [App::DocumentObjectGroupPython] G4_TISSUE_PROPANE  label="G4_TISSUE-PROPANE"  # scripted group (container) (typed FeaturePython)
  Dunit = g/cm3
  Dvalue = 0.00182628
  Group = -> [H_element103,C_element113,N_element045,O_element097]
  conduct = 2
  density = 1
  expand = 3
  formula = G4_TISSUE-PROPANE
  name = G4_TISSUE-PROPANE
  specific = 4
FEATURE [App::DocumentObjectGroupPython] Ti_element003  label="Ti_element : 1"  # scripted group (container) (typed FeaturePython)
  n = 1
  ref = Ti_element
FEATURE [App::DocumentObjectGroupPython] O_element098  label="O_element : 052"  # scripted group (container) (typed FeaturePython)
  n = 2
  ref = O_element
FEATURE [App::DocumentObjectGroupPython] G4_TITANIUM_DIOXIDE  # scripted group (container) (typed FeaturePython)
  Dunit = g/cm3
  Dvalue = 4.26
  Group = -> [Ti_element003,O_element098]
  conduct = 2
  density = 1
  expand = 3
  formula = G4_TITANIUM_DIOXIDE
  name = G4_TITANIUM_DIOXIDE
  specific = 4
FEATURE [App::DocumentObjectGroupPython] C_element114  label="C_element : 061"  # scripted group (container) (typed FeaturePython)
  n = 7
  ref = C_element
FEATURE [App::DocumentObjectGroupPython] H_element104  label="H_element : 055"  # scripted group (container) (typed FeaturePython)
  n = 8
  ref = H_element
FEATURE [App::DocumentObjectGroupPython] G4_TOLUENE  # scripted group (container) (typed FeaturePython)
  Dunit = g/cm3
  Dvalue = 0.8669
  Group = -> [C_element114,H_element104]
  conduct = 2
  density = 1
  expand = 3
  formula = G4_TOLUENE
  name = G4_TOLUENE
  specific = 4
FEATURE [App::DocumentObjectGroupPython] C_element115  label="C_element : 062"  # scripted group (container) (typed FeaturePython)
  n = 2
  ref = C_element
FEATURE [App::DocumentObjectGroupPython] H_element105  label="H_element : 056"  # scripted group (container) (typed FeaturePython)
  n = 1
  ref = H_element
FEATURE [App::DocumentObjectGroupPython] Cl_element028  label="Cl_element : 014"  # scripted group (container) (typed FeaturePython)
  n = 3
  ref = Cl_element
FEATURE [App::DocumentObjectGroupPython] G4_TRICHLOROETHYLENE  # scripted group (container) (typed FeaturePython)
  Dunit = g/cm3
  Dvalue = 1.46
  Group = -> [C_element115,H_element105,Cl_element028]
  conduct = 2
  density = 1
  expand = 3
  formula = G4_TRICHLOROETHYLENE
  name = G4_TRICHLOROETHYLENE
  specific = 4
FEATURE [App::DocumentObjectGroupPython] C_element116  label="C_element : 063"  # scripted group (container) (typed FeaturePython)
  n = 6
  ref = C_element
FEATURE [App::DocumentObjectGroupPython] H_element106  label="H_element : 15"  # scripted group (container) (typed FeaturePython)
  n = 15
  ref = H_element
FEATURE [App::DocumentObjectGroupPython] O_element099  label="O_element : 053"  # scripted group (container) (typed FeaturePython)
  n = 4
  ref = O_element
FEATURE [App::DocumentObjectGroupPython] P_element012  label="P_element : 1"  # scripted group (container) (typed FeaturePython)
  n = 1
  ref = P_element
FEATURE [App::DocumentObjectGroupPython] G4_TRIETHYL_PHOSPHATE  # scripted group (container) (typed FeaturePython)
  Dunit = g/cm3
  Dvalue = 1.07
  Group = -> [C_element116,H_element106,O_element099,P_element012]
  conduct = 2
  density = 1
  expand = 3
  formula = G4_TRIETHYL_PHOSPHATE
  name = G4_TRIETHYL_PHOSPHATE
  specific = 4
FEATURE [App::DocumentObjectGroupPython] W_element003  label="W_element : 003"  # scripted group (container) (typed FeaturePython)
  n = 1
  ref = W_element
FEATURE [App::DocumentObjectGroupPython] F_element017  label="F_element : 6"  # scripted group (container) (typed FeaturePython)
  n = 6
  ref = F_element
FEATURE [App::DocumentObjectGroupPython] G4_TUNGSTEN_HEXAFLUORIDE  # scripted group (container) (typed FeaturePython)
  Dunit = g/cm3
  Dvalue = 2.4
  Group = -> [W_element003,F_element017]
  conduct = 2
  density = 1
  expand = 3
  formula = G4_TUNGSTEN_HEXAFLUORIDE
  name = G4_TUNGSTEN_HEXAFLUORIDE
  specific = 4
FEATURE [App::DocumentObjectGroupPython] U_element001  label="U_element : 1"  # scripted group (container) (typed FeaturePython)
  n = 1
  ref = U_element
FEATURE [App::DocumentObjectGroupPython] C_element117  label="C_element : 064"  # scripted group (container) (typed FeaturePython)
  n = 2
  ref = C_element
FEATURE [App::DocumentObjectGroupPython] G4_URANIUM_DICARBIDE  # scripted group (container) (typed FeaturePython)
  Dunit = g/cm3
  Dvalue = 11.28
  Group = -> [U_element001,C_element117]
  conduct = 2
  density = 1
  expand = 3
  formula = G4_URANIUM_DICARBIDE
  name = G4_URANIUM_DICARBIDE
  specific = 4
FEATURE [App::DocumentObjectGroupPython] U_element002  label="U_element : 002"  # scripted group (container) (typed FeaturePython)
  n = 1
  ref = U_element
FEATURE [App::DocumentObjectGroupPython] C_element118  label="C_element : 065"  # scripted group (container) (typed FeaturePython)
  n = 1
  ref = C_element
FEATURE [App::DocumentObjectGroupPython] G4_URANIUM_MONOCARBIDE  # scripted group (container) (typed FeaturePython)
  Dunit = g/cm3
  Dvalue = 13.63
  Group = -> [U_element002,C_element118]
  conduct = 2
  density = 1
  expand = 3
  formula = G4_URANIUM_MONOCARBIDE
  name = G4_URANIUM_MONOCARBIDE
  specific = 4
FEATURE [App::DocumentObjectGroupPython] U_element003  label="U_element : 003"  # scripted group (container) (typed FeaturePython)
  n = 1
  ref = U_element
FEATURE [App::DocumentObjectGroupPython] O_element100  label="O_element : 054"  # scripted group (container) (typed FeaturePython)
  n = 2
  ref = O_element
FEATURE [App::DocumentObjectGroupPython] G4_URANIUM_OXIDE  # scripted group (container) (typed FeaturePython)
  Dunit = g/cm3
  Dvalue = 10.96
  Group = -> [U_element003,O_element100]
  conduct = 2
  density = 1
  expand = 3
  formula = G4_URANIUM_OXIDE
  name = G4_URANIUM_OXIDE
  specific = 4
FEATURE [App::DocumentObjectGroupPython] C_element119  label="C_element : 066"  # scripted group (container) (typed FeaturePython)
  n = 1
  ref = C_element
FEATURE [App::DocumentObjectGroupPython] H_element107  label="H_element : 057"  # scripted group (container) (typed FeaturePython)
  n = 4
  ref = H_element
FEATURE [App::DocumentObjectGroupPython] N_element046  label="N_element : 019"  # scripted group (container) (typed FeaturePython)
  n = 2
  ref = N_element
FEATURE [App::DocumentObjectGroupPython] O_element101  label="O_element : 055"  # scripted group (container) (typed FeaturePython)
  n = 1
  ref = O_element
FEATURE [App::DocumentObjectGroupPython] G4_UREA  # scripted group (container) (typed FeaturePython)
  Dunit = g/cm3
  Dvalue = 1.323
  Group = -> [C_element119,H_element107,N_element046,O_element101]
  conduct = 2
  density = 1
  expand = 3
  formula = G4_UREA
  name = G4_UREA
  specific = 4
FEATURE [App::DocumentObjectGroupPython] C_element120  label="C_element : 067"  # scripted group (container) (typed FeaturePython)
  n = 5
  ref = C_element
FEATURE [App::DocumentObjectGroupPython] H_element108  label="H_element : 058"  # scripted group (container) (typed FeaturePython)
  n = 11
  ref = H_element
FEATURE [App::DocumentObjectGroupPython] N_element047  label="N_element : 020"  # scripted group (container) (typed FeaturePython)
  n = 1
  ref = N_element
FEATURE [App::DocumentObjectGroupPython] O_element102  label="O_element : 056"  # scripted group (container) (typed FeaturePython)
  n = 2
  ref = O_element
FEATURE [App::DocumentObjectGroupPython] G4_VALINE  # scripted group (container) (typed FeaturePython)
  Dunit = g/cm3
  Dvalue = 1.23
  Group = -> [C_element120,H_element108,N_element047,O_element102]
  conduct = 2
  density = 1
  expand = 3
  formula = G4_VALINE
  name = G4_VALINE
  specific = 4
FEATURE [App::DocumentObjectGroupPython] H_element109  label="H_element : 0.009"  # scripted group (container) (typed FeaturePython)
  n = 0.009417
FEATURE [App::DocumentObjectGroupPython] C_element121  label="C_element : 0.281"  # scripted group (container) (typed FeaturePython)
  n = 0.280555
FEATURE [App::DocumentObjectGroupPython] F_element018  label="F_element : 0.710"  # scripted group (container) (typed FeaturePython)
  n = 0.710028
FEATURE [App::DocumentObjectGroupPython] G4_VITON  # scripted group (container) (typed FeaturePython)
  Dunit = g/cm3
  Dvalue = 1.8
  Group = -> [H_element109,C_element121,F_element018]
  conduct = 2
  density = 1
  expand = 3
  formula = G4_VITON
  name = G4_VITON
  specific = 4
FEATURE [App::DocumentObjectGroupPython] H_element110  label="H_element : 059"  # scripted group (container) (typed FeaturePython)
  n = 2
  ref = H_element
FEATURE [App::DocumentObjectGroupPython] O_element103  label="O_element : 057"  # scripted group (container) (typed FeaturePython)
  n = 1
  ref = O_element
FEATURE [App::DocumentObjectGroupPython] G4_WATER  # scripted group (container) (typed FeaturePython)
  Dunit = g/cm3
  Dvalue = 1
  Group = -> [H_element110,O_element103]
  conduct = 2
  density = 1
  expand = 3
  formula = G4_WATER
  name = G4_WATER
  specific = 4
FEATURE [App::DocumentObjectGroupPython] H_element111  label="H_element : 060"  # scripted group (container) (typed FeaturePython)
  n = 2
  ref = H_element
FEATURE [App::DocumentObjectGroupPython] O_element104  label="O_element : 058"  # scripted group (container) (typed FeaturePython)
  n = 1
  ref = O_element
FEATURE [App::DocumentObjectGroupPython] G4_WATER_VAPOR  # scripted group (container) (typed FeaturePython)
  Dunit = g/cm3
  Dvalue = 0.000756182
  Group = -> [H_element111,O_element104]
  conduct = 2
  density = 1
  expand = 3
  formula = G4_WATER_VAPOR
  name = G4_WATER_VAPOR
  specific = 4
FEATURE [App::DocumentObjectGroupPython] C_element122  label="C_element : 068"  # scripted group (container) (typed FeaturePython)
  n = 8
  ref = C_element
FEATURE [App::DocumentObjectGroupPython] H_element112  label="H_element : 061"  # scripted group (container) (typed FeaturePython)
  n = 10
  ref = H_element
FEATURE [App::DocumentObjectGroupPython] G4_XYLENE  # scripted group (container) (typed FeaturePython)
  Dunit = g/cm3
  Dvalue = 0.87
  Group = -> [C_element122,H_element112]
  conduct = 2
  density = 1
  expand = 3
  formula = G4_XYLENE
  name = G4_XYLENE
  specific = 4
FEATURE [App::DocumentObjectGroupPython] C_element123  label="C_element : 069"  # scripted group (container) (typed FeaturePython)
  n = 1
  ref = C_element
FEATURE [App::DocumentObjectGroupPython] G4_GRAPHITE  # scripted group (container) (typed FeaturePython)
  Dunit = g/cm3
  Dvalue = 2.21
  Group = -> [C_element123]
  conduct = 2
  density = 1
  expand = 3
  formula = G4_GRAPHITE
  name = G4_GRAPHITE
  specific = 4
FEATURE [App::DocumentObjectGroupPython] NIST  # scripted group (container) (typed FeaturePython)
  Group = -> [G4_A_150_TISSUE,G4_ACETONE,G4_ACETYLENE,G4_ADENINE,G4_ADIPOSE_TISSUE_ICRP,G4_AIR,G4_ALANINE,G4_ALUMINUM_OXIDE,G4_AMBER,G4_AMMONIA,G4_ANILINE,G4_ANTHRACENE,G4_B_100_BONE,G4_BAKELITE,G4_BARIUM_FLUORIDE,G4_BARIUM_SULFATE,G4_BENZENE,G4_BERYLLIUM_OXIDE,G4_BGO,G4_BLOOD_ICRP,G4_BONE_COMPACT_ICRU,G4_BONE_CORTICAL_ICRP,G4_BORON_CARBIDE,G4_BORON_OXIDE,G4_BRAIN_ICRP,G4_BUTANE,G4_N_BUTYL_ALCOHOL,G4_C_552,+152 more]
FEATURE [App::DocumentObjectGroupPython] H_element113  label="H_element : 062"  # scripted group (container) (typed FeaturePython)
  n = 1
  ref = H_element
FEATURE [App::DocumentObjectGroupPython] G4_H  # scripted group (container) (typed FeaturePython)
  Dunit = g/cm3
  Dvalue = 8.3748e-05
  Group = -> [H_element113]
  conduct = 2
  density = 1
  expand = 3
  formula = H
  name = G4_H
  specific = 4
FEATURE [App::DocumentObjectGroupPython] He_element001  label="He_element : 1"  # scripted group (container) (typed FeaturePython)
  n = 1
  ref = He_element
FEATURE [App::DocumentObjectGroupPython] G4_He  # scripted group (container) (typed FeaturePython)
  Dunit = g/cm3
  Dvalue = 0.000166322
  Group = -> [He_element001]
  conduct = 2
  density = 1
  expand = 3
  formula = He
  name = G4_He
  specific = 4
FEATURE [App::DocumentObjectGroupPython] Li_element008  label="Li_element : 008"  # scripted group (container) (typed FeaturePython)
  n = 1
  ref = Li_element
FEATURE [App::DocumentObjectGroupPython] G4_Li  # scripted group (container) (typed FeaturePython)
  Dunit = g/cm3
  Dvalue = 0.534
  Group = -> [Li_element008]
  conduct = 2
  density = 1
  expand = 3
  formula = Li
  name = G4_Li
  specific = 4
FEATURE [App::DocumentObjectGroupPython] Be_element002  label="Be_element : 002"  # scripted group (container) (typed FeaturePython)
  n = 1
  ref = Be_element
FEATURE [App::DocumentObjectGroupPython] G4_Be  # scripted group (container) (typed FeaturePython)
  Dunit = g/cm3
  Dvalue = 1.848
  Group = -> [Be_element002]
  conduct = 2
  density = 1
  expand = 3
  formula = Be
  name = G4_Be
  specific = 4
FEATURE [App::DocumentObjectGroupPython] B_element007  label="B_element : 007"  # scripted group (container) (typed FeaturePython)
  n = 1
  ref = B_element
FEATURE [App::DocumentObjectGroupPython] G4_B  # scripted group (container) (typed FeaturePython)
  Dunit = g/cm3
  Dvalue = 2.37
  Group = -> [B_element007]
  conduct = 2
  density = 1
  expand = 3
  formula = B
  name = G4_B
  specific = 4
FEATURE [App::DocumentObjectGroupPython] C_element124  label="C_element : 070"  # scripted group (container) (typed FeaturePython)
  n = 1
  ref = C_element
FEATURE [App::DocumentObjectGroupPython] G4_C  # scripted group (container) (typed FeaturePython)
  Dunit = g/cm3
  Dvalue = 2
  Group = -> [C_element124]
  conduct = 2
  density = 1
  expand = 3
  formula = C
  name = G4_C
  specific = 4
FEATURE [App::DocumentObjectGroupPython] N_element048  label="N_element : 021"  # scripted group (container) (typed FeaturePython)
  n = 1
  ref = N_element
FEATURE [App::DocumentObjectGroupPython] G4_N  # scripted group (container) (typed FeaturePython)
  Dunit = g/cm3
  Dvalue = 0.0011652
  Group = -> [N_element048]
  conduct = 2
  density = 1
  expand = 3
  formula = N
  name = G4_N
  specific = 4
FEATURE [App::DocumentObjectGroupPython] O_element105  label="O_element : 059"  # scripted group (container) (typed FeaturePython)
  n = 1
  ref = O_element
FEATURE [App::DocumentObjectGroupPython] G4_O  # scripted group (container) (typed FeaturePython)
  Dunit = g/cm3
  Dvalue = 0.00133151
  Group = -> [O_element105]
  conduct = 2
  density = 1
  expand = 3
  formula = O
  name = G4_O
  specific = 4
FEATURE [App::DocumentObjectGroupPython] F_element019  label="F_element : 008"  # scripted group (container) (typed FeaturePython)
  n = 1
  ref = F_element
FEATURE [App::DocumentObjectGroupPython] G4_F  # scripted group (container) (typed FeaturePython)
  Dunit = g/cm3
  Dvalue = 0.00158029
  Group = -> [F_element019]
  conduct = 2
  density = 1
  expand = 3
  formula = F
  name = G4_F
  specific = 4
FEATURE [App::DocumentObjectGroupPython] Ne_element001  label="Ne_element : 1"  # scripted group (container) (typed FeaturePython)
  n = 1
  ref = Ne_element
FEATURE [App::DocumentObjectGroupPython] G4_Ne  # scripted group (container) (typed FeaturePython)
  Dunit = g/cm3
  Dvalue = 0.000838505
  Group = -> [Ne_element001]
  conduct = 2
  density = 1
  expand = 3
  formula = Ne
  name = G4_Ne
  specific = 4
FEATURE [App::DocumentObjectGroupPython] Na_element020  label="Na_element : 005"  # scripted group (container) (typed FeaturePython)
  n = 1
  ref = Na_element
FEATURE [App::DocumentObjectGroupPython] G4_Na  # scripted group (container) (typed FeaturePython)
  Dunit = g/cm3
  Dvalue = 0.971
  Group = -> [Na_element020]
  conduct = 2
  density = 1
  expand = 3
  formula = Na
  name = G4_Na
  specific = 4
FEATURE [App::DocumentObjectGroupPython] Mg_element011  label="Mg_element : 005"  # scripted group (container) (typed FeaturePython)
  n = 1
  ref = Mg_element
FEATURE [App::DocumentObjectGroupPython] G4_Mg  # scripted group (container) (typed FeaturePython)
  Dunit = g/cm3
  Dvalue = 1.74
  Group = -> [Mg_element011]
  conduct = 2
  density = 1
  expand = 3
  formula = Mg
  name = G4_Mg
  specific = 4
FEATURE [App::DocumentObjectGroupPython] Al_element004  label="Al_element : 1"  # scripted group (container) (typed FeaturePython)
  n = 1
  ref = Al_element
FEATURE [App::DocumentObjectGroupPython] G4_Al  # scripted group (container) (typed FeaturePython)
  Dunit = g/cm3
  Dvalue = 2.699
  Group = -> [Al_element004]
  conduct = 2
  density = 1
  expand = 3
  formula = Al
  name = G4_Al
  specific = 4
FEATURE [App::DocumentObjectGroupPython] Si_element007  label="Si_element : 002"  # scripted group (container) (typed FeaturePython)
  n = 1
  ref = Si_element
FEATURE [App::DocumentObjectGroupPython] G4_Si  # scripted group (container) (typed FeaturePython)
  Dunit = g/cm3
  Dvalue = 2.33
  Group = -> [Si_element007]
  conduct = 2
  density = 1
  expand = 3
  formula = Si
  name = G4_Si
  specific = 4
FEATURE [App::DocumentObjectGroupPython] P_element013  label="P_element : 002"  # scripted group (container) (typed FeaturePython)
  n = 1
  ref = P_element
FEATURE [App::DocumentObjectGroupPython] G4_P  # scripted group (container) (typed FeaturePython)
  Dunit = g/cm3
  Dvalue = 2.2
  Group = -> [P_element013]
  conduct = 2
  density = 1
  expand = 3
  formula = P
  name = G4_P
  specific = 4
FEATURE [App::DocumentObjectGroupPython] S_element023  label="S_element : 007"  # scripted group (container) (typed FeaturePython)
  n = 1
  ref = S_element
FEATURE [App::DocumentObjectGroupPython] G4_S  # scripted group (container) (typed FeaturePython)
  Dunit = g/cm3
  Dvalue = 2
  Group = -> [S_element023]
  conduct = 2
  density = 1
  expand = 3
  formula = S
  name = G4_S
  specific = 4
FEATURE [App::DocumentObjectGroupPython] Cl_element029  label="Cl_element : 015"  # scripted group (container) (typed FeaturePython)
  n = 1
  ref = Cl_element
FEATURE [App::DocumentObjectGroupPython] G4_Cl  # scripted group (container) (typed FeaturePython)
  Dunit = g/cm3
  Dvalue = 0.00299473
  Group = -> [Cl_element029]
  conduct = 2
  density = 1
  expand = 3
  formula = Cl
  name = G4_Cl
  specific = 4
FEATURE [App::DocumentObjectGroupPython] Ar_element002  label="Ar_element : 1"  # scripted group (container) (typed FeaturePython)
  n = 1
  ref = Ar_element
FEATURE [App::DocumentObjectGroupPython] G4_Ar  # scripted group (container) (typed FeaturePython)
  Dunit = g/cm3
  Dvalue = 0.00166201
  Group = -> [Ar_element002]
  conduct = 2
  density = 1
  expand = 3
  formula = Ar
  name = G4_Ar
  specific = 4
FEATURE [App::DocumentObjectGroupPython] K_element013  label="K_element : 003"  # scripted group (container) (typed FeaturePython)
  n = 1
  ref = K_element
FEATURE [App::DocumentObjectGroupPython] G4_K  # scripted group (container) (typed FeaturePython)
  Dunit = g/cm3
  Dvalue = 0.862
  Group = -> [K_element013]
  conduct = 2
  density = 1
  expand = 3
  formula = K
  name = G4_K
  specific = 4
FEATURE [App::DocumentObjectGroupPython] Ca_element014  label="Ca_element : 007"  # scripted group (container) (typed FeaturePython)
  n = 1
  ref = Ca_element
FEATURE [App::DocumentObjectGroupPython] G4_Ca  # scripted group (container) (typed FeaturePython)
  Dunit = g/cm3
  Dvalue = 1.55
  Group = -> [Ca_element014]
  conduct = 2
  density = 1
  expand = 3
  formula = Ca
  name = G4_Ca
  specific = 4
FEATURE [App::DocumentObjectGroupPython] Sc_element001  label="Sc_element : 1"  # scripted group (container) (typed FeaturePython)
  n = 1
  ref = Sc_element
FEATURE [App::DocumentObjectGroupPython] G4_Sc  # scripted group (container) (typed FeaturePython)
  Dunit = g/cm3
  Dvalue = 2.989
  Group = -> [Sc_element001]
  conduct = 2
  density = 1
  expand = 3
  formula = Sc
  name = G4_Sc
  specific = 4
FEATURE [App::DocumentObjectGroupPython] Ti_element004  label="Ti_element : 002"  # scripted group (container) (typed FeaturePython)
  n = 1
  ref = Ti_element
FEATURE [App::DocumentObjectGroupPython] G4_Ti  # scripted group (container) (typed FeaturePython)
  Dunit = g/cm3
  Dvalue = 4.54
  Group = -> [Ti_element004]
  conduct = 2
  density = 1
  expand = 3
  formula = Ti
  name = G4_Ti
  specific = 4
FEATURE [App::DocumentObjectGroupPython] V_element001  label="V_element : 1"  # scripted group (container) (typed FeaturePython)
  n = 1
  ref = V_element
FEATURE [App::DocumentObjectGroupPython] G4_V  # scripted group (container) (typed FeaturePython)
  Dunit = g/cm3
  Dvalue = 6.11
  Group = -> [V_element001]
  conduct = 2
  density = 1
  expand = 3
  formula = V
  name = G4_V
  specific = 4
FEATURE [App::DocumentObjectGroupPython] Cr_element001  label="Cr_element : 1"  # scripted group (container) (typed FeaturePython)
  n = 1
  ref = Cr_element
FEATURE [App::DocumentObjectGroupPython] G4_Cr  # scripted group (container) (typed FeaturePython)
  Dunit = g/cm3
  Dvalue = 7.18
  Group = -> [Cr_element001]
  conduct = 2
  density = 1
  expand = 3
  formula = Cr
  name = G4_Cr
  specific = 4
FEATURE [App::DocumentObjectGroupPython] Mn_element001  label="Mn_element : 1"  # scripted group (container) (typed FeaturePython)
  n = 1
  ref = Mn_element
FEATURE [App::DocumentObjectGroupPython] G4_Mn  # scripted group (container) (typed FeaturePython)
  Dunit = g/cm3
  Dvalue = 7.44
  Group = -> [Mn_element001]
  conduct = 2
  density = 1
  expand = 3
  formula = Mn
  name = G4_Mn
  specific = 4
FEATURE [App::DocumentObjectGroupPython] Fe_element007  label="Fe_element : 004"  # scripted group (container) (typed FeaturePython)
  n = 1
  ref = Fe_element
FEATURE [App::DocumentObjectGroupPython] G4_Fe  # scripted group (container) (typed FeaturePython)
  Dunit = g/cm3
  Dvalue = 7.874
  Group = -> [Fe_element007]
  conduct = 2
  density = 1
  expand = 3
  formula = Fe
  name = G4_Fe
  specific = 4
FEATURE [App::DocumentObjectGroupPython] Co_element001  label="Co_element : 1"  # scripted group (container) (typed FeaturePython)
  n = 1
  ref = Co_element
FEATURE [App::DocumentObjectGroupPython] G4_Co  # scripted group (container) (typed FeaturePython)
  Dunit = g/cm3
  Dvalue = 8.9
  Group = -> [Co_element001]
  conduct = 2
  density = 1
  expand = 3
  formula = Co
  name = G4_Co
  specific = 4
FEATURE [App::DocumentObjectGroupPython] Ni_element001  label="Ni_element : 1"  # scripted group (container) (typed FeaturePython)
  n = 1
  ref = Ni_element
FEATURE [App::DocumentObjectGroupPython] G4_Ni  # scripted group (container) (typed FeaturePython)
  Dunit = g/cm3
  Dvalue = 8.902
  Group = -> [Ni_element001]
  conduct = 2
  density = 1
  expand = 3
  formula = Ni
  name = G4_Ni
  specific = 4
FEATURE [App::DocumentObjectGroupPython] Cu_element001  label="Cu_element : 1"  # scripted group (container) (typed FeaturePython)
  n = 1
  ref = Cu_element
FEATURE [App::DocumentObjectGroupPython] G4_Cu  # scripted group (container) (typed FeaturePython)
  Dunit = g/cm3
  Dvalue = 8.96
  Group = -> [Cu_element001]
  conduct = 2
  density = 1
  expand = 3
  formula = Cu
  name = G4_Cu
  specific = 4
FEATURE [App::DocumentObjectGroupPython] Zn_element001  label="Zn_element : 1"  # scripted group (container) (typed FeaturePython)
  n = 1
  ref = Zn_element
FEATURE [App::DocumentObjectGroupPython] G4_Zn  # scripted group (container) (typed FeaturePython)
  Dunit = g/cm3
  Dvalue = 7.133
  Group = -> [Zn_element001]
  conduct = 2
  density = 1
  expand = 3
  formula = Zn
  name = G4_Zn
  specific = 4
FEATURE [App::DocumentObjectGroupPython] Ga_element002  label="Ga_element : 002"  # scripted group (container) (typed FeaturePython)
  n = 1
  ref = Ga_element
FEATURE [App::DocumentObjectGroupPython] G4_Ga  # scripted group (container) (typed FeaturePython)
  Dunit = g/cm3
  Dvalue = 5.904
  Group = -> [Ga_element002]
  conduct = 2
  density = 1
  expand = 3
  formula = Ga
  name = G4_Ga
  specific = 4
FEATURE [App::DocumentObjectGroupPython] Ge_element002  label="Ge_element : 1"  # scripted group (container) (typed FeaturePython)
  n = 1
  ref = Ge_element
FEATURE [App::DocumentObjectGroupPython] G4_Ge  # scripted group (container) (typed FeaturePython)
  Dunit = g/cm3
  Dvalue = 5.323
  Group = -> [Ge_element002]
  conduct = 2
  density = 1
  expand = 3
  formula = Ge
  name = G4_Ge
  specific = 4
FEATURE [App::DocumentObjectGroupPython] As_element003  label="As_element : 002"  # scripted group (container) (typed FeaturePython)
  n = 1
  ref = As_element
FEATURE [App::DocumentObjectGroupPython] G4_As  # scripted group (container) (typed FeaturePython)
  Dunit = g/cm3
  Dvalue = 5.73
  Group = -> [As_element003]
  conduct = 2
  density = 1
  expand = 3
  formula = As
  name = G4_As
  specific = 4
FEATURE [App::DocumentObjectGroupPython] Se_element001  label="Se_element : 1"  # scripted group (container) (typed FeaturePython)
  n = 1
  ref = Se_element
FEATURE [App::DocumentObjectGroupPython] G4_Se  # scripted group (container) (typed FeaturePython)
  Dunit = g/cm3
  Dvalue = 4.5
  Group = -> [Se_element001]
  conduct = 2
  density = 1
  expand = 3
  formula = Se
  name = G4_Se
  specific = 4
FEATURE [App::DocumentObjectGroupPython] Br_element007  label="Br_element : 004"  # scripted group (container) (typed FeaturePython)
  n = 1
  ref = Br_element
FEATURE [App::DocumentObjectGroupPython] G4_Br  # scripted group (container) (typed FeaturePython)
  Dunit = g/cm3
  Dvalue = 0.0070721
  Group = -> [Br_element007]
  conduct = 2
  density = 1
  expand = 3
  formula = Br
  name = G4_Br
  specific = 4
FEATURE [App::DocumentObjectGroupPython] Kr_element001  label="Kr_element : 1"  # scripted group (container) (typed FeaturePython)
  n = 1
  ref = Kr_element
FEATURE [App::DocumentObjectGroupPython] G4_Kr  # scripted group (container) (typed FeaturePython)
  Dunit = g/cm3
  Dvalue = 0.00347832
  Group = -> [Kr_element001]
  conduct = 2
  density = 1
  expand = 3
  formula = Kr
  name = G4_Kr
  specific = 4
FEATURE [App::DocumentObjectGroupPython] Rb_element001  label="Rb_element : 1"  # scripted group (container) (typed FeaturePython)
  n = 1
  ref = Rb_element
FEATURE [App::DocumentObjectGroupPython] G4_Rb  # scripted group (container) (typed FeaturePython)
  Dunit = g/cm3
  Dvalue = 1.532
  Group = -> [Rb_element001]
  conduct = 2
  density = 1
  expand = 3
  formula = Rb
  name = G4_Rb
  specific = 4
FEATURE [App::DocumentObjectGroupPython] Sr_element001  label="Sr_element : 1"  # scripted group (container) (typed FeaturePython)
  n = 1
  ref = Sr_element
FEATURE [App::DocumentObjectGroupPython] G4_Sr  # scripted group (container) (typed FeaturePython)
  Dunit = g/cm3
  Dvalue = 2.54
  Group = -> [Sr_element001]
  conduct = 2
  density = 1
  expand = 3
  formula = Sr
  name = G4_Sr
  specific = 4
FEATURE [App::DocumentObjectGroupPython] Y_element001  label="Y_element : 1"  # scripted group (container) (typed FeaturePython)
  n = 1
  ref = Y_element
FEATURE [App::DocumentObjectGroupPython] G4_Y  # scripted group (container) (typed FeaturePython)
  Dunit = g/cm3
  Dvalue = 4.469
  Group = -> [Y_element001]
  conduct = 2
  density = 1
  expand = 3
  formula = Y
  name = G4_Y
  specific = 4
FEATURE [App::DocumentObjectGroupPython] Zr_element001  label="Zr_element : 1"  # scripted group (container) (typed FeaturePython)
  n = 1
  ref = Zr_element
FEATURE [App::DocumentObjectGroupPython] G4_Zr  # scripted group (container) (typed FeaturePython)
  Dunit = g/cm3
  Dvalue = 6.506
  Group = -> [Zr_element001]
  conduct = 2
  density = 1
  expand = 3
  formula = Zr
  name = G4_Zr
  specific = 4
FEATURE [App::DocumentObjectGroupPython] Nb_element001  label="Nb_element : 1"  # scripted group (container) (typed FeaturePython)
  n = 1
  ref = Nb_element
FEATURE [App::DocumentObjectGroupPython] G4_Nb  # scripted group (container) (typed FeaturePython)
  Dunit = g/cm3
  Dvalue = 8.57
  Group = -> [Nb_element001]
  conduct = 2
  density = 1
  expand = 3
  formula = Nb
  name = G4_Nb
  specific = 4
FEATURE [App::DocumentObjectGroupPython] Mo_element001  label="Mo_element : 1"  # scripted group (container) (typed FeaturePython)
  n = 1
  ref = Mo_element
FEATURE [App::DocumentObjectGroupPython] G4_Mo  # scripted group (container) (typed FeaturePython)
  Dunit = g/cm3
  Dvalue = 10.22
  Group = -> [Mo_element001]
  conduct = 2
  density = 1
  expand = 3
  formula = Mo
  name = G4_Mo
  specific = 4
FEATURE [App::DocumentObjectGroupPython] Tc_element001  label="Tc_element : 1"  # scripted group (container) (typed FeaturePython)
  n = 1
  ref = Tc_element
FEATURE [App::DocumentObjectGroupPython] G4_Tc  # scripted group (container) (typed FeaturePython)
  Dunit = g/cm3
  Dvalue = 11.5
  Group = -> [Tc_element001]
  conduct = 2
  density = 1
  expand = 3
  formula = Tc
  name = G4_Tc
  specific = 4
FEATURE [App::DocumentObjectGroupPython] Ru_element001  label="Ru_element : 1"  # scripted group (container) (typed FeaturePython)
  n = 1
  ref = Ru_element
FEATURE [App::DocumentObjectGroupPython] G4_Ru  # scripted group (container) (typed FeaturePython)
  Dunit = g/cm3
  Dvalue = 12.41
  Group = -> [Ru_element001]
  conduct = 2
  density = 1
  expand = 3
  formula = Ru
  name = G4_Ru
  specific = 4
FEATURE [App::DocumentObjectGroupPython] Rh_element001  label="Rh_element : 1"  # scripted group (container) (typed FeaturePython)
  n = 1
  ref = Rh_element
FEATURE [App::DocumentObjectGroupPython] G4_Rh  # scripted group (container) (typed FeaturePython)
  Dunit = g/cm3
  Dvalue = 12.41
  Group = -> [Rh_element001]
  conduct = 2
  density = 1
  expand = 3
  formula = Rh
  name = G4_Rh
  specific = 4
FEATURE [App::DocumentObjectGroupPython] Pd_element001  label="Pd_element : 1"  # scripted group (container) (typed FeaturePython)
  n = 1
  ref = Pd_element
FEATURE [App::DocumentObjectGroupPython] G4_Pd  # scripted group (container) (typed FeaturePython)
  Dunit = g/cm3
  Dvalue = 12.02
  Group = -> [Pd_element001]
  conduct = 2
  density = 1
  expand = 3
  formula = Pd
  name = G4_Pd
  specific = 4
FEATURE [App::DocumentObjectGroupPython] Ag_element006  label="Ag_element : 004"  # scripted group (container) (typed FeaturePython)
  n = 1
  ref = Ag_element
FEATURE [App::DocumentObjectGroupPython] G4_Ag  # scripted group (container) (typed FeaturePython)
  Dunit = g/cm3
  Dvalue = 10.5
  Group = -> [Ag_element006]
  conduct = 2
  density = 1
  expand = 3
  formula = Ag
  name = G4_Ag
  specific = 4
FEATURE [App::DocumentObjectGroupPython] Cd_element003  label="Cd_element : 003"  # scripted group (container) (typed FeaturePython)
  n = 1
  ref = Cd_element
FEATURE [App::DocumentObjectGroupPython] G4_Cd  # scripted group (container) (typed FeaturePython)
  Dunit = g/cm3
  Dvalue = 8.65
  Group = -> [Cd_element003]
  conduct = 2
  density = 1
  expand = 3
  formula = Cd
  name = G4_Cd
  specific = 4
FEATURE [App::DocumentObjectGroupPython] In_element001  label="In_element : 1"  # scripted group (container) (typed FeaturePython)
  n = 1
  ref = In_element
FEATURE [App::DocumentObjectGroupPython] G4_In  # scripted group (container) (typed FeaturePython)
  Dunit = g/cm3
  Dvalue = 7.31
  Group = -> [In_element001]
  conduct = 2
  density = 1
  expand = 3
  formula = In
  name = G4_In
  specific = 4
FEATURE [App::DocumentObjectGroupPython] Sn_element001  label="Sn_element : 1"  # scripted group (container) (typed FeaturePython)
  n = 1
  ref = Sn_element
FEATURE [App::DocumentObjectGroupPython] G4_Sn  # scripted group (container) (typed FeaturePython)
  Dunit = g/cm3
  Dvalue = 7.31
  Group = -> [Sn_element001]
  conduct = 2
  density = 1
  expand = 3
  formula = Sn
  name = G4_Sn
  specific = 4
FEATURE [App::DocumentObjectGroupPython] Sb_element001  label="Sb_element : 1"  # scripted group (container) (typed FeaturePython)
  n = 1
  ref = Sb_element
FEATURE [App::DocumentObjectGroupPython] G4_Sb  # scripted group (container) (typed FeaturePython)
  Dunit = g/cm3
  Dvalue = 6.691
  Group = -> [Sb_element001]
  conduct = 2
  density = 1
  expand = 3
  formula = Sb
  name = G4_Sb
  specific = 4
FEATURE [App::DocumentObjectGroupPython] Te_element002  label="Te_element : 002"  # scripted group (container) (typed FeaturePython)
  n = 1
  ref = Te_element
FEATURE [App::DocumentObjectGroupPython] G4_Te  # scripted group (container) (typed FeaturePython)
  Dunit = g/cm3
  Dvalue = 6.24
  Group = -> [Te_element002]
  conduct = 2
  density = 1
  expand = 3
  formula = Te
  name = G4_Te
  specific = 4
FEATURE [App::DocumentObjectGroupPython] I_element010  label="I_element : 006"  # scripted group (container) (typed FeaturePython)
  n = 1
  ref = I_element
FEATURE [App::DocumentObjectGroupPython] G4_I  # scripted group (container) (typed FeaturePython)
  Dunit = g/cm3
  Dvalue = 4.93
  Group = -> [I_element010]
  conduct = 2
  density = 1
  expand = 3
  formula = I
  name = G4_I
  specific = 4
FEATURE [App::DocumentObjectGroupPython] Xe_element001  label="Xe_element : 1"  # scripted group (container) (typed FeaturePython)
  n = 1
  ref = Xe_element
FEATURE [App::DocumentObjectGroupPython] G4_Xe  # scripted group (container) (typed FeaturePython)
  Dunit = g/cm3
  Dvalue = 0.00548536
  Group = -> [Xe_element001]
  conduct = 2
  density = 1
  expand = 3
  formula = Xe
  name = G4_Xe
  specific = 4
FEATURE [App::DocumentObjectGroupPython] Cs_element003  label="Cs_element : 003"  # scripted group (container) (typed FeaturePython)
  n = 1
  ref = Cs_element
FEATURE [App::DocumentObjectGroupPython] G4_Cs  # scripted group (container) (typed FeaturePython)
  Dunit = g/cm3
  Dvalue = 1.873
  Group = -> [Cs_element003]
  conduct = 2
  density = 1
  expand = 3
  formula = Cs
  name = G4_Cs
  specific = 4
FEATURE [App::DocumentObjectGroupPython] Ba_element003  label="Ba_element : 003"  # scripted group (container) (typed FeaturePython)
  n = 1
  ref = Ba_element
FEATURE [App::DocumentObjectGroupPython] G4_Ba  # scripted group (container) (typed FeaturePython)
  Dunit = g/cm3
  Dvalue = 3.5
  Group = -> [Ba_element003]
  conduct = 2
  density = 1
  expand = 3
  formula = Ba
  name = G4_Ba
  specific = 4
FEATURE [App::DocumentObjectGroupPython] La_element003  label="La_element : 003"  # scripted group (container) (typed FeaturePython)
  n = 1
  ref = La_element
FEATURE [App::DocumentObjectGroupPython] G4_La  # scripted group (container) (typed FeaturePython)
  Dunit = g/cm3
  Dvalue = 6.154
  Group = -> [La_element003]
  conduct = 2
  density = 1
  expand = 3
  formula = La
  name = G4_La
  specific = 4
FEATURE [App::DocumentObjectGroupPython] Ce_element002  label="Ce_element : 1"  # scripted group (container) (typed FeaturePython)
  n = 1
  ref = Ce_element
FEATURE [App::DocumentObjectGroupPython] G4_Ce  # scripted group (container) (typed FeaturePython)
  Dunit = g/cm3
  Dvalue = 6.657
  Group = -> [Ce_element002]
  conduct = 2
  density = 1
  expand = 3
  formula = Ce
  name = G4_Ce
  specific = 4
FEATURE [App::DocumentObjectGroupPython] Pr_element001  label="Pr_element : 1"  # scripted group (container) (typed FeaturePython)
  n = 1
  ref = Pr_element
FEATURE [App::DocumentObjectGroupPython] G4_Pr  # scripted group (container) (typed FeaturePython)
  Dunit = g/cm3
  Dvalue = 6.71
  Group = -> [Pr_element001]
  conduct = 2
  density = 1
  expand = 3
  formula = Pr
  name = G4_Pr
  specific = 4
FEATURE [App::DocumentObjectGroupPython] Nd_element001  label="Nd_element : 1"  # scripted group (container) (typed FeaturePython)
  n = 1
  ref = Nd_element
FEATURE [App::DocumentObjectGroupPython] G4_Nd  # scripted group (container) (typed FeaturePython)
  Dunit = g/cm3
  Dvalue = 6.9
  Group = -> [Nd_element001]
  conduct = 2
  density = 1
  expand = 3
  formula = Nd
  name = G4_Nd
  specific = 4
FEATURE [App::DocumentObjectGroupPython] Pm_element001  label="Pm_element : 1"  # scripted group (container) (typed FeaturePython)
  n = 1
  ref = Pm_element
FEATURE [App::DocumentObjectGroupPython] G4_Pm  # scripted group (container) (typed FeaturePython)
  Dunit = g/cm3
  Dvalue = 7.22
  Group = -> [Pm_element001]
  conduct = 2
  density = 1
  expand = 3
  formula = Pm
  name = G4_Pm
  specific = 4
FEATURE [App::DocumentObjectGroupPython] Sm_element001  label="Sm_element : 1"  # scripted group (container) (typed FeaturePython)
  n = 1
  ref = Sm_element
FEATURE [App::DocumentObjectGroupPython] G4_Sm  # scripted group (container) (typed FeaturePython)
  Dunit = g/cm3
  Dvalue = 7.46
  Group = -> [Sm_element001]
  conduct = 2
  density = 1
  expand = 3
  formula = Sm
  name = G4_Sm
  specific = 4
FEATURE [App::DocumentObjectGroupPython] Eu_element001  label="Eu_element : 1"  # scripted group (container) (typed FeaturePython)
  n = 1
  ref = Eu_element
FEATURE [App::DocumentObjectGroupPython] G4_Eu  # scripted group (container) (typed FeaturePython)
  Dunit = g/cm3
  Dvalue = 5.243
  Group = -> [Eu_element001]
  conduct = 2
  density = 1
  expand = 3
  formula = Eu
  name = G4_Eu
  specific = 4
FEATURE [App::DocumentObjectGroupPython] Gd_element002  label="Gd_element : 1"  # scripted group (container) (typed FeaturePython)
  n = 1
  ref = Gd_element
FEATURE [App::DocumentObjectGroupPython] G4_Gd  # scripted group (container) (typed FeaturePython)
  Dunit = g/cm3
  Dvalue = 7.9004
  Group = -> [Gd_element002]
  conduct = 2
  density = 1
  expand = 3
  formula = Gd
  name = G4_Gd
  specific = 4
FEATURE [App::DocumentObjectGroupPython] Tb_element001  label="Tb_element : 1"  # scripted group (container) (typed FeaturePython)
  n = 1
  ref = Tb_element
FEATURE [App::DocumentObjectGroupPython] G4_Tb  # scripted group (container) (typed FeaturePython)
  Dunit = g/cm3
  Dvalue = 8.229
  Group = -> [Tb_element001]
  conduct = 2
  density = 1
  expand = 3
  formula = Tb
  name = G4_Tb
  specific = 4
FEATURE [App::DocumentObjectGroupPython] Dy_element001  label="Dy_element : 1"  # scripted group (container) (typed FeaturePython)
  n = 1
  ref = Dy_element
FEATURE [App::DocumentObjectGroupPython] G4_Dy  # scripted group (container) (typed FeaturePython)
  Dunit = g/cm3
  Dvalue = 8.55
  Group = -> [Dy_element001]
  conduct = 2
  density = 1
  expand = 3
  formula = Dy
  name = G4_Dy
  specific = 4
FEATURE [App::DocumentObjectGroupPython] Ho_element001  label="Ho_element : 1"  # scripted group (container) (typed FeaturePython)
  n = 1
  ref = Ho_element
FEATURE [App::DocumentObjectGroupPython] G4_Ho  # scripted group (container) (typed FeaturePython)
  Dunit = g/cm3
  Dvalue = 8.795
  Group = -> [Ho_element001]
  conduct = 2
  density = 1
  expand = 3
  formula = Ho
  name = G4_Ho
  specific = 4
FEATURE [App::DocumentObjectGroupPython] Er_element001  label="Er_element : 1"  # scripted group (container) (typed FeaturePython)
  n = 1
  ref = Er_element
FEATURE [App::DocumentObjectGroupPython] G4_Er  # scripted group (container) (typed FeaturePython)
  Dunit = g/cm3
  Dvalue = 9.066
  Group = -> [Er_element001]
  conduct = 2
  density = 1
  expand = 3
  formula = Er
  name = G4_Er
  specific = 4
FEATURE [App::DocumentObjectGroupPython] Tm_element001  label="Tm_element : 1"  # scripted group (container) (typed FeaturePython)
  n = 1
  ref = Tm_element
FEATURE [App::DocumentObjectGroupPython] G4_Tm  # scripted group (container) (typed FeaturePython)
  Dunit = g/cm3
  Dvalue = 9.321
  Group = -> [Tm_element001]
  conduct = 2
  density = 1
  expand = 3
  formula = Tm
  name = G4_Tm
  specific = 4
FEATURE [App::DocumentObjectGroupPython] Yb_element001  label="Yb_element : 1"  # scripted group (container) (typed FeaturePython)
  n = 1
  ref = Yb_element
FEATURE [App::DocumentObjectGroupPython] G4_Yb  # scripted group (container) (typed FeaturePython)
  Dunit = g/cm3
  Dvalue = 6.73
  Group = -> [Yb_element001]
  conduct = 2
  density = 1
  expand = 3
  formula = Yb
  name = G4_Yb
  specific = 4
FEATURE [App::DocumentObjectGroupPython] Lu_element001  label="Lu_element : 1"  # scripted group (container) (typed FeaturePython)
  n = 1
  ref = Lu_element
FEATURE [App::DocumentObjectGroupPython] G4_Lu  # scripted group (container) (typed FeaturePython)
  Dunit = g/cm3
  Dvalue = 9.84
  Group = -> [Lu_element001]
  conduct = 2
  density = 1
  expand = 3
  formula = Lu
  name = G4_Lu
  specific = 4
FEATURE [App::DocumentObjectGroupPython] Hf_element001  label="Hf_element : 1"  # scripted group (container) (typed FeaturePython)
  n = 1
  ref = Hf_element
FEATURE [App::DocumentObjectGroupPython] G4_Hf  # scripted group (container) (typed FeaturePython)
  Dunit = g/cm3
  Dvalue = 13.31
  Group = -> [Hf_element001]
  conduct = 2
  density = 1
  expand = 3
  formula = Hf
  name = G4_Hf
  specific = 4
FEATURE [App::DocumentObjectGroupPython] Ta_element001  label="Ta_element : 1"  # scripted group (container) (typed FeaturePython)
  n = 1
  ref = Ta_element
FEATURE [App::DocumentObjectGroupPython] G4_Ta  # scripted group (container) (typed FeaturePython)
  Dunit = g/cm3
  Dvalue = 16.654
  Group = -> [Ta_element001]
  conduct = 2
  density = 1
  expand = 3
  formula = Ta
  name = G4_Ta
  specific = 4
FEATURE [App::DocumentObjectGroupPython] W_element004  label="W_element : 004"  # scripted group (container) (typed FeaturePython)
  n = 1
  ref = W_element
FEATURE [App::DocumentObjectGroupPython] G4_W  # scripted group (container) (typed FeaturePython)
  Dunit = g/cm3
  Dvalue = 19.3
  Group = -> [W_element004]
  conduct = 2
  density = 1
  expand = 3
  formula = W
  name = G4_W
  specific = 4
FEATURE [App::DocumentObjectGroupPython] Re_element001  label="Re_element : 1"  # scripted group (container) (typed FeaturePython)
  n = 1
  ref = Re_element
FEATURE [App::DocumentObjectGroupPython] G4_Re  # scripted group (container) (typed FeaturePython)
  Dunit = g/cm3
  Dvalue = 21.02
  Group = -> [Re_element001]
  conduct = 2
  density = 1
  expand = 3
  formula = Re
  name = G4_Re
  specific = 4
FEATURE [App::DocumentObjectGroupPython] Os_element001  label="Os_element : 1"  # scripted group (container) (typed FeaturePython)
  n = 1
  ref = Os_element
FEATURE [App::DocumentObjectGroupPython] G4_Os  # scripted group (container) (typed FeaturePython)
  Dunit = g/cm3
  Dvalue = 22.57
  Group = -> [Os_element001]
  conduct = 2
  density = 1
  expand = 3
  formula = Os
  name = G4_Os
  specific = 4
FEATURE [App::DocumentObjectGroupPython] Ir_element001  label="Ir_element : 1"  # scripted group (container) (typed FeaturePython)
  n = 1
  ref = Ir_element
FEATURE [App::DocumentObjectGroupPython] G4_Ir  # scripted group (container) (typed FeaturePython)
  Dunit = g/cm3
  Dvalue = 22.42
  Group = -> [Ir_element001]
  conduct = 2
  density = 1
  expand = 3
  formula = Ir
  name = G4_Ir
  specific = 4
FEATURE [App::DocumentObjectGroupPython] Pt_element001  label="Pt_element : 1"  # scripted group (container) (typed FeaturePython)
  n = 1
  ref = Pt_element
FEATURE [App::DocumentObjectGroupPython] G4_Pt  # scripted group (container) (typed FeaturePython)
  Dunit = g/cm3
  Dvalue = 21.45
  Group = -> [Pt_element001]
  conduct = 2
  density = 1
  expand = 3
  formula = Pt
  name = G4_Pt
  specific = 4
FEATURE [App::DocumentObjectGroupPython] Au_element001  label="Au_element : 1"  # scripted group (container) (typed FeaturePython)
  n = 1
  ref = Au_element
FEATURE [App::DocumentObjectGroupPython] G4_Au  # scripted group (container) (typed FeaturePython)
  Dunit = g/cm3
  Dvalue = 19.32
  Group = -> [Au_element001]
  conduct = 2
  density = 1
  expand = 3
  formula = Au
  name = G4_Au
  specific = 4
FEATURE [App::DocumentObjectGroupPython] Hg_element002  label="Hg_element : 002"  # scripted group (container) (typed FeaturePython)
  n = 1
  ref = Hg_element
FEATURE [App::DocumentObjectGroupPython] G4_Hg  # scripted group (container) (typed FeaturePython)
  Dunit = g/cm3
  Dvalue = 13.546
  Group = -> [Hg_element002]
  conduct = 2
  density = 1
  expand = 3
  formula = Hg
  name = G4_Hg
  specific = 4
FEATURE [App::DocumentObjectGroupPython] Tl_element002  label="Tl_element : 002"  # scripted group (container) (typed FeaturePython)
  n = 1
  ref = Tl_element
FEATURE [App::DocumentObjectGroupPython] G4_Tl  # scripted group (container) (typed FeaturePython)
  Dunit = g/cm3
  Dvalue = 11.72
  Group = -> [Tl_element002]
  conduct = 2
  density = 1
  expand = 3
  formula = Tl
  name = G4_Tl
  specific = 4
FEATURE [App::DocumentObjectGroupPython] Pb_element003  label="Pb_element : 1"  # scripted group (container) (typed FeaturePython)
  n = 1
  ref = Pb_element
FEATURE [App::DocumentObjectGroupPython] G4_Pb  # scripted group (container) (typed FeaturePython)
  Dunit = g/cm3
  Dvalue = 11.35
  Group = -> [Pb_element003]
  conduct = 2
  density = 1
  expand = 3
  formula = Pb
  name = G4_Pb
  specific = 4
FEATURE [App::DocumentObjectGroupPython] Bi_element002  label="Bi_element : 1"  # scripted group (container) (typed FeaturePython)
  n = 1
  ref = Bi_element
FEATURE [App::DocumentObjectGroupPython] G4_Bi  # scripted group (container) (typed FeaturePython)
  Dunit = g/cm3
  Dvalue = 9.747
  Group = -> [Bi_element002]
  conduct = 2
  density = 1
  expand = 3
  formula = Bi
  name = G4_Bi
  specific = 4
FEATURE [App::DocumentObjectGroupPython] Po_element001  label="Po_element : 1"  # scripted group (container) (typed FeaturePython)
  n = 1
  ref = Po_element
FEATURE [App::DocumentObjectGroupPython] G4_Po  # scripted group (container) (typed FeaturePython)
  Dunit = g/cm3
  Dvalue = 9.32
  Group = -> [Po_element001]
  conduct = 2
  density = 1
  expand = 3
  formula = Po
  name = G4_Po
  specific = 4
FEATURE [App::DocumentObjectGroupPython] At_element001  label="At_element : 1"  # scripted group (container) (typed FeaturePython)
  n = 1
  ref = At_element
FEATURE [App::DocumentObjectGroupPython] G4_At  # scripted group (container) (typed FeaturePython)
  Dunit = g/cm3
  Dvalue = 9.32
  Group = -> [At_element001]
  conduct = 2
  density = 1
  expand = 3
  formula = At
  name = G4_At
  specific = 4
FEATURE [App::DocumentObjectGroupPython] Rn_element001  label="Rn_element : 1"  # scripted group (container) (typed FeaturePython)
  n = 1
  ref = Rn_element
FEATURE [App::DocumentObjectGroupPython] G4_Rn  # scripted group (container) (typed FeaturePython)
  Dunit = g/cm3
  Dvalue = 0.00900662
  Group = -> [Rn_element001]
  conduct = 2
  density = 1
  expand = 3
  formula = Rn
  name = G4_Rn
  specific = 4
FEATURE [App::DocumentObjectGroupPython] Fr_element001  label="Fr_element : 1"  # scripted group (container) (typed FeaturePython)
  n = 1
  ref = Fr_element
FEATURE [App::DocumentObjectGroupPython] G4_Fr  # scripted group (container) (typed FeaturePython)
  Dunit = g/cm3
  Dvalue = 1
  Group = -> [Fr_element001]
  conduct = 2
  density = 1
  expand = 3
  formula = Fr
  name = G4_Fr
  specific = 4
FEATURE [App::DocumentObjectGroupPython] Ra_element001  label="Ra_element : 1"  # scripted group (container) (typed FeaturePython)
  n = 1
  ref = Ra_element
FEATURE [App::DocumentObjectGroupPython] G4_Ra  # scripted group (container) (typed FeaturePython)
  Dunit = g/cm3
  Dvalue = 5
  Group = -> [Ra_element001]
  conduct = 2
  density = 1
  expand = 3
  formula = Ra
  name = G4_Ra
  specific = 4
FEATURE [App::DocumentObjectGroupPython] Ac_element001  label="Ac_element : 1"  # scripted group (container) (typed FeaturePython)
  n = 1
  ref = Ac_element
FEATURE [App::DocumentObjectGroupPython] G4_Ac  # scripted group (container) (typed FeaturePython)
  Dunit = g/cm3
  Dvalue = 10.07
  Group = -> [Ac_element001]
  conduct = 2
  density = 1
  expand = 3
  formula = Ac
  name = G4_Ac
  specific = 4
FEATURE [App::DocumentObjectGroupPython] Th_element001  label="Th_element : 1"  # scripted group (container) (typed FeaturePython)
  n = 1
  ref = Th_element
FEATURE [App::DocumentObjectGroupPython] G4_Th  # scripted group (container) (typed FeaturePython)
  Dunit = g/cm3
  Dvalue = 11.72
  Group = -> [Th_element001]
  conduct = 2
  density = 1
  expand = 3
  formula = Th
  name = G4_Th
  specific = 4
FEATURE [App::DocumentObjectGroupPython] Pa_element001  label="Pa_element : 1"  # scripted group (container) (typed FeaturePython)
  n = 1
  ref = Pa_element
FEATURE [App::DocumentObjectGroupPython] G4_Pa  # scripted group (container) (typed FeaturePython)
  Dunit = g/cm3
  Dvalue = 15.37
  Group = -> [Pa_element001]
  conduct = 2
  density = 1
  expand = 3
  formula = Pa
  name = G4_Pa
  specific = 4
FEATURE [App::DocumentObjectGroupPython] U_element004  label="U_element : 004"  # scripted group (container) (typed FeaturePython)
  n = 1
  ref = U_element
FEATURE [App::DocumentObjectGroupPython] G4_U  # scripted group (container) (typed FeaturePython)
  Dunit = g/cm3
  Dvalue = 18.95
  Group = -> [U_element004]
  conduct = 2
  density = 1
  expand = 3
  formula = U
  name = G4_U
  specific = 4
FEATURE [App::DocumentObjectGroupPython] Np_element001  label="Np_element : 1"  # scripted group (container) (typed FeaturePython)
  n = 1
  ref = Np_element
FEATURE [App::DocumentObjectGroupPython] G4_Np  # scripted group (container) (typed FeaturePython)
  Dunit = g/cm3
  Dvalue = 20.25
  Group = -> [Np_element001]
  conduct = 2
  density = 1
  expand = 3
  formula = Np
  name = G4_Np
  specific = 4
FEATURE [App::DocumentObjectGroupPython] Pu_element002  label="Pu_element : 002"  # scripted group (container) (typed FeaturePython)
  n = 1
  ref = Pu_element
FEATURE [App::DocumentObjectGroupPython] G4_Pu  # scripted group (container) (typed FeaturePython)
  Dunit = g/cm3
  Dvalue = 19.84
  Group = -> [Pu_element002]
  conduct = 2
  density = 1
  expand = 3
  formula = Pu
  name = G4_Pu
  specific = 4
FEATURE [App::DocumentObjectGroupPython] Am_element001  label="Am_element : 1"  # scripted group (container) (typed FeaturePython)
  n = 1
  ref = Am_element
FEATURE [App::DocumentObjectGroupPython] G4_Am  # scripted group (container) (typed FeaturePython)
  Dunit = g/cm3
  Dvalue = 13.67
  Group = -> [Am_element001]
  conduct = 2
  density = 1
  expand = 3
  formula = Am
  name = G4_Am
  specific = 4
FEATURE [App::DocumentObjectGroupPython] Cm_element001  label="Cm_element : 1"  # scripted group (container) (typed FeaturePython)
  n = 1
  ref = Cm_element
FEATURE [App::DocumentObjectGroupPython] G4_Cm  # scripted group (container) (typed FeaturePython)
  Dunit = g/cm3
  Dvalue = 13.51
  Group = -> [Cm_element001]
  conduct = 2
  density = 1
  expand = 3
  formula = Cm
  name = G4_Cm
  specific = 4
FEATURE [App::DocumentObjectGroupPython] Bk_element001  label="Bk_element : 1"  # scripted group (container) (typed FeaturePython)
  n = 1
  ref = Bk_element
FEATURE [App::DocumentObjectGroupPython] G4_Bk  # scripted group (container) (typed FeaturePython)
  Dunit = g/cm3
  Dvalue = 14
  Group = -> [Bk_element001]
  conduct = 2
  density = 1
  expand = 3
  formula = Bk
  name = G4_Bk
  specific = 4
FEATURE [App::DocumentObjectGroupPython] Cf_element001  label="Cf_element : 1"  # scripted group (container) (typed FeaturePython)
  n = 1
  ref = Cf_element
FEATURE [App::DocumentObjectGroupPython] G4_Cf  # scripted group (container) (typed FeaturePython)
  Dunit = g/cm3
  Dvalue = 10
  Group = -> [Cf_element001]
  conduct = 2
  density = 1
  expand = 3
  formula = Cf
  name = G4_Cf
  specific = 4
FEATURE [App::DocumentObjectGroupPython] Element  # scripted group (container) (typed FeaturePython)
  Group = -> [G4_H,G4_He,G4_Li,G4_Be,G4_B,G4_C,G4_N,G4_O,G4_F,G4_Ne,G4_Na,G4_Mg,G4_Al,G4_Si,G4_P,G4_S,G4_Cl,G4_Ar,G4_K,G4_Ca,G4_Sc,G4_Ti,G4_V,G4_Cr,G4_Mn,G4_Fe,G4_Co,G4_Ni,G4_Cu,G4_Zn,G4_Ga,G4_Ge,G4_As,G4_Se,G4_Br,G4_Kr,G4_Rb,G4_Sr,G4_Y,G4_Zr,G4_Nb,G4_Mo,G4_Tc,G4_Ru,G4_Rh,G4_Pd,G4_Ag,G4_Cd,G4_In,G4_Sn,G4_Sb,G4_Te,G4_I,G4_Xe,G4_Cs,G4_Ba,G4_La,G4_Ce,G4_Pr,G4_Nd,G4_Pm,G4_Sm,G4_Eu,G4_Gd,G4_Tb,G4_Dy,G4_Ho,G4_Er,+30 more]
FEATURE [App::DocumentObjectGroupPython] H_element114  label="H_element : 063"  # scripted group (container) (typed FeaturePython)
  n = 2
  ref = H_element
FEATURE [App::DocumentObjectGroupPython] G4_lH2  # scripted group (container) (typed FeaturePython)
  Dunit = g/cm3
  Dvalue = 0.0708
  Group = -> [H_element114]
  conduct = 2
  density = 1
  expand = 3
  formula = G4_lH2
  name = G4_lH2
  specific = 4
FEATURE [App::DocumentObjectGroupPython] N_element049  label="N_element : 022"  # scripted group (container) (typed FeaturePython)
  n = 2
  ref = N_element
FEATURE [App::DocumentObjectGroupPython] G4_lN2  # scripted group (container) (typed FeaturePython)
  Dunit = g/cm3
  Dvalue = 0.807
  Group = -> [N_element049]
  conduct = 2
  density = 1
  expand = 3
  formula = G4_lN2
  name = G4_lN2
  specific = 4
FEATURE [App::DocumentObjectGroupPython] O_element106  label="O_element : 060"  # scripted group (container) (typed FeaturePython)
  n = 2
  ref = O_element
FEATURE [App::DocumentObjectGroupPython] G4_lO2  # scripted group (container) (typed FeaturePython)
  Dunit = g/cm3
  Dvalue = 1.141
  Group = -> [O_element106]
  conduct = 2
  density = 1
  expand = 3
  formula = G4_lO2
  name = G4_lO2
  specific = 4
FEATURE [App::DocumentObjectGroupPython] Ar  label="Ar : 1"  # scripted group (container) (typed FeaturePython)
  n = 1
  ref = Ar
FEATURE [App::DocumentObjectGroupPython] G4_lAr  # scripted group (container) (typed FeaturePython)
  Dunit = g/cm3
  Dvalue = 1.396
  Group = -> [Ar]
  conduct = 2
  density = 1
  expand = 3
  formula = G4_lAr
  name = G4_lAr
  specific = 4
FEATURE [App::DocumentObjectGroupPython] Br  label="Br : 1"  # scripted group (container) (typed FeaturePython)
  n = 1
  ref = Br
FEATURE [App::DocumentObjectGroupPython] G4_lBr  # scripted group (container) (typed FeaturePython)
  Dunit = g/cm3
  Dvalue = 3.1028
  Group = -> [Br]
  conduct = 2
  density = 1
  expand = 3
  formula = G4_lBr
  name = G4_lBr
  specific = 4
FEATURE [App::DocumentObjectGroupPython] Kr  label="Kr : 1"  # scripted group (container) (typed FeaturePython)
  n = 1
  ref = Kr
FEATURE [App::DocumentObjectGroupPython] G4_lKr  # scripted group (container) (typed FeaturePython)
  Dunit = g/cm3
  Dvalue = 2.418
  Group = -> [Kr]
  conduct = 2
  density = 1
  expand = 3
  formula = G4_lKr
  name = G4_lKr
  specific = 4
FEATURE [App::DocumentObjectGroupPython] Xe  label="Xe : 1"  # scripted group (container) (typed FeaturePython)
  n = 1
  ref = Xe
FEATURE [App::DocumentObjectGroupPython] G4_lXe  # scripted group (container) (typed FeaturePython)
  Dunit = g/cm3
  Dvalue = 2.953
  Group = -> [Xe]
  conduct = 2
  density = 1
  expand = 3
  formula = G4_lXe
  name = G4_lXe
  specific = 4
FEATURE [App::DocumentObjectGroupPython] O_element107  label="O_element : 061"  # scripted group (container) (typed FeaturePython)
  n = 4
  ref = O_element
FEATURE [App::DocumentObjectGroupPython] Pb_element004  label="Pb_element : 002"  # scripted group (container) (typed FeaturePython)
  n = 1
  ref = Pb_element
FEATURE [App::DocumentObjectGroupPython] W_element005  label="W_element : 005"  # scripted group (container) (typed FeaturePython)
  n = 1
  ref = W_element
FEATURE [App::DocumentObjectGroupPython] G4_PbWO4  # scripted group (container) (typed FeaturePython)
  Dunit = g/cm3
  Dvalue = 8.28
  Group = -> [O_element107,Pb_element004,W_element005]
  conduct = 2
  density = 1
  expand = 3
  formula = G4_PbWO4
  name = G4_PbWO4
  specific = 4
FEATURE [App::DocumentObjectGroupPython] alactic  label="alactic : 1"  # scripted group (container) (typed FeaturePython)
  n = 1
  ref = alactic
FEATURE [App::DocumentObjectGroupPython] G4_Galactic  # scripted group (container) (typed FeaturePython)
  Dunit = g/cm3
  Dvalue = 0
  Group = -> [alactic]
  conduct = 2
  density = 1
  expand = 3
  formula = G4_Galactic
  name = G4_Galactic
  specific = 4
FEATURE [App::DocumentObjectGroupPython] RAPHITE_POROUS  label="RAPHITE_POROUS : 1"  # scripted group (container) (typed FeaturePython)
  n = 1
  ref = RAPHITE_POROUS
FEATURE [App::DocumentObjectGroupPython] G4_GRAPHITE_POROUS  # scripted group (container) (typed FeaturePython)
  Dunit = g/cm3
  Dvalue = 1.7
  Group = -> [RAPHITE_POROUS]
  conduct = 2
  density = 1
  expand = 3
  formula = G4_GRAPHITE_POROUS
  name = G4_GRAPHITE_POROUS
  specific = 4
FEATURE [App::DocumentObjectGroupPython] H_element115  label="H_element : 0.150"  # scripted group (container) (typed FeaturePython)
  n = 0.080538
FEATURE [App::DocumentObjectGroupPython] C_element125  label="C_element : 0.600"  # scripted group (container) (typed FeaturePython)
  n = 0.599848
FEATURE [App::DocumentObjectGroupPython] O_element108  label="O_element : 0.320"  # scripted group (container) (typed FeaturePython)
  n = 0.319614
FEATURE [App::DocumentObjectGroupPython] G4_LUCITE  # scripted group (container) (typed FeaturePython)
  Dunit = g/cm3
  Dvalue = 1.19
  Group = -> [H_element115,C_element125,O_element108]
  conduct = 2
  density = 1
  expand = 3
  formula = G4_LUCITE
  name = G4_LUCITE
  specific = 4
FEATURE [App::DocumentObjectGroupPython] Cu_element002  label="Cu_element : 62"  # scripted group (container) (typed FeaturePython)
  n = 62
  ref = Cu_element
FEATURE [App::DocumentObjectGroupPython] Zn_element002  label="Zn_element : 35"  # scripted group (container) (typed FeaturePython)
  n = 35
  ref = Zn_element
FEATURE [App::DocumentObjectGroupPython] Pb_element005  label="Pb_element : 3"  # scripted group (container) (typed FeaturePython)
  n = 3
  ref = Pb_element
FEATURE [App::DocumentObjectGroupPython] G4_BRASS  # scripted group (container) (typed FeaturePython)
  Dunit = g/cm3
  Dvalue = 8.52
  Group = -> [Cu_element002,Zn_element002,Pb_element005]
  conduct = 2
  density = 1
  expand = 3
  formula = G4_BRASS
  name = G4_BRASS
  specific = 4
FEATURE [App::DocumentObjectGroupPython] Cu_element003  label="Cu_element : 89"  # scripted group (container) (typed FeaturePython)
  n = 89
  ref = Cu_element
FEATURE [App::DocumentObjectGroupPython] Zn_element003  label="Zn_element : 9"  # scripted group (container) (typed FeaturePython)
  n = 9
  ref = Zn_element
FEATURE [App::DocumentObjectGroupPython] Pb_element006  label="Pb_element : 2"  # scripted group (container) (typed FeaturePython)
  n = 2
  ref = Pb_element
FEATURE [App::DocumentObjectGroupPython] G4_BRONZE  # scripted group (container) (typed FeaturePython)
  Dunit = g/cm3
  Dvalue = 8.82
  Group = -> [Cu_element003,Zn_element003,Pb_element006]
  conduct = 2
  density = 1
  expand = 3
  formula = G4_BRONZE
  name = G4_BRONZE
  specific = 4
FEATURE [App::DocumentObjectGroupPython] Fe_element008  label="Fe_element : 74"  # scripted group (container) (typed FeaturePython)
  n = 74
  ref = Fe_element
FEATURE [App::DocumentObjectGroupPython] Cr_element002  label="Cr_element : 18"  # scripted group (container) (typed FeaturePython)
  n = 18
  ref = Cr_element
FEATURE [App::DocumentObjectGroupPython] Ni_element002  label="Ni_element : 8"  # scripted group (container) (typed FeaturePython)
  n = 8
  ref = Ni_element
FEATURE [App::DocumentObjectGroupPython] G4_STAINLESS_STEEL  label="G4_STAINLESS-STEEL"  # scripted group (container) (typed FeaturePython)
  Dunit = g/cm3
  Dvalue = 8
  Group = -> [Fe_element008,Cr_element002,Ni_element002]
  conduct = 2
  density = 1
  expand = 3
  formula = G4_STAINLESS-STEEL
  name = G4_STAINLESS-STEEL
  specific = 4
FEATURE [App::DocumentObjectGroupPython] H_element116  label="H_element : 064"  # scripted group (container) (typed FeaturePython)
  n = 18
  ref = H_element
FEATURE [App::DocumentObjectGroupPython] C_element126  label="C_element : 071"  # scripted group (container) (typed FeaturePython)
  n = 12
  ref = C_element
FEATURE [App::DocumentObjectGroupPython] O_element109  label="O_element : 062"  # scripted group (container) (typed FeaturePython)
  n = 7
  ref = O_element
FEATURE [App::DocumentObjectGroupPython] G4_CR39  # scripted group (container) (typed FeaturePython)
  Dunit = g/cm3
  Dvalue = 1.32
  Group = -> [H_element116,C_element126,O_element109]
  conduct = 2
  density = 1
  expand = 3
  formula = G4_CR39
  name = G4_CR39
  specific = 4
FEATURE [App::DocumentObjectGroupPython] H_element117  label="H_element : 38"  # scripted group (container) (typed FeaturePython)
  n = 38
  ref = H_element
FEATURE [App::DocumentObjectGroupPython] C_element127  label="C_element : 072"  # scripted group (container) (typed FeaturePython)
  n = 18
  ref = C_element
FEATURE [App::DocumentObjectGroupPython] O_element110  label="O_element : 063"  # scripted group (container) (typed FeaturePython)
  n = 1
  ref = O_element
FEATURE [App::DocumentObjectGroupPython] G4_OCTADECANOL  # scripted group (container) (typed FeaturePython)
  Dunit = g/cm3
  Dvalue = 0.812
  Group = -> [H_element117,C_element127,O_element110]
  conduct = 2
  density = 1
  expand = 3
  formula = G4_OCTADECANOL
  name = G4_OCTADECANOL
  specific = 4
FEATURE [App::DocumentObjectGroupPython] HEP  # scripted group (container) (typed FeaturePython)
  Group = -> [G4_lH2,G4_lN2,G4_lO2,G4_lAr,G4_lBr,G4_lKr,G4_lXe,G4_PbWO4,G4_Galactic,G4_GRAPHITE_POROUS,G4_LUCITE,G4_BRASS,G4_BRONZE,G4_STAINLESS_STEEL,G4_CR39,G4_OCTADECANOL]
FEATURE [App::DocumentObjectGroupPython] C_element128  label="C_element : 073"  # scripted group (container) (typed FeaturePython)
  n = 14
  ref = C_element
FEATURE [App::DocumentObjectGroupPython] H_element118  label="H_element : 065"  # scripted group (container) (typed FeaturePython)
  n = 10
  ref = H_element
FEATURE [App::DocumentObjectGroupPython] O_element111  label="O_element : 064"  # scripted group (container) (typed FeaturePython)
  n = 2
  ref = O_element
FEATURE [App::DocumentObjectGroupPython] N_element050  label="N_element : 023"  # scripted group (container) (typed FeaturePython)
  n = 2
  ref = N_element
FEATURE [App::DocumentObjectGroupPython] G4_KEVLAR  # scripted group (container) (typed FeaturePython)
  Dunit = g/cm3
  Dvalue = 1.44
  Group = -> [C_element128,H_element118,O_element111,N_element050]
  conduct = 2
  density = 1
  expand = 3
  formula = G4_KEVLAR
  name = G4_KEVLAR
  specific = 4
FEATURE [App::DocumentObjectGroupPython] C_element129  label="C_element : 074"  # scripted group (container) (typed FeaturePython)
  n = 10
  ref = C_element
FEATURE [App::DocumentObjectGroupPython] H_element119  label="H_element : 066"  # scripted group (container) (typed FeaturePython)
  n = 8
  ref = H_element
FEATURE [App::DocumentObjectGroupPython] O_element112  label="O_element : 065"  # scripted group (container) (typed FeaturePython)
  n = 4
  ref = O_element
FEATURE [App::DocumentObjectGroupPython] G4_DACRON  # scripted group (container) (typed FeaturePython)
  Dunit = g/cm3
  Dvalue = 1.4
  Group = -> [C_element129,H_element119,O_element112]
  conduct = 2
  density = 1
  expand = 3
  formula = G4_DACRON
  name = G4_DACRON
  specific = 4
FEATURE [App::DocumentObjectGroupPython] C_element130  label="C_element : 075"  # scripted group (container) (typed FeaturePython)
  n = 4
  ref = C_element
FEATURE [App::DocumentObjectGroupPython] H_element120  label="H_element : 067"  # scripted group (container) (typed FeaturePython)
  n = 5
  ref = H_element
FEATURE [App::DocumentObjectGroupPython] Cl_element030  label="Cl_element : 016"  # scripted group (container) (typed FeaturePython)
  n = 1
  ref = Cl_element
FEATURE [App::DocumentObjectGroupPython] G4_NEOPRENE  # scripted group (container) (typed FeaturePython)
  Dunit = g/cm3
  Dvalue = 1.23
  Group = -> [C_element130,H_element120,Cl_element030]
  conduct = 2
  density = 1
  expand = 3
  formula = G4_NEOPRENE
  name = G4_NEOPRENE
  specific = 4
FEATURE [App::DocumentObjectGroupPython] Space  # scripted group (container) (typed FeaturePython)
  Group = -> [G4_KEVLAR,G4_DACRON,G4_NEOPRENE]
FEATURE [App::DocumentObjectGroupPython] H_element121  label="H_element : 068"  # scripted group (container) (typed FeaturePython)
  n = 5
  ref = H_element
FEATURE [App::DocumentObjectGroupPython] C_element131  label="C_element : 076"  # scripted group (container) (typed FeaturePython)
  n = 4
  ref = C_element
FEATURE [App::DocumentObjectGroupPython] N_element051  label="N_element : 3"  # scripted group (container) (typed FeaturePython)
  n = 3
  ref = N_element
FEATURE [App::DocumentObjectGroupPython] O_element113  label="O_element : 066"  # scripted group (container) (typed FeaturePython)
  n = 1
  ref = O_element
FEATURE [App::DocumentObjectGroupPython] G4_CYTOSINE  # scripted group (container) (typed FeaturePython)
  Dunit = g/cm3
  Dvalue = 1.55
  Group = -> [H_element121,C_element131,N_element051,O_element113]
  conduct = 2
  density = 1
  expand = 3
  formula = G4_CYTOSINE
  name = G4_CYTOSINE
  specific = 4
FEATURE [App::DocumentObjectGroupPython] H_element122  label="H_element : 069"  # scripted group (container) (typed FeaturePython)
  n = 6
  ref = H_element
FEATURE [App::DocumentObjectGroupPython] C_element132  label="C_element : 077"  # scripted group (container) (typed FeaturePython)
  n = 5
  ref = C_element
FEATURE [App::DocumentObjectGroupPython] N_element052  label="N_element : 024"  # scripted group (container) (typed FeaturePython)
  n = 2
  ref = N_element
FEATURE [App::DocumentObjectGroupPython] O_element114  label="O_element : 067"  # scripted group (container) (typed FeaturePython)
  n = 2
  ref = O_element
FEATURE [App::DocumentObjectGroupPython] G4_THYMINE  # scripted group (container) (typed FeaturePython)
  Dunit = g/cm3
  Dvalue = 1.23
  Group = -> [H_element122,C_element132,N_element052,O_element114]
  conduct = 2
  density = 1
  expand = 3
  formula = G4_THYMINE
  name = G4_THYMINE
  specific = 4
FEATURE [App::DocumentObjectGroupPython] H_element123  label="H_element : 070"  # scripted group (container) (typed FeaturePython)
  n = 4
  ref = H_element
FEATURE [App::DocumentObjectGroupPython] C_element133  label="C_element : 078"  # scripted group (container) (typed FeaturePython)
  n = 4
  ref = C_element
FEATURE [App::DocumentObjectGroupPython] N_element053  label="N_element : 025"  # scripted group (container) (typed FeaturePython)
  n = 2
  ref = N_element
FEATURE [App::DocumentObjectGroupPython] O_element115  label="O_element : 068"  # scripted group (container) (typed FeaturePython)
  n = 2
  ref = O_element
FEATURE [App::DocumentObjectGroupPython] G4_URACIL  # scripted group (container) (typed FeaturePython)
  Dunit = g/cm3
  Dvalue = 1.32
  Group = -> [H_element123,C_element133,N_element053,O_element115]
  conduct = 2
  density = 1
  expand = 3
  formula = G4_URACIL
  name = G4_URACIL
  specific = 4
FEATURE [App::DocumentObjectGroupPython] H_element124  label="H_element : 071"  # scripted group (container) (typed FeaturePython)
  n = 4
  ref = H_element
FEATURE [App::DocumentObjectGroupPython] C_element134  label="C_element : 079"  # scripted group (container) (typed FeaturePython)
  n = 5
  ref = C_element
FEATURE [App::DocumentObjectGroupPython] N_element054  label="N_element : 026"  # scripted group (container) (typed FeaturePython)
  n = 5
  ref = N_element
FEATURE [App::DocumentObjectGroupPython] G4_DNA_ADENINE  # scripted group (container) (typed FeaturePython)
  Dunit = g/cm3
  Dvalue = 1
  Group = -> [H_element124,C_element134,N_element054]
  conduct = 2
  density = 1
  expand = 3
  formula = G4_DNA_ADENINE
  name = G4_DNA_ADENINE
  specific = 4
FEATURE [App::DocumentObjectGroupPython] H_element125  label="H_element : 072"  # scripted group (container) (typed FeaturePython)
  n = 4
  ref = H_element
FEATURE [App::DocumentObjectGroupPython] C_element135  label="C_element : 080"  # scripted group (container) (typed FeaturePython)
  n = 5
  ref = C_element
FEATURE [App::DocumentObjectGroupPython] N_element055  label="N_element : 027"  # scripted group (container) (typed FeaturePython)
  n = 5
  ref = N_element
FEATURE [App::DocumentObjectGroupPython] O_element116  label="O_element : 069"  # scripted group (container) (typed FeaturePython)
  n = 1
  ref = O_element
FEATURE [App::DocumentObjectGroupPython] G4_DNA_GUANINE  # scripted group (container) (typed FeaturePython)
  Dunit = g/cm3
  Dvalue = 1
  Group = -> [H_element125,C_element135,N_element055,O_element116]
  conduct = 2
  density = 1
  expand = 3
  formula = G4_DNA_GUANINE
  name = G4_DNA_GUANINE
  specific = 4
FEATURE [App::DocumentObjectGroupPython] H_element126  label="H_element : 073"  # scripted group (container) (typed FeaturePython)
  n = 4
  ref = H_element
FEATURE [App::DocumentObjectGroupPython] C_element136  label="C_element : 081"  # scripted group (container) (typed FeaturePython)
  n = 4
  ref = C_element
FEATURE [App::DocumentObjectGroupPython] N_element056  label="N_element : 028"  # scripted group (container) (typed FeaturePython)
  n = 3
  ref = N_element
FEATURE [App::DocumentObjectGroupPython] O_element117  label="O_element : 070"  # scripted group (container) (typed FeaturePython)
  n = 1
  ref = O_element
FEATURE [App::DocumentObjectGroupPython] G4_DNA_CYTOSINE  # scripted group (container) (typed FeaturePython)
  Dunit = g/cm3
  Dvalue = 1
  Group = -> [H_element126,C_element136,N_element056,O_element117]
  conduct = 2
  density = 1
  expand = 3
  formula = G4_DNA_CYTOSINE
  name = G4_DNA_CYTOSINE
  specific = 4
FEATURE [App::DocumentObjectGroupPython] H_element127  label="H_element : 074"  # scripted group (container) (typed FeaturePython)
  n = 5
  ref = H_element
FEATURE [App::DocumentObjectGroupPython] C_element137  label="C_element : 082"  # scripted group (container) (typed FeaturePython)
  n = 5
  ref = C_element
FEATURE [App::DocumentObjectGroupPython] N_element057  label="N_element : 029"  # scripted group (container) (typed FeaturePython)
  n = 2
  ref = N_element
FEATURE [App::DocumentObjectGroupPython] O_element118  label="O_element : 071"  # scripted group (container) (typed FeaturePython)
  n = 2
  ref = O_element
FEATURE [App::DocumentObjectGroupPython] G4_DNA_THYMINE  # scripted group (container) (typed FeaturePython)
  Dunit = g/cm3
  Dvalue = 1
  Group = -> [H_element127,C_element137,N_element057,O_element118]
  conduct = 2
  density = 1
  expand = 3
  formula = G4_DNA_THYMINE
  name = G4_DNA_THYMINE
  specific = 4
FEATURE [App::DocumentObjectGroupPython] H_element128  label="H_element : 075"  # scripted group (container) (typed FeaturePython)
  n = 3
  ref = H_element
FEATURE [App::DocumentObjectGroupPython] C_element138  label="C_element : 083"  # scripted group (container) (typed FeaturePython)
  n = 4
  ref = C_element
FEATURE [App::DocumentObjectGroupPython] N_element058  label="N_element : 030"  # scripted group (container) (typed FeaturePython)
  n = 2
  ref = N_element
FEATURE [App::DocumentObjectGroupPython] O_element119  label="O_element : 072"  # scripted group (container) (typed FeaturePython)
  n = 2
  ref = O_element
FEATURE [App::DocumentObjectGroupPython] G4_DNA_URACIL  # scripted group (container) (typed FeaturePython)
  Dunit = g/cm3
  Dvalue = 1
  Group = -> [H_element128,C_element138,N_element058,O_element119]
  conduct = 2
  density = 1
  expand = 3
  formula = G4_DNA_URACIL
  name = G4_DNA_URACIL
  specific = 4
FEATURE [App::DocumentObjectGroupPython] H_element129  label="H_element : 076"  # scripted group (container) (typed FeaturePython)
  n = 10
  ref = H_element
FEATURE [App::DocumentObjectGroupPython] C_element139  label="C_element : 084"  # scripted group (container) (typed FeaturePython)
  n = 10
  ref = C_element
FEATURE [App::DocumentObjectGroupPython] N_element059  label="N_element : 031"  # scripted group (container) (typed FeaturePython)
  n = 5
  ref = N_element
FEATURE [App::DocumentObjectGroupPython] O_element120  label="O_element : 073"  # scripted group (container) (typed FeaturePython)
  n = 4
  ref = O_element
FEATURE [App::DocumentObjectGroupPython] G4_DNA_ADENOSINE  # scripted group (container) (typed FeaturePython)
  Dunit = g/cm3
  Dvalue = 1
  Group = -> [H_element129,C_element139,N_element059,O_element120]
  conduct = 2
  density = 1
  expand = 3
  formula = G4_DNA_ADENOSINE
  name = G4_DNA_ADENOSINE
  specific = 4
FEATURE [App::DocumentObjectGroupPython] H_element130  label="H_element : 077"  # scripted group (container) (typed FeaturePython)
  n = 10
  ref = H_element
FEATURE [App::DocumentObjectGroupPython] C_element140  label="C_element : 085"  # scripted group (container) (typed FeaturePython)
  n = 10
  ref = C_element
FEATURE [App::DocumentObjectGroupPython] N_element060  label="N_element : 032"  # scripted group (container) (typed FeaturePython)
  n = 5
  ref = N_element
FEATURE [App::DocumentObjectGroupPython] O_element121  label="O_element : 074"  # scripted group (container) (typed FeaturePython)
  n = 5
  ref = O_element
FEATURE [App::DocumentObjectGroupPython] G4_DNA_GUANOSINE  # scripted group (container) (typed FeaturePython)
  Dunit = g/cm3
  Dvalue = 1
  Group = -> [H_element130,C_element140,N_element060,O_element121]
  conduct = 2
  density = 1
  expand = 3
  formula = G4_DNA_GUANOSINE
  name = G4_DNA_GUANOSINE
  specific = 4
FEATURE [App::DocumentObjectGroupPython] H_element131  label="H_element : 078"  # scripted group (container) (typed FeaturePython)
  n = 10
  ref = H_element
FEATURE [App::DocumentObjectGroupPython] C_element141  label="C_element : 086"  # scripted group (container) (typed FeaturePython)
  n = 9
  ref = C_element
FEATURE [App::DocumentObjectGroupPython] N_element061  label="N_element : 033"  # scripted group (container) (typed FeaturePython)
  n = 3
  ref = N_element
FEATURE [App::DocumentObjectGroupPython] O_element122  label="O_element : 075"  # scripted group (container) (typed FeaturePython)
  n = 5
  ref = O_element
FEATURE [App::DocumentObjectGroupPython] G4_DNA_CYTIDINE  # scripted group (container) (typed FeaturePython)
  Dunit = g/cm3
  Dvalue = 1
  Group = -> [H_element131,C_element141,N_element061,O_element122]
  conduct = 2
  density = 1
  expand = 3
  formula = G4_DNA_CYTIDINE
  name = G4_DNA_CYTIDINE
  specific = 4
FEATURE [App::DocumentObjectGroupPython] H_element132  label="H_element : 079"  # scripted group (container) (typed FeaturePython)
  n = 9
  ref = H_element
FEATURE [App::DocumentObjectGroupPython] C_element142  label="C_element : 087"  # scripted group (container) (typed FeaturePython)
  n = 9
  ref = C_element
FEATURE [App::DocumentObjectGroupPython] N_element062  label="N_element : 034"  # scripted group (container) (typed FeaturePython)
  n = 2
  ref = N_element
FEATURE [App::DocumentObjectGroupPython] O_element123  label="O_element : 076"  # scripted group (container) (typed FeaturePython)
  n = 6
  ref = O_element
FEATURE [App::DocumentObjectGroupPython] G4_DNA_URIDINE  # scripted group (container) (typed FeaturePython)
  Dunit = g/cm3
  Dvalue = 1
  Group = -> [H_element132,C_element142,N_element062,O_element123]
  conduct = 2
  density = 1
  expand = 3
  formula = G4_DNA_URIDINE
  name = G4_DNA_URIDINE
  specific = 4
FEATURE [App::DocumentObjectGroupPython] H_element133  label="H_element : 080"  # scripted group (container) (typed FeaturePython)
  n = 11
  ref = H_element
FEATURE [App::DocumentObjectGroupPython] C_element143  label="C_element : 088"  # scripted group (container) (typed FeaturePython)
  n = 10
  ref = C_element
FEATURE [App::DocumentObjectGroupPython] N_element063  label="N_element : 035"  # scripted group (container) (typed FeaturePython)
  n = 2
  ref = N_element
FEATURE [App::DocumentObjectGroupPython] O_element124  label="O_element : 077"  # scripted group (container) (typed FeaturePython)
  n = 6
  ref = O_element
FEATURE [App::DocumentObjectGroupPython] G4_DNA_METHYLURIDINE  # scripted group (container) (typed FeaturePython)
  Dunit = g/cm3
  Dvalue = 1
  Group = -> [H_element133,C_element143,N_element063,O_element124]
  conduct = 2
  density = 1
  expand = 3
  formula = G4_DNA_METHYLURIDINE
  name = G4_DNA_METHYLURIDINE
  specific = 4
FEATURE [App::DocumentObjectGroupPython] P_element014  label="P_element : 003"  # scripted group (container) (typed FeaturePython)
  n = 1
  ref = P_element
FEATURE [App::DocumentObjectGroupPython] O_element125  label="O_element : 078"  # scripted group (container) (typed FeaturePython)
  n = 3
  ref = O_element
FEATURE [App::DocumentObjectGroupPython] G4_DNA_MONOPHOSPHATE  # scripted group (container) (typed FeaturePython)
  Dunit = g/cm3
  Dvalue = 1
  Group = -> [P_element014,O_element125]
  conduct = 2
  density = 1
  expand = 3
  formula = G4_DNA_MONOPHOSPHATE
  name = G4_DNA_MONOPHOSPHATE
  specific = 4
FEATURE [App::DocumentObjectGroupPython] H_element134  label="H_element : 081"  # scripted group (container) (typed FeaturePython)
  n = 10
  ref = H_element
FEATURE [App::DocumentObjectGroupPython] C_element144  label="C_element : 089"  # scripted group (container) (typed FeaturePython)
  n = 10
  ref = C_element
FEATURE [App::DocumentObjectGroupPython] N_element064  label="N_element : 036"  # scripted group (container) (typed FeaturePython)
  n = 5
  ref = N_element
FEATURE [App::DocumentObjectGroupPython] O_element126  label="O_element : 079"  # scripted group (container) (typed FeaturePython)
  n = 7
  ref = O_element
FEATURE [App::DocumentObjectGroupPython] P_element015  label="P_element : 004"  # scripted group (container) (typed FeaturePython)
  n = 1
  ref = P_element
FEATURE [App::DocumentObjectGroupPython] G4_DNA_A  # scripted group (container) (typed FeaturePython)
  Dunit = g/cm3
  Dvalue = 1
  Group = -> [H_element134,C_element144,N_element064,O_element126,P_element015]
  conduct = 2
  density = 1
  expand = 3
  formula = G4_DNA_A
  name = G4_DNA_A
  specific = 4
FEATURE [App::DocumentObjectGroupPython] H_element135  label="H_element : 082"  # scripted group (container) (typed FeaturePython)
  n = 10
  ref = H_element
FEATURE [App::DocumentObjectGroupPython] C_element145  label="C_element : 090"  # scripted group (container) (typed FeaturePython)
  n = 10
  ref = C_element
FEATURE [App::DocumentObjectGroupPython] N_element065  label="N_element : 037"  # scripted group (container) (typed FeaturePython)
  n = 5
  ref = N_element
FEATURE [App::DocumentObjectGroupPython] O_element127  label="O_element : 8"  # scripted group (container) (typed FeaturePython)
  n = 8
  ref = O_element
FEATURE [App::DocumentObjectGroupPython] P_element016  label="P_element : 005"  # scripted group (container) (typed FeaturePython)
  n = 1
  ref = P_element
FEATURE [App::DocumentObjectGroupPython] G4_DNA_G  # scripted group (container) (typed FeaturePython)
  Dunit = g/cm3
  Dvalue = 1
  Group = -> [H_element135,C_element145,N_element065,O_element127,P_element016]
  conduct = 2
  density = 1
  expand = 3
  formula = G4_DNA_G
  name = G4_DNA_G
  specific = 4
FEATURE [App::DocumentObjectGroupPython] H_element136  label="H_element : 083"  # scripted group (container) (typed FeaturePython)
  n = 10
  ref = H_element
FEATURE [App::DocumentObjectGroupPython] C_element146  label="C_element : 091"  # scripted group (container) (typed FeaturePython)
  n = 9
  ref = C_element
FEATURE [App::DocumentObjectGroupPython] N_element066  label="N_element : 038"  # scripted group (container) (typed FeaturePython)
  n = 3
  ref = N_element
FEATURE [App::DocumentObjectGroupPython] O_element128  label="O_element : 080"  # scripted group (container) (typed FeaturePython)
  n = 8
  ref = O_element
FEATURE [App::DocumentObjectGroupPython] P_element017  label="P_element : 006"  # scripted group (container) (typed FeaturePython)
  n = 1
  ref = P_element
FEATURE [App::DocumentObjectGroupPython] G4_DNA_C  # scripted group (container) (typed FeaturePython)
  Dunit = g/cm3
  Dvalue = 1
  Group = -> [H_element136,C_element146,N_element066,O_element128,P_element017]
  conduct = 2
  density = 1
  expand = 3
  formula = G4_DNA_C
  name = G4_DNA_C
  specific = 4
FEATURE [App::DocumentObjectGroupPython] H_element137  label="H_element : 084"  # scripted group (container) (typed FeaturePython)
  n = 9
  ref = H_element
FEATURE [App::DocumentObjectGroupPython] C_element147  label="C_element : 092"  # scripted group (container) (typed FeaturePython)
  n = 9
  ref = C_element
FEATURE [App::DocumentObjectGroupPython] N_element067  label="N_element : 039"  # scripted group (container) (typed FeaturePython)
  n = 2
  ref = N_element
FEATURE [App::DocumentObjectGroupPython] O_element129  label="O_element : 9"  # scripted group (container) (typed FeaturePython)
  n = 9
  ref = O_element
FEATURE [App::DocumentObjectGroupPython] P_element018  label="P_element : 007"  # scripted group (container) (typed FeaturePython)
  n = 1
  ref = P_element
FEATURE [App::DocumentObjectGroupPython] G4_DNA_U  # scripted group (container) (typed FeaturePython)
  Dunit = g/cm3
  Dvalue = 1
  Group = -> [H_element137,C_element147,N_element067,O_element129,P_element018]
  conduct = 2
  density = 1
  expand = 3
  formula = G4_DNA_U
  name = G4_DNA_U
  specific = 4
FEATURE [App::DocumentObjectGroupPython] H_element138  label="H_element : 085"  # scripted group (container) (typed FeaturePython)
  n = 11
  ref = H_element
FEATURE [App::DocumentObjectGroupPython] C_element148  label="C_element : 093"  # scripted group (container) (typed FeaturePython)
  n = 10
  ref = C_element
FEATURE [App::DocumentObjectGroupPython] N_element068  label="N_element : 040"  # scripted group (container) (typed FeaturePython)
  n = 2
  ref = N_element
FEATURE [App::DocumentObjectGroupPython] O_element130  label="O_element : 081"  # scripted group (container) (typed FeaturePython)
  n = 9
  ref = O_element
FEATURE [App::DocumentObjectGroupPython] P_element019  label="P_element : 008"  # scripted group (container) (typed FeaturePython)
  n = 1
  ref = P_element
FEATURE [App::DocumentObjectGroupPython] G4_DNA_MU  # scripted group (container) (typed FeaturePython)
  Dunit = g/cm3
  Dvalue = 1
  Group = -> [H_element138,C_element148,N_element068,O_element130,P_element019]
  conduct = 2
  density = 1
  expand = 3
  formula = G4_DNA_MU
  name = G4_DNA_MU
  specific = 4
FEATURE [App::DocumentObjectGroupPython] BioChemical  # scripted group (container) (typed FeaturePython)
  Group = -> [G4_CYTOSINE,G4_THYMINE,G4_URACIL,G4_DNA_ADENINE,G4_DNA_GUANINE,G4_DNA_CYTOSINE,G4_DNA_THYMINE,G4_DNA_URACIL,G4_DNA_ADENOSINE,G4_DNA_GUANOSINE,G4_DNA_CYTIDINE,G4_DNA_URIDINE,G4_DNA_METHYLURIDINE,G4_DNA_MONOPHOSPHATE,G4_DNA_A,G4_DNA_G,G4_DNA_C,G4_DNA_U,G4_DNA_MU]
FEATURE [App::DocumentObjectGroupPython] G4Materials  # scripted group (container) (typed FeaturePython)
  Group = -> [NIST,Element,HEP,Space,BioChemical]
  version = 1
FEATURE [App::DocumentObjectGroupPython] Geant4  # scripted group (container) (typed FeaturePython)
  Group = -> [G4Isotopes,G4Elements,G4Materials]
FEATURE [App::DocumentObjectGroupPython] Materials  # scripted group (container) (typed FeaturePython)
  Group = -> [Geant4]
FEATURE [Part::FeaturePython] GDMLBox_WorldBox  # WARN: FeaturePython — macro-defined, semantics opaque (R4)
  lunit = 2
  material = 5
  x = 200
  y = 200
  z = 200
FEATURE [Sketcher::SketchObject] Sketch
  FullyConstrained = false
  sketch-geometry (36):
    g0: ArcOfParabola CenterX=18.1274 CenterY=-16.2535 CenterZ=0 NormalX=0 NormalY=0 NormalZ=1 Focal=8.09223 AngleXU=-3.10749 StartAngle=-21.4534 EndAngle=19.9625
    g1: GeomPoint X=10.0399 Y=-16.5294 Z=0
    g2: LineSegment StartX=18.1274 StartY=-16.2535 StartZ=0 EndX=10.0399 EndY=-16.5294 EndZ=0
    g3: ArcOfCircle CenterX=-6.88152 CenterY=-4.99689 CenterZ=0 NormalX=0 NormalY=0 NormalZ=1 AngleXU=0 Radius=13.9794 StartAngle=2.38084 EndAngle=7.05
    g4: ArcOfEllipse CenterX=-7.78764 CenterY=-33.8957 CenterZ=0 NormalX=0 NormalY=0 NormalZ=1 MajorRadius=18.086 MinorRadius=7.91522 AngleXU=-0.556234 StartAngle=4.96298 EndAngle=7.00481
    g5: LineSegment StartX=7.57186 StartY=-43.4449 StartZ=0 EndX=-23.1471 EndY=-24.3464 EndZ=0
    g6: LineSegment StartX=-3.60847 StartY=-27.1737 StartZ=0 EndX=-11.9668 EndY=-40.6177 EndZ=0
    g7: GeomPoint X=6.02282 Y=-42.4819 Z=0
    g8: GeomPoint X=-21.5981 Y=-25.3095 Z=0
    g9-g16: Circle x8 (B-spline internal-alignment scaffolding for g17; pole/knot coordinates omitted)
    g17: BSplineCurve PolesCount=8 KnotsCount=6 Degree=3 IsPeriodic=0
    g18-g23: GeomPoint x6 (B-spline internal-alignment scaffolding for g17; pole/knot coordinates omitted)
    g24: LineSegment StartX=-41.714 StartY=-18.5032 StartZ=0 EndX=-43.2734 EndY=-9.67993 EndZ=0
    g25: LineSegment StartX=-35.6082 StartY=7.90793 StartZ=0 EndX=-17.007 EndY=4.64145 EndZ=0
    g26: Circle CenterX=-9.18911 CenterY=-31.0442 CenterZ=0 NormalX=0 NormalY=0 NormalZ=1 AngleXU=0 Radius=8.40034
    g27: ArcOfHyperbola CenterX=-68.367 CenterY=18.2732 CenterZ=0 NormalX=0 NormalY=0 NormalZ=1 MajorRadius=22.1156 MinorRadius=7.852 AngleXU=-0.565391 StartAngle=-1.07469 EndAngle=0.964065
    g28: LineSegment StartX=-49.6931 StartY=6.4249 StartZ=0 EndX=-87.0409 EndY=30.1216 EndZ=0
    g29: LineSegment StartX=-45.4864 StartY=13.055 StartZ=0 EndX=-53.8998 EndY=-0.205161 EndZ=0
    g30: GeomPoint X=-48.551 Y=5.70028 Z=0
    g31: Ellipse CenterX=-34.2322 CenterY=-6.26645 CenterZ=0 NormalX=0 NormalY=0 NormalZ=1 MajorRadius=7.12528 MinorRadius=4.84017 AngleXU=-0.84953
    g32: LineSegment StartX=-29.5272 StartY=-11.6173 StartZ=0 EndX=-38.9373 EndY=-0.915575 EndZ=0
    g33: LineSegment StartX=-30.5974 StartY=-3.07031 StartZ=0 EndX=-37.8671 EndY=-9.46258 EndZ=0
    g34: GeomPoint X=-30.7794 Y=-10.1933 Z=0
    g35: GeomPoint X=-37.6851 Y=-2.33963 Z=0
  constraints (19):
    c: InternalAlignment(g1,g0)
    c: Coincident(g1,g2)
    c: Coincident(g0,g2)
    c: Coincident(g3,g0)
    c: InternalAlignment(g5-g8 -> g4) x4
    c: Coincident(g4,g0)
    c: Coincident(g17,g4)
    c: Weight(g9) = 1
    c: Equal(g9, g10-g16) x7
    c: InternalAlignment(g9-g16 -> g17) x8
    c: InternalAlignment(g18-g23 -> g17) x6
    c: Coincident(g24,g17)
    c: Coincident(g25,g3)
    c: InternalAlignment(g28,g27)
    c: InternalAlignment(g29,g27)
    c: InternalAlignment(g30,g27)
    c: Coincident(g24,g27)
    c: Coincident(g25,g27)
    c: InternalAlignment(g32-g35 -> g31) x4
FEATURE [Part::Extrusion] Extrude
  Base = -> Sketch
  Dir = (0,0,1)
  DirMode = 2
  FaceMakerClass = Part::FaceMakerBullseye
  LengthFwd = 10
  LengthRev = 0
  Solid = true
  Symmetric = false
FEATURE [App::Part] Part
  Group = -> [Sketch,Extrude]
  Origin = -> Origin001
  material = 5
FEATURE [App::Part] worldVOL
  Group = -> [GDMLBox_WorldBox,Part]
  Origin = -> Origin
